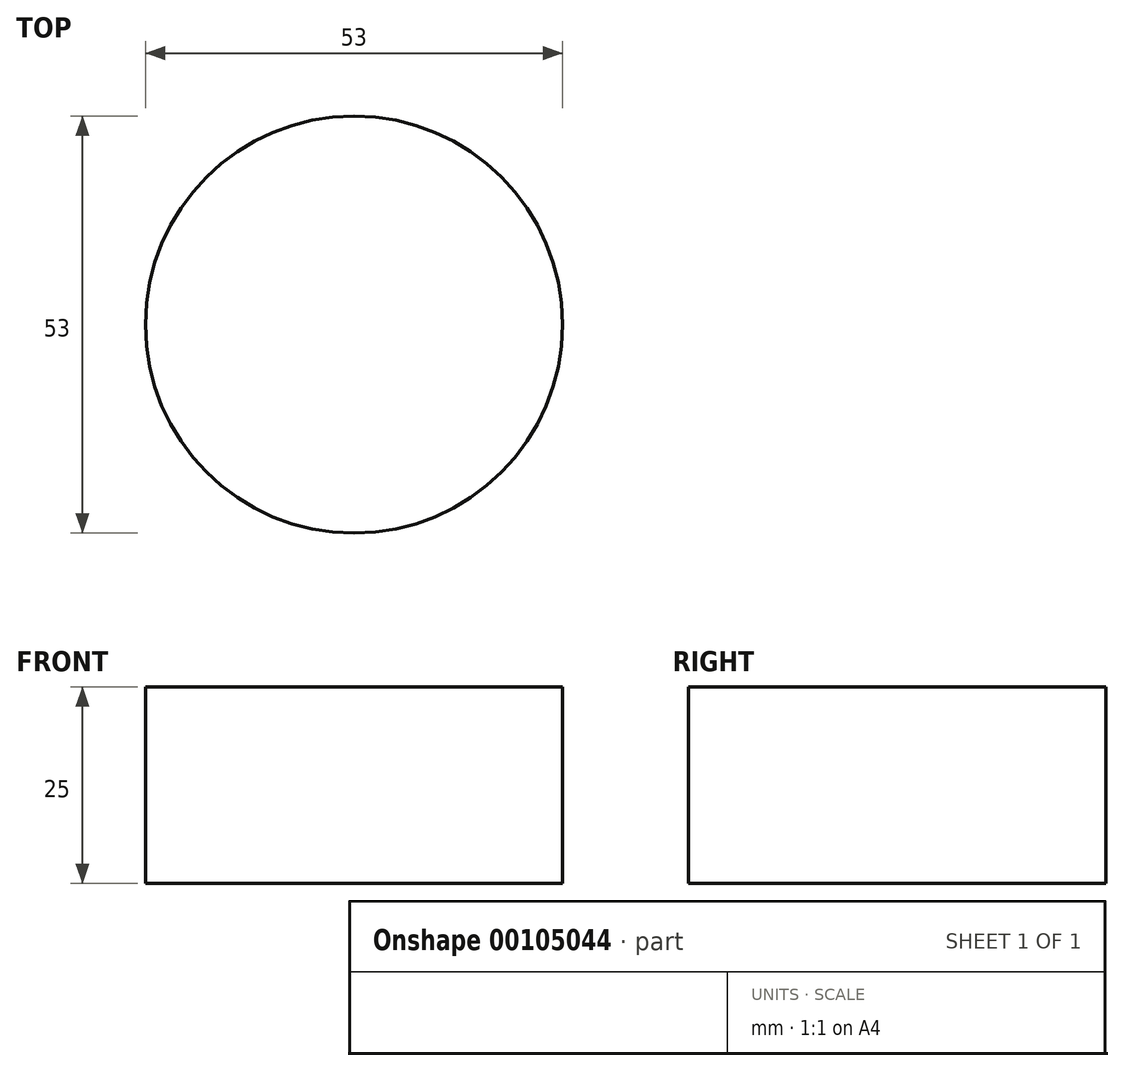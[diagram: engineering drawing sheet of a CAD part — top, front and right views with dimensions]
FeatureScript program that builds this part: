
annotation { "Feature Type Name" : "Feature", "Feature Type Description" : "" }
export const myFeature = defineFeature(function(context is Context, id is Id, definition is map)
    precondition{}
    {
        {
            assignVariable(context, id + "F0", {"name" : "G3", "anyValue" : 25});
        }
        {
            var Q0;
            Q0=qCreatedBy(makeId("Top.planeOp"),FACE);
            var sketch = newSketch(context, id + "F1", { "sketchPlane" : qUnion([Q0])});
            skCircle(sketch, "E0", {"center": v(390, 0) * mm, "radius": 26.5 * mm});
            skCircle(sketch, "E1", {"center": v(455, 0) * mm, "radius": 26.5 * mm});
            skCircle(sketch, "E2", {"center": v(520, 0) * mm, "radius": 26.5 * mm});
            skCircle(sketch, "E3", {"center": v(585, 0) * mm, "radius": 26.5 * mm});
            skCircle(sketch, "E4", {"center": v(650, 0) * mm, "radius": 26.5 * mm});
            skCircle(sketch, "E5", {"center": v(715, 0) * mm, "radius": 26.5 * mm});
            skCircle(sketch, "E6", {"center": v(780, 0) * mm, "radius": 26.5 * mm});
            skCircle(sketch, "E7", {"center": v(845, 0) * mm, "radius": 26.5 * mm});
            skCircle(sketch, "E8", {"center": v(910, 0) * mm, "radius": 26.5 * mm});
            skCircle(sketch, "E9", {"center": v(975, 0) * mm, "radius": 26.5 * mm});
            skCircle(sketch, "E10", {"center": v(1040, 0) * mm, "radius": 26.5 * mm});
            skCircle(sketch, "E11", {"center": v(1105, 0) * mm, "radius": 26.5 * mm});
            skCircle(sketch, "E12", {"center": v(1170, 0) * mm, "radius": 26.5 * mm});
            skCircle(sketch, "E13", {"center": v(1235, 0) * mm, "radius": 26.5 * mm});
            skCircle(sketch, "E14", {"center": v(1300, 0) * mm, "radius": 26.5 * mm});
            skCircle(sketch, "E15", {"center": v(1365, 0) * mm, "radius": 26.5 * mm});
            skCircle(sketch, "E16", {"center": v(1430, 0) * mm, "radius": 26.5 * mm});
            skCircle(sketch, "E17", {"center": v(1495, 0) * mm, "radius": 26.5 * mm});
            skCircle(sketch, "E18", {"center": v(1560, 0) * mm, "radius": 26.5 * mm});
            skCircle(sketch, "E19", {"center": v(422.5, 56.3) * mm, "radius": 26.5 * mm});
            skCircle(sketch, "E20", {"center": v(487.5, 56.3) * mm, "radius": 26.5 * mm});
            skCircle(sketch, "E21", {"center": v(552.5, 56.3) * mm, "radius": 26.5 * mm});
            skCircle(sketch, "E22", {"center": v(617.5, 56.3) * mm, "radius": 26.5 * mm});
            skCircle(sketch, "E23", {"center": v(682.5, 56.3) * mm, "radius": 26.5 * mm});
            skCircle(sketch, "E24", {"center": v(747.5, 56.3) * mm, "radius": 26.5 * mm});
            skCircle(sketch, "E25", {"center": v(812.5, 56.3) * mm, "radius": 26.5 * mm});
            skCircle(sketch, "E26", {"center": v(877.5, 56.3) * mm, "radius": 26.5 * mm});
            skCircle(sketch, "E27", {"center": v(942.5, 56.3) * mm, "radius": 26.5 * mm});
            skCircle(sketch, "E28", {"center": v(1007.5, 56.3) * mm, "radius": 26.5 * mm});
            skCircle(sketch, "E29", {"center": v(1072.5, 56.3) * mm, "radius": 26.5 * mm});
            skCircle(sketch, "E30", {"center": v(1137.5, 56.3) * mm, "radius": 26.5 * mm});
            skCircle(sketch, "E31", {"center": v(1202.5, 56.3) * mm, "radius": 26.5 * mm});
            skCircle(sketch, "E32", {"center": v(1267.5, 56.3) * mm, "radius": 26.5 * mm});
            skCircle(sketch, "E33", {"center": v(1332.5, 56.3) * mm, "radius": 26.5 * mm});
            skCircle(sketch, "E34", {"center": v(1397.5, 56.3) * mm, "radius": 26.5 * mm});
            skCircle(sketch, "E35", {"center": v(1462.5, 56.3) * mm, "radius": 26.5 * mm});
            skCircle(sketch, "E36", {"center": v(1527.5, 56.3) * mm, "radius": 26.5 * mm});
            skCircle(sketch, "E37", {"center": v(390, 112.58) * mm, "radius": 26.5 * mm});
            skCircle(sketch, "E38", {"center": v(455, 112.58) * mm, "radius": 26.5 * mm});
            skCircle(sketch, "E39", {"center": v(520, 112.58) * mm, "radius": 26.5 * mm});
            skCircle(sketch, "E40", {"center": v(585, 112.58) * mm, "radius": 26.5 * mm});
            skCircle(sketch, "E41", {"center": v(650, 112.58) * mm, "radius": 26.5 * mm});
            skCircle(sketch, "E42", {"center": v(715, 112.58) * mm, "radius": 26.5 * mm});
            skCircle(sketch, "E43", {"center": v(780, 112.58) * mm, "radius": 26.5 * mm});
            skCircle(sketch, "E44", {"center": v(845, 112.58) * mm, "radius": 26.5 * mm});
            skCircle(sketch, "E45", {"center": v(910, 112.58) * mm, "radius": 26.5 * mm});
            skCircle(sketch, "E46", {"center": v(975, 112.58) * mm, "radius": 26.5 * mm});
            skCircle(sketch, "E47", {"center": v(1040, 112.58) * mm, "radius": 26.5 * mm});
            skCircle(sketch, "E48", {"center": v(1105, 112.58) * mm, "radius": 26.5 * mm});
            skCircle(sketch, "E49", {"center": v(1170, 112.58) * mm, "radius": 26.5 * mm});
            skCircle(sketch, "E50", {"center": v(1235, 112.58) * mm, "radius": 26.5 * mm});
            skCircle(sketch, "E51", {"center": v(1300, 112.58) * mm, "radius": 26.5 * mm});
            skCircle(sketch, "E52", {"center": v(1365, 112.58) * mm, "radius": 26.5 * mm});
            skCircle(sketch, "E53", {"center": v(1430, 112.58) * mm, "radius": 26.5 * mm});
            skCircle(sketch, "E54", {"center": v(1495, 112.58) * mm, "radius": 26.5 * mm});
            skCircle(sketch, "E55", {"center": v(1560, 112.58) * mm, "radius": 26.5 * mm});
            skCircle(sketch, "E56", {"center": v(357.5, 168.87) * mm, "radius": 26.5 * mm});
            skCircle(sketch, "E57", {"center": v(422.5, 168.87) * mm, "radius": 26.5 * mm});
            skCircle(sketch, "E58", {"center": v(487.5, 168.87) * mm, "radius": 26.5 * mm});
            skCircle(sketch, "E59", {"center": v(552.5, 168.87) * mm, "radius": 26.5 * mm});
            skCircle(sketch, "E60", {"center": v(617.5, 168.87) * mm, "radius": 26.5 * mm});
            skCircle(sketch, "E61", {"center": v(682.5, 168.87) * mm, "radius": 26.5 * mm});
            skCircle(sketch, "E62", {"center": v(747.5, 168.87) * mm, "radius": 26.5 * mm});
            skCircle(sketch, "E63", {"center": v(812.5, 168.87) * mm, "radius": 26.5 * mm});
            skCircle(sketch, "E64", {"center": v(877.5, 168.87) * mm, "radius": 26.5 * mm});
            skCircle(sketch, "E65", {"center": v(942.5, 168.87) * mm, "radius": 26.5 * mm});
            skCircle(sketch, "E66", {"center": v(1007.5, 168.87) * mm, "radius": 26.5 * mm});
            skCircle(sketch, "E67", {"center": v(1072.5, 168.87) * mm, "radius": 26.5 * mm});
            skCircle(sketch, "E68", {"center": v(1137.5, 168.87) * mm, "radius": 26.5 * mm});
            skCircle(sketch, "E69", {"center": v(1202.5, 168.87) * mm, "radius": 26.5 * mm});
            skCircle(sketch, "E70", {"center": v(1267.5, 168.87) * mm, "radius": 26.5 * mm});
            skCircle(sketch, "E71", {"center": v(1332.5, 168.87) * mm, "radius": 26.5 * mm});
            skCircle(sketch, "E72", {"center": v(1397.5, 168.87) * mm, "radius": 26.5 * mm});
            skCircle(sketch, "E73", {"center": v(1462.5, 168.87) * mm, "radius": 26.5 * mm});
            skCircle(sketch, "E74", {"center": v(1527.5, 168.87) * mm, "radius": 26.5 * mm});
            skCircle(sketch, "E75", {"center": v(325, 225.17) * mm, "radius": 26.5 * mm});
            skCircle(sketch, "E76", {"center": v(390, 225.17) * mm, "radius": 26.5 * mm});
            skCircle(sketch, "E77", {"center": v(455, 225.17) * mm, "radius": 26.5 * mm});
            skCircle(sketch, "E78", {"center": v(520, 225.17) * mm, "radius": 26.5 * mm});
            skCircle(sketch, "E79", {"center": v(585, 225.17) * mm, "radius": 26.5 * mm});
            skCircle(sketch, "E80", {"center": v(650, 225.17) * mm, "radius": 26.5 * mm});
            skCircle(sketch, "E81", {"center": v(715, 225.17) * mm, "radius": 26.5 * mm});
            skCircle(sketch, "E82", {"center": v(780, 225.17) * mm, "radius": 26.5 * mm});
            skCircle(sketch, "E83", {"center": v(845, 225.17) * mm, "radius": 26.5 * mm});
            skCircle(sketch, "E84", {"center": v(910, 225.17) * mm, "radius": 26.5 * mm});
            skCircle(sketch, "E85", {"center": v(975, 225.17) * mm, "radius": 26.5 * mm});
            skCircle(sketch, "E86", {"center": v(1040, 225.17) * mm, "radius": 26.5 * mm});
            skCircle(sketch, "E87", {"center": v(1105, 225.17) * mm, "radius": 26.5 * mm});
            skCircle(sketch, "E88", {"center": v(1170, 225.17) * mm, "radius": 26.5 * mm});
            skCircle(sketch, "E89", {"center": v(1235, 225.17) * mm, "radius": 26.5 * mm});
            skCircle(sketch, "E90", {"center": v(1300, 225.17) * mm, "radius": 26.5 * mm});
            skCircle(sketch, "E91", {"center": v(1365, 225.17) * mm, "radius": 26.5 * mm});
            skCircle(sketch, "E92", {"center": v(1430, 225.17) * mm, "radius": 26.5 * mm});
            skCircle(sketch, "E93", {"center": v(1495, 225.17) * mm, "radius": 26.5 * mm});
            skCircle(sketch, "E94", {"center": v(1560, 225.17) * mm, "radius": 26.5 * mm});
            skCircle(sketch, "E95", {"center": v(292.5, 281.46) * mm, "radius": 26.5 * mm});
            skCircle(sketch, "E96", {"center": v(357.5, 281.46) * mm, "radius": 26.5 * mm});
            skCircle(sketch, "E97", {"center": v(422.5, 281.46) * mm, "radius": 26.5 * mm});
            skCircle(sketch, "E98", {"center": v(487.5, 281.46) * mm, "radius": 26.5 * mm});
            skCircle(sketch, "E99", {"center": v(552.5, 281.46) * mm, "radius": 26.5 * mm});
            skCircle(sketch, "E100", {"center": v(617.5, 281.46) * mm, "radius": 26.5 * mm});
            skCircle(sketch, "E101", {"center": v(682.5, 281.46) * mm, "radius": 26.5 * mm});
            skCircle(sketch, "E102", {"center": v(747.5, 281.46) * mm, "radius": 26.5 * mm});
            skCircle(sketch, "E103", {"center": v(812.5, 281.46) * mm, "radius": 26.5 * mm});
            skCircle(sketch, "E104", {"center": v(877.5, 281.46) * mm, "radius": 26.5 * mm});
            skCircle(sketch, "E105", {"center": v(942.5, 281.46) * mm, "radius": 26.5 * mm});
            skCircle(sketch, "E106", {"center": v(1007.5, 281.46) * mm, "radius": 26.5 * mm});
            skCircle(sketch, "E107", {"center": v(1072.5, 281.46) * mm, "radius": 26.5 * mm});
            skCircle(sketch, "E108", {"center": v(1137.5, 281.46) * mm, "radius": 26.5 * mm});
            skCircle(sketch, "E109", {"center": v(1202.5, 281.46) * mm, "radius": 26.5 * mm});
            skCircle(sketch, "E110", {"center": v(1267.5, 281.46) * mm, "radius": 26.5 * mm});
            skCircle(sketch, "E111", {"center": v(1332.5, 281.46) * mm, "radius": 26.5 * mm});
            skCircle(sketch, "E112", {"center": v(1397.5, 281.46) * mm, "radius": 26.5 * mm});
            skCircle(sketch, "E113", {"center": v(1462.5, 281.46) * mm, "radius": 26.5 * mm});
            skCircle(sketch, "E114", {"center": v(1527.5, 281.46) * mm, "radius": 26.5 * mm});
            skCircle(sketch, "E115", {"center": v(260, 337.75) * mm, "radius": 26.5 * mm});
            skCircle(sketch, "E116", {"center": v(325, 337.75) * mm, "radius": 26.5 * mm});
            skCircle(sketch, "E117", {"center": v(390, 337.75) * mm, "radius": 26.5 * mm});
            skCircle(sketch, "E118", {"center": v(455, 337.75) * mm, "radius": 26.5 * mm});
            skCircle(sketch, "E119", {"center": v(520, 337.75) * mm, "radius": 26.5 * mm});
            skCircle(sketch, "E120", {"center": v(585, 337.75) * mm, "radius": 26.5 * mm});
            skCircle(sketch, "E121", {"center": v(650, 337.75) * mm, "radius": 26.5 * mm});
            skCircle(sketch, "E122", {"center": v(715, 337.75) * mm, "radius": 26.5 * mm});
            skCircle(sketch, "E123", {"center": v(780, 337.75) * mm, "radius": 26.5 * mm});
            skCircle(sketch, "E124", {"center": v(845, 337.75) * mm, "radius": 26.5 * mm});
            skCircle(sketch, "E125", {"center": v(910, 337.75) * mm, "radius": 26.5 * mm});
            skCircle(sketch, "E126", {"center": v(975, 337.75) * mm, "radius": 26.5 * mm});
            skCircle(sketch, "E127", {"center": v(1040, 337.75) * mm, "radius": 26.5 * mm});
            skCircle(sketch, "E128", {"center": v(1105, 337.75) * mm, "radius": 26.5 * mm});
            skCircle(sketch, "E129", {"center": v(1170, 337.75) * mm, "radius": 26.5 * mm});
            skCircle(sketch, "E130", {"center": v(1235, 337.75) * mm, "radius": 26.5 * mm});
            skCircle(sketch, "E131", {"center": v(1300, 337.75) * mm, "radius": 26.5 * mm});
            skCircle(sketch, "E132", {"center": v(1365, 337.75) * mm, "radius": 26.5 * mm});
            skCircle(sketch, "E133", {"center": v(1430, 337.75) * mm, "radius": 26.5 * mm});
            skCircle(sketch, "E134", {"center": v(1495, 337.75) * mm, "radius": 26.5 * mm});
            skCircle(sketch, "E135", {"center": v(292.5, 394.04) * mm, "radius": 26.5 * mm});
            skCircle(sketch, "E136", {"center": v(357.5, 394.04) * mm, "radius": 26.5 * mm});
            skCircle(sketch, "E137", {"center": v(422.5, 394.04) * mm, "radius": 26.5 * mm});
            skCircle(sketch, "E138", {"center": v(487.5, 394.04) * mm, "radius": 26.5 * mm});
            skCircle(sketch, "E139", {"center": v(552.5, 394.04) * mm, "radius": 26.5 * mm});
            skCircle(sketch, "E140", {"center": v(617.5, 394.04) * mm, "radius": 26.5 * mm});
            skCircle(sketch, "E141", {"center": v(682.5, 394.04) * mm, "radius": 26.5 * mm});
            skCircle(sketch, "E142", {"center": v(747.5, 394.04) * mm, "radius": 26.5 * mm});
            skCircle(sketch, "E143", {"center": v(812.5, 394.04) * mm, "radius": 26.5 * mm});
            skCircle(sketch, "E144", {"center": v(877.5, 394.04) * mm, "radius": 26.5 * mm});
            skCircle(sketch, "E145", {"center": v(942.5, 394.04) * mm, "radius": 26.5 * mm});
            skCircle(sketch, "E146", {"center": v(1007.5, 394.04) * mm, "radius": 26.5 * mm});
            skCircle(sketch, "E147", {"center": v(1072.5, 394.04) * mm, "radius": 26.5 * mm});
            skCircle(sketch, "E148", {"center": v(1137.5, 394.04) * mm, "radius": 26.5 * mm});
            skCircle(sketch, "E149", {"center": v(1202.5, 394.04) * mm, "radius": 26.5 * mm});
            skCircle(sketch, "E150", {"center": v(1267.5, 394.04) * mm, "radius": 26.5 * mm});
            skCircle(sketch, "E151", {"center": v(1332.5, 394.04) * mm, "radius": 26.5 * mm});
            skCircle(sketch, "E152", {"center": v(1397.5, 394.04) * mm, "radius": 26.5 * mm});
            skCircle(sketch, "E153", {"center": v(1462.5, 394.04) * mm, "radius": 26.5 * mm});
            skCircle(sketch, "E154", {"center": v(1527.5, 394.04) * mm, "radius": 26.5 * mm});
            skCircle(sketch, "E155", {"center": v(325, 450.33) * mm, "radius": 26.5 * mm});
            skCircle(sketch, "E156", {"center": v(390, 450.33) * mm, "radius": 26.5 * mm});
            skCircle(sketch, "E157", {"center": v(455, 450.33) * mm, "radius": 26.5 * mm});
            skCircle(sketch, "E158", {"center": v(520, 450.33) * mm, "radius": 26.5 * mm});
            skCircle(sketch, "E159", {"center": v(585, 450.33) * mm, "radius": 26.5 * mm});
            skCircle(sketch, "E160", {"center": v(650, 450.33) * mm, "radius": 26.5 * mm});
            skCircle(sketch, "E161", {"center": v(715, 450.33) * mm, "radius": 26.5 * mm});
            skCircle(sketch, "E162", {"center": v(780, 450.33) * mm, "radius": 26.5 * mm});
            skCircle(sketch, "E163", {"center": v(845, 450.33) * mm, "radius": 26.5 * mm});
            skCircle(sketch, "E164", {"center": v(910, 450.33) * mm, "radius": 26.5 * mm});
            skCircle(sketch, "E165", {"center": v(975, 450.33) * mm, "radius": 26.5 * mm});
            skCircle(sketch, "E166", {"center": v(1040, 450.33) * mm, "radius": 26.5 * mm});
            skCircle(sketch, "E167", {"center": v(1105, 450.33) * mm, "radius": 26.5 * mm});
            skCircle(sketch, "E168", {"center": v(1170, 450.33) * mm, "radius": 26.5 * mm});
            skCircle(sketch, "E169", {"center": v(1235, 450.33) * mm, "radius": 26.5 * mm});
            skCircle(sketch, "E170", {"center": v(1300, 450.33) * mm, "radius": 26.5 * mm});
            skCircle(sketch, "E171", {"center": v(1365, 450.33) * mm, "radius": 26.5 * mm});
            skCircle(sketch, "E172", {"center": v(1430, 450.33) * mm, "radius": 26.5 * mm});
            skCircle(sketch, "E173", {"center": v(1495, 450.33) * mm, "radius": 26.5 * mm});
            skCircle(sketch, "E174", {"center": v(357.5, 506.62) * mm, "radius": 26.5 * mm});
            skCircle(sketch, "E175", {"center": v(422.5, 506.62) * mm, "radius": 26.5 * mm});
            skCircle(sketch, "E176", {"center": v(487.5, 506.62) * mm, "radius": 26.5 * mm});
            skCircle(sketch, "E177", {"center": v(552.5, 506.62) * mm, "radius": 26.5 * mm});
            skCircle(sketch, "E178", {"center": v(617.5, 506.62) * mm, "radius": 26.5 * mm});
            skCircle(sketch, "E179", {"center": v(682.5, 506.62) * mm, "radius": 26.5 * mm});
            skCircle(sketch, "E180", {"center": v(747.5, 506.62) * mm, "radius": 26.5 * mm});
            skCircle(sketch, "E181", {"center": v(812.5, 506.62) * mm, "radius": 26.5 * mm});
            skCircle(sketch, "E182", {"center": v(877.5, 506.62) * mm, "radius": 26.5 * mm});
            skCircle(sketch, "E183", {"center": v(1072.5, 506.62) * mm, "radius": 26.5 * mm});
            skCircle(sketch, "E184", {"center": v(1137.5, 506.62) * mm, "radius": 26.5 * mm});
            skCircle(sketch, "E185", {"center": v(1202.5, 506.62) * mm, "radius": 26.5 * mm});
            skCircle(sketch, "E186", {"center": v(1267.5, 506.62) * mm, "radius": 26.5 * mm});
            skCircle(sketch, "E187", {"center": v(1332.5, 506.62) * mm, "radius": 26.5 * mm});
            skCircle(sketch, "E188", {"center": v(1397.5, 506.62) * mm, "radius": 26.5 * mm});
            skCircle(sketch, "E189", {"center": v(1462.5, 506.62) * mm, "radius": 26.5 * mm});
            skCircle(sketch, "E190", {"center": v(390, 562.92) * mm, "radius": 26.5 * mm});
            skCircle(sketch, "E191", {"center": v(455, 562.92) * mm, "radius": 26.5 * mm});
            skCircle(sketch, "E192", {"center": v(520, 562.92) * mm, "radius": 26.5 * mm});
            skCircle(sketch, "E193", {"center": v(585, 562.92) * mm, "radius": 26.5 * mm});
            skCircle(sketch, "E194", {"center": v(650, 562.92) * mm, "radius": 26.5 * mm});
            skCircle(sketch, "E195", {"center": v(715, 562.92) * mm, "radius": 26.5 * mm});
            skCircle(sketch, "E196", {"center": v(780, 562.92) * mm, "radius": 26.5 * mm});
            skCircle(sketch, "E197", {"center": v(845, 562.92) * mm, "radius": 26.5 * mm});
            skCircle(sketch, "E198", {"center": v(1105, 562.92) * mm, "radius": 26.5 * mm});
            skCircle(sketch, "E199", {"center": v(1170, 562.92) * mm, "radius": 26.5 * mm});
            skCircle(sketch, "E200", {"center": v(1235, 562.92) * mm, "radius": 26.5 * mm});
            skCircle(sketch, "E201", {"center": v(1300, 562.92) * mm, "radius": 26.5 * mm});
            skCircle(sketch, "E202", {"center": v(1365, 562.92) * mm, "radius": 26.5 * mm});
            skCircle(sketch, "E203", {"center": v(1430, 562.92) * mm, "radius": 26.5 * mm});
            skCircle(sketch, "E204", {"center": v(422.5, 619.2) * mm, "radius": 26.5 * mm});
            skCircle(sketch, "E205", {"center": v(487.5, 619.2) * mm, "radius": 26.5 * mm});
            skCircle(sketch, "E206", {"center": v(552.5, 619.2) * mm, "radius": 26.5 * mm});
            skCircle(sketch, "E207", {"center": v(617.5, 619.2) * mm, "radius": 26.5 * mm});
            skCircle(sketch, "E208", {"center": v(682.5, 619.2) * mm, "radius": 26.5 * mm});
            skCircle(sketch, "E209", {"center": v(747.5, 619.2) * mm, "radius": 26.5 * mm});
            skCircle(sketch, "E210", {"center": v(812.5, 619.2) * mm, "radius": 26.5 * mm});
            skCircle(sketch, "E211", {"center": v(877.5, 619.2) * mm, "radius": 26.5 * mm});
            skCircle(sketch, "E212", {"center": v(1072.5, 619.2) * mm, "radius": 26.5 * mm});
            skCircle(sketch, "E213", {"center": v(1137.5, 619.2) * mm, "radius": 26.5 * mm});
            skCircle(sketch, "E214", {"center": v(1202.5, 619.2) * mm, "radius": 26.5 * mm});
            skCircle(sketch, "E215", {"center": v(1267.5, 619.2) * mm, "radius": 26.5 * mm});
            skCircle(sketch, "E216", {"center": v(1332.5, 619.2) * mm, "radius": 26.5 * mm});
            skCircle(sketch, "E217", {"center": v(1397.5, 619.2) * mm, "radius": 26.5 * mm});
            skCircle(sketch, "E218", {"center": v(455, 675.5) * mm, "radius": 26.5 * mm});
            skCircle(sketch, "E219", {"center": v(520, 675.5) * mm, "radius": 26.5 * mm});
            skCircle(sketch, "E220", {"center": v(585, 675.5) * mm, "radius": 26.5 * mm});
            skCircle(sketch, "E221", {"center": v(650, 675.5) * mm, "radius": 26.5 * mm});
            skCircle(sketch, "E222", {"center": v(715, 675.5) * mm, "radius": 26.5 * mm});
            skCircle(sketch, "E223", {"center": v(780, 675.5) * mm, "radius": 26.5 * mm});
            skCircle(sketch, "E224", {"center": v(845, 675.5) * mm, "radius": 26.5 * mm});
            skCircle(sketch, "E225", {"center": v(910, 675.5) * mm, "radius": 26.5 * mm});
            skCircle(sketch, "E226", {"center": v(975, 675.5) * mm, "radius": 26.5 * mm});
            skCircle(sketch, "E227", {"center": v(1040, 675.5) * mm, "radius": 26.5 * mm});
            skCircle(sketch, "E228", {"center": v(1105, 675.5) * mm, "radius": 26.5 * mm});
            skCircle(sketch, "E229", {"center": v(1170, 675.5) * mm, "radius": 26.5 * mm});
            skCircle(sketch, "E230", {"center": v(1235, 675.5) * mm, "radius": 26.5 * mm});
            skCircle(sketch, "E231", {"center": v(1300, 675.5) * mm, "radius": 26.5 * mm});
            skCircle(sketch, "E232", {"center": v(1365, 675.5) * mm, "radius": 26.5 * mm});
            skCircle(sketch, "E233", {"center": v(487.5, 731.8) * mm, "radius": 26.5 * mm});
            skCircle(sketch, "E234", {"center": v(552.5, 731.8) * mm, "radius": 26.5 * mm});
            skCircle(sketch, "E235", {"center": v(617.5, 731.8) * mm, "radius": 26.5 * mm});
            skCircle(sketch, "E236", {"center": v(682.5, 731.8) * mm, "radius": 26.5 * mm});
            skCircle(sketch, "E237", {"center": v(747.5, 731.8) * mm, "radius": 26.5 * mm});
            skCircle(sketch, "E238", {"center": v(812.5, 731.8) * mm, "radius": 26.5 * mm});
            skCircle(sketch, "E239", {"center": v(877.5, 731.8) * mm, "radius": 26.5 * mm});
            skCircle(sketch, "E240", {"center": v(942.5, 731.8) * mm, "radius": 26.5 * mm});
            skCircle(sketch, "E241", {"center": v(1007.5, 731.8) * mm, "radius": 26.5 * mm});
            skCircle(sketch, "E242", {"center": v(1072.5, 731.8) * mm, "radius": 26.5 * mm});
            skCircle(sketch, "E243", {"center": v(1137.5, 731.8) * mm, "radius": 26.5 * mm});
            skCircle(sketch, "E244", {"center": v(1202.5, 731.8) * mm, "radius": 26.5 * mm});
            skCircle(sketch, "E245", {"center": v(1267.5, 731.8) * mm, "radius": 26.5 * mm});
            skCircle(sketch, "E246", {"center": v(1332.5, 731.8) * mm, "radius": 26.5 * mm});
            skCircle(sketch, "E247", {"center": v(1397.5, 731.8) * mm, "radius": 26.5 * mm});
            skCircle(sketch, "E248", {"center": v(520, 788.08) * mm, "radius": 26.5 * mm});
            skCircle(sketch, "E249", {"center": v(585, 788.08) * mm, "radius": 26.5 * mm});
            skCircle(sketch, "E250", {"center": v(650, 788.08) * mm, "radius": 26.5 * mm});
            skCircle(sketch, "E251", {"center": v(715, 788.08) * mm, "radius": 26.5 * mm});
            skCircle(sketch, "E252", {"center": v(780, 788.08) * mm, "radius": 26.5 * mm});
            skCircle(sketch, "E253", {"center": v(845, 788.08) * mm, "radius": 26.5 * mm});
            skCircle(sketch, "E254", {"center": v(910, 788.08) * mm, "radius": 26.5 * mm});
            skCircle(sketch, "E255", {"center": v(975, 788.08) * mm, "radius": 26.5 * mm});
            skCircle(sketch, "E256", {"center": v(1040, 788.08) * mm, "radius": 26.5 * mm});
            skCircle(sketch, "E257", {"center": v(1105, 788.08) * mm, "radius": 26.5 * mm});
            skCircle(sketch, "E258", {"center": v(1170, 788.08) * mm, "radius": 26.5 * mm});
            skCircle(sketch, "E259", {"center": v(1235, 788.08) * mm, "radius": 26.5 * mm});
            skCircle(sketch, "E260", {"center": v(1300, 788.08) * mm, "radius": 26.5 * mm});
            skCircle(sketch, "E261", {"center": v(1365, 788.08) * mm, "radius": 26.5 * mm});
            skCircle(sketch, "E262", {"center": v(552.5, 844.37) * mm, "radius": 26.5 * mm});
            skCircle(sketch, "E263", {"center": v(617.5, 844.37) * mm, "radius": 26.5 * mm});
            skCircle(sketch, "E264", {"center": v(682.5, 844.37) * mm, "radius": 26.5 * mm});
            skCircle(sketch, "E265", {"center": v(747.5, 844.37) * mm, "radius": 26.5 * mm});
            skCircle(sketch, "E266", {"center": v(812.5, 844.37) * mm, "radius": 26.5 * mm});
            skCircle(sketch, "E267", {"center": v(877.5, 844.37) * mm, "radius": 26.5 * mm});
            skCircle(sketch, "E268", {"center": v(942.5, 844.37) * mm, "radius": 26.5 * mm});
            skCircle(sketch, "E269", {"center": v(1007.5, 844.37) * mm, "radius": 26.5 * mm});
            skCircle(sketch, "E270", {"center": v(1072.5, 844.37) * mm, "radius": 26.5 * mm});
            skCircle(sketch, "E271", {"center": v(1137.5, 844.37) * mm, "radius": 26.5 * mm});
            skCircle(sketch, "E272", {"center": v(1202.5, 844.37) * mm, "radius": 26.5 * mm});
            skCircle(sketch, "E273", {"center": v(1267.5, 844.37) * mm, "radius": 26.5 * mm});
            skCircle(sketch, "E274", {"center": v(1332.5, 844.37) * mm, "radius": 26.5 * mm});
            skCircle(sketch, "E275", {"center": v(585, 900.67) * mm, "radius": 26.5 * mm});
            skCircle(sketch, "E276", {"center": v(650, 900.67) * mm, "radius": 26.5 * mm});
            skCircle(sketch, "E277", {"center": v(715, 900.67) * mm, "radius": 26.5 * mm});
            skCircle(sketch, "E278", {"center": v(780, 900.67) * mm, "radius": 26.5 * mm});
            skCircle(sketch, "E279", {"center": v(845, 900.67) * mm, "radius": 26.5 * mm});
            skCircle(sketch, "E280", {"center": v(910, 900.67) * mm, "radius": 26.5 * mm});
            skCircle(sketch, "E281", {"center": v(975, 900.67) * mm, "radius": 26.5 * mm});
            skCircle(sketch, "E282", {"center": v(1040, 900.67) * mm, "radius": 26.5 * mm});
            skCircle(sketch, "E283", {"center": v(1105, 900.67) * mm, "radius": 26.5 * mm});
            skCircle(sketch, "E284", {"center": v(1170, 900.67) * mm, "radius": 26.5 * mm});
            skCircle(sketch, "E285", {"center": v(1235, 900.67) * mm, "radius": 26.5 * mm});
            skCircle(sketch, "E286", {"center": v(617.5, 956.96) * mm, "radius": 26.5 * mm});
            skCircle(sketch, "E287", {"center": v(682.5, 956.96) * mm, "radius": 26.5 * mm});
            skCircle(sketch, "E288", {"center": v(747.5, 956.96) * mm, "radius": 26.5 * mm});
            skCircle(sketch, "E289", {"center": v(812.5, 956.96) * mm, "radius": 26.5 * mm});
            skCircle(sketch, "E290", {"center": v(877.5, 956.96) * mm, "radius": 26.5 * mm});
            skCircle(sketch, "E291", {"center": v(942.5, 956.96) * mm, "radius": 26.5 * mm});
            skCircle(sketch, "E292", {"center": v(1007.5, 956.96) * mm, "radius": 26.5 * mm});
            skCircle(sketch, "E293", {"center": v(1072.5, 956.96) * mm, "radius": 26.5 * mm});
            skCircle(sketch, "E294", {"center": v(1137.5, 956.96) * mm, "radius": 26.5 * mm});
            skCircle(sketch, "E295", {"center": v(1202.5, 956.96) * mm, "radius": 26.5 * mm});
            skCircle(sketch, "E296", {"center": v(650, 1013.25) * mm, "radius": 26.5 * mm});
            skCircle(sketch, "E297", {"center": v(715, 1013.25) * mm, "radius": 26.5 * mm});
            skCircle(sketch, "E298", {"center": v(780, 1013.25) * mm, "radius": 26.5 * mm});
            skCircle(sketch, "E299", {"center": v(845, 1013.25) * mm, "radius": 26.5 * mm});
            skCircle(sketch, "E300", {"center": v(910, 1013.25) * mm, "radius": 26.5 * mm});
            skCircle(sketch, "E301", {"center": v(975, 1013.25) * mm, "radius": 26.5 * mm});
            skCircle(sketch, "E302", {"center": v(1040, 1013.25) * mm, "radius": 26.5 * mm});
            skCircle(sketch, "E303", {"center": v(1105, 1013.25) * mm, "radius": 26.5 * mm});
            skCircle(sketch, "E304", {"center": v(1170, 1013.25) * mm, "radius": 26.5 * mm});
            skCircle(sketch, "E305", {"center": v(682.5, 1069.54) * mm, "radius": 26.5 * mm});
            skCircle(sketch, "E306", {"center": v(747.5, 1069.54) * mm, "radius": 26.5 * mm});
            skCircle(sketch, "E307", {"center": v(812.5, 1069.54) * mm, "radius": 26.5 * mm});
            skCircle(sketch, "E308", {"center": v(877.5, 1069.54) * mm, "radius": 26.5 * mm});
            skCircle(sketch, "E309", {"center": v(942.5, 1069.54) * mm, "radius": 26.5 * mm});
            skCircle(sketch, "E310", {"center": v(1007.5, 1069.54) * mm, "radius": 26.5 * mm});
            skCircle(sketch, "E311", {"center": v(1072.5, 1069.54) * mm, "radius": 26.5 * mm});
            skCircle(sketch, "E312", {"center": v(1137.5, 1069.54) * mm, "radius": 26.5 * mm});
            skCircle(sketch, "E313", {"center": v(715, 1125.83) * mm, "radius": 26.5 * mm});
            skCircle(sketch, "E314", {"center": v(780, 1125.83) * mm, "radius": 26.5 * mm});
            skCircle(sketch, "E315", {"center": v(845, 1125.83) * mm, "radius": 26.5 * mm});
            skCircle(sketch, "E316", {"center": v(910, 1125.83) * mm, "radius": 26.5 * mm});
            skCircle(sketch, "E317", {"center": v(975, 1125.83) * mm, "radius": 26.5 * mm});
            skCircle(sketch, "E318", {"center": v(1040, 1125.83) * mm, "radius": 26.5 * mm});
            skCircle(sketch, "E319", {"center": v(1105, 1125.83) * mm, "radius": 26.5 * mm});
            skCircle(sketch, "E320", {"center": v(747.5, 1182.12) * mm, "radius": 26.5 * mm});
            skCircle(sketch, "E321", {"center": v(812.5, 1182.12) * mm, "radius": 26.5 * mm});
            skCircle(sketch, "E322", {"center": v(877.5, 1182.12) * mm, "radius": 26.5 * mm});
            skCircle(sketch, "E323", {"center": v(942.5, 1182.12) * mm, "radius": 26.5 * mm});
            skCircle(sketch, "E324", {"center": v(1007.5, 1182.12) * mm, "radius": 26.5 * mm});
            skCircle(sketch, "E325", {"center": v(780, 1238.42) * mm, "radius": 26.5 * mm});
            skCircle(sketch, "E326", {"center": v(845, 1238.42) * mm, "radius": 26.5 * mm});
            skCircle(sketch, "E327", {"center": v(910, 1238.42) * mm, "radius": 26.5 * mm});
            skCircle(sketch, "E328", {"center": v(975, 1238.42) * mm, "radius": 26.5 * mm});
            skCircle(sketch, "E329", {"center": v(812.5, 1294.7) * mm, "radius": 26.5 * mm});
            skCircle(sketch, "E330", {"center": v(877.5, 1294.7) * mm, "radius": 26.5 * mm});
            skCircle(sketch, "E331", {"center": v(0, 0) * mm, "radius": 304.8 * mm, "construction": true});
            skCircle(sketch, "E332", {"center": v(0, 0) * mm, "radius": 1655.21 * mm, "construction": true});
            skCircle(sketch, "E333", {"center": v(975, 562.92) * mm, "radius": 58 * mm});
            skCircle(sketch, "E334", {"center": v(195, 337.75) * mm, "radius": 26.5 * mm});
            skCircle(sketch, "E335", {"center": v(227.5, 394.04) * mm, "radius": 26.5 * mm});
            skCircle(sketch, "E336", {"center": v(260, 450.33) * mm, "radius": 26.5 * mm});
            skCircle(sketch, "E337", {"center": v(292.5, 506.62) * mm, "radius": 26.5 * mm});
            skCircle(sketch, "E338", {"center": v(325, 562.92) * mm, "radius": 26.5 * mm});
            skCircle(sketch, "E339", {"center": v(357.5, 619.2) * mm, "radius": 26.5 * mm});
            skCircle(sketch, "E340", {"center": v(390, 675.5) * mm, "radius": 26.5 * mm});
            skCircle(sketch, "E341", {"center": v(422.5, 731.8) * mm, "radius": 26.5 * mm});
            skCircle(sketch, "E342", {"center": v(455, 788.08) * mm, "radius": 26.5 * mm});
            skCircle(sketch, "E343", {"center": v(487.5, 844.37) * mm, "radius": 26.5 * mm});
            skCircle(sketch, "E344", {"center": v(520, 900.67) * mm, "radius": 26.5 * mm});
            skCircle(sketch, "E345", {"center": v(552.5, 956.96) * mm, "radius": 26.5 * mm});
            skCircle(sketch, "E346", {"center": v(585, 1013.25) * mm, "radius": 26.5 * mm});
            skCircle(sketch, "E347", {"center": v(617.5, 1069.54) * mm, "radius": 26.5 * mm});
            skCircle(sketch, "E348", {"center": v(650, 1125.83) * mm, "radius": 26.5 * mm});
            skCircle(sketch, "E349", {"center": v(682.5, 1182.12) * mm, "radius": 26.5 * mm});
            skCircle(sketch, "E350", {"center": v(715, 1238.42) * mm, "radius": 26.5 * mm});
            skCircle(sketch, "E351", {"center": v(747.5, 1294.7) * mm, "radius": 26.5 * mm});
            skCircle(sketch, "E352", {"center": v(780, 1351) * mm, "radius": 26.5 * mm});
            skCircle(sketch, "E353", {"center": v(162.5, 394.04) * mm, "radius": 26.5 * mm});
            skCircle(sketch, "E354", {"center": v(195, 450.33) * mm, "radius": 26.5 * mm});
            skCircle(sketch, "E355", {"center": v(227.5, 506.62) * mm, "radius": 26.5 * mm});
            skCircle(sketch, "E356", {"center": v(260, 562.92) * mm, "radius": 26.5 * mm});
            skCircle(sketch, "E357", {"center": v(292.5, 619.2) * mm, "radius": 26.5 * mm});
            skCircle(sketch, "E358", {"center": v(325, 675.5) * mm, "radius": 26.5 * mm});
            skCircle(sketch, "E359", {"center": v(357.5, 731.8) * mm, "radius": 26.5 * mm});
            skCircle(sketch, "E360", {"center": v(390, 788.08) * mm, "radius": 26.5 * mm});
            skCircle(sketch, "E361", {"center": v(422.5, 844.37) * mm, "radius": 26.5 * mm});
            skCircle(sketch, "E362", {"center": v(455, 900.67) * mm, "radius": 26.5 * mm});
            skCircle(sketch, "E363", {"center": v(487.5, 956.96) * mm, "radius": 26.5 * mm});
            skCircle(sketch, "E364", {"center": v(520, 1013.25) * mm, "radius": 26.5 * mm});
            skCircle(sketch, "E365", {"center": v(552.5, 1069.54) * mm, "radius": 26.5 * mm});
            skCircle(sketch, "E366", {"center": v(585, 1125.83) * mm, "radius": 26.5 * mm});
            skCircle(sketch, "E367", {"center": v(617.5, 1182.12) * mm, "radius": 26.5 * mm});
            skCircle(sketch, "E368", {"center": v(650, 1238.42) * mm, "radius": 26.5 * mm});
            skCircle(sketch, "E369", {"center": v(682.5, 1294.7) * mm, "radius": 26.5 * mm});
            skCircle(sketch, "E370", {"center": v(715, 1351) * mm, "radius": 26.5 * mm});
            skCircle(sketch, "E371", {"center": v(97.5, 394.04) * mm, "radius": 26.5 * mm});
            skCircle(sketch, "E372", {"center": v(130, 450.33) * mm, "radius": 26.5 * mm});
            skCircle(sketch, "E373", {"center": v(162.5, 506.62) * mm, "radius": 26.5 * mm});
            skCircle(sketch, "E374", {"center": v(195, 562.92) * mm, "radius": 26.5 * mm});
            skCircle(sketch, "E375", {"center": v(227.5, 619.2) * mm, "radius": 26.5 * mm});
            skCircle(sketch, "E376", {"center": v(260, 675.5) * mm, "radius": 26.5 * mm});
            skCircle(sketch, "E377", {"center": v(292.5, 731.8) * mm, "radius": 26.5 * mm});
            skCircle(sketch, "E378", {"center": v(325, 788.08) * mm, "radius": 26.5 * mm});
            skCircle(sketch, "E379", {"center": v(357.5, 844.37) * mm, "radius": 26.5 * mm});
            skCircle(sketch, "E380", {"center": v(390, 900.67) * mm, "radius": 26.5 * mm});
            skCircle(sketch, "E381", {"center": v(422.5, 956.96) * mm, "radius": 26.5 * mm});
            skCircle(sketch, "E382", {"center": v(455, 1013.25) * mm, "radius": 26.5 * mm});
            skCircle(sketch, "E383", {"center": v(487.5, 1069.54) * mm, "radius": 26.5 * mm});
            skCircle(sketch, "E384", {"center": v(520, 1125.83) * mm, "radius": 26.5 * mm});
            skCircle(sketch, "E385", {"center": v(552.5, 1182.12) * mm, "radius": 26.5 * mm});
            skCircle(sketch, "E386", {"center": v(585, 1238.42) * mm, "radius": 26.5 * mm});
            skCircle(sketch, "E387", {"center": v(617.5, 1294.7) * mm, "radius": 26.5 * mm});
            skCircle(sketch, "E388", {"center": v(650, 1351) * mm, "radius": 26.5 * mm});
            skCircle(sketch, "E389", {"center": v(682.5, 1407.3) * mm, "radius": 26.5 * mm});
            skCircle(sketch, "E390", {"center": v(32.5, 394.04) * mm, "radius": 26.5 * mm});
            skCircle(sketch, "E391", {"center": v(65, 450.33) * mm, "radius": 26.5 * mm});
            skCircle(sketch, "E392", {"center": v(97.5, 506.62) * mm, "radius": 26.5 * mm});
            skCircle(sketch, "E393", {"center": v(130, 562.92) * mm, "radius": 26.5 * mm});
            skCircle(sketch, "E394", {"center": v(162.5, 619.2) * mm, "radius": 26.5 * mm});
            skCircle(sketch, "E395", {"center": v(195, 675.5) * mm, "radius": 26.5 * mm});
            skCircle(sketch, "E396", {"center": v(227.5, 731.8) * mm, "radius": 26.5 * mm});
            skCircle(sketch, "E397", {"center": v(260, 788.08) * mm, "radius": 26.5 * mm});
            skCircle(sketch, "E398", {"center": v(292.5, 844.37) * mm, "radius": 26.5 * mm});
            skCircle(sketch, "E399", {"center": v(325, 900.67) * mm, "radius": 26.5 * mm});
            skCircle(sketch, "E400", {"center": v(357.5, 956.96) * mm, "radius": 26.5 * mm});
            skCircle(sketch, "E401", {"center": v(390, 1013.25) * mm, "radius": 26.5 * mm});
            skCircle(sketch, "E402", {"center": v(422.5, 1069.54) * mm, "radius": 26.5 * mm});
            skCircle(sketch, "E403", {"center": v(455, 1125.83) * mm, "radius": 26.5 * mm});
            skCircle(sketch, "E404", {"center": v(487.5, 1182.12) * mm, "radius": 26.5 * mm});
            skCircle(sketch, "E405", {"center": v(520, 1238.42) * mm, "radius": 26.5 * mm});
            skCircle(sketch, "E406", {"center": v(552.5, 1294.7) * mm, "radius": 26.5 * mm});
            skCircle(sketch, "E407", {"center": v(585, 1351) * mm, "radius": 26.5 * mm});
            skCircle(sketch, "E408", {"center": v(617.5, 1407.3) * mm, "radius": 26.5 * mm});
            skCircle(sketch, "E409", {"center": v(-32.5, 394.04) * mm, "radius": 26.5 * mm});
            skCircle(sketch, "E410", {"center": v(0, 450.33) * mm, "radius": 26.5 * mm});
            skCircle(sketch, "E411", {"center": v(32.5, 506.62) * mm, "radius": 26.5 * mm});
            skCircle(sketch, "E412", {"center": v(65, 562.92) * mm, "radius": 26.5 * mm});
            skCircle(sketch, "E413", {"center": v(97.5, 619.2) * mm, "radius": 26.5 * mm});
            skCircle(sketch, "E414", {"center": v(130, 675.5) * mm, "radius": 26.5 * mm});
            skCircle(sketch, "E415", {"center": v(162.5, 731.8) * mm, "radius": 26.5 * mm});
            skCircle(sketch, "E416", {"center": v(195, 788.08) * mm, "radius": 26.5 * mm});
            skCircle(sketch, "E417", {"center": v(227.5, 844.37) * mm, "radius": 26.5 * mm});
            skCircle(sketch, "E418", {"center": v(260, 900.67) * mm, "radius": 26.5 * mm});
            skCircle(sketch, "E419", {"center": v(292.5, 956.96) * mm, "radius": 26.5 * mm});
            skCircle(sketch, "E420", {"center": v(325, 1013.25) * mm, "radius": 26.5 * mm});
            skCircle(sketch, "E421", {"center": v(357.5, 1069.54) * mm, "radius": 26.5 * mm});
            skCircle(sketch, "E422", {"center": v(390, 1125.83) * mm, "radius": 26.5 * mm});
            skCircle(sketch, "E423", {"center": v(422.5, 1182.12) * mm, "radius": 26.5 * mm});
            skCircle(sketch, "E424", {"center": v(455, 1238.42) * mm, "radius": 26.5 * mm});
            skCircle(sketch, "E425", {"center": v(487.5, 1294.7) * mm, "radius": 26.5 * mm});
            skCircle(sketch, "E426", {"center": v(520, 1351) * mm, "radius": 26.5 * mm});
            skCircle(sketch, "E427", {"center": v(552.5, 1407.3) * mm, "radius": 26.5 * mm});
            skCircle(sketch, "E428", {"center": v(585, 1463.58) * mm, "radius": 26.5 * mm});
            skCircle(sketch, "E429", {"center": v(-97.5, 394.04) * mm, "radius": 26.5 * mm});
            skCircle(sketch, "E430", {"center": v(-65, 450.33) * mm, "radius": 26.5 * mm});
            skCircle(sketch, "E431", {"center": v(-32.5, 506.62) * mm, "radius": 26.5 * mm});
            skCircle(sketch, "E432", {"center": v(0, 562.92) * mm, "radius": 26.5 * mm});
            skCircle(sketch, "E433", {"center": v(32.5, 619.2) * mm, "radius": 26.5 * mm});
            skCircle(sketch, "E434", {"center": v(65, 675.5) * mm, "radius": 26.5 * mm});
            skCircle(sketch, "E435", {"center": v(97.5, 731.8) * mm, "radius": 26.5 * mm});
            skCircle(sketch, "E436", {"center": v(130, 788.08) * mm, "radius": 26.5 * mm});
            skCircle(sketch, "E437", {"center": v(162.5, 844.37) * mm, "radius": 26.5 * mm});
            skCircle(sketch, "E438", {"center": v(195, 900.67) * mm, "radius": 26.5 * mm});
            skCircle(sketch, "E439", {"center": v(227.5, 956.96) * mm, "radius": 26.5 * mm});
            skCircle(sketch, "E440", {"center": v(260, 1013.25) * mm, "radius": 26.5 * mm});
            skCircle(sketch, "E441", {"center": v(292.5, 1069.54) * mm, "radius": 26.5 * mm});
            skCircle(sketch, "E442", {"center": v(325, 1125.83) * mm, "radius": 26.5 * mm});
            skCircle(sketch, "E443", {"center": v(357.5, 1182.12) * mm, "radius": 26.5 * mm});
            skCircle(sketch, "E444", {"center": v(390, 1238.42) * mm, "radius": 26.5 * mm});
            skCircle(sketch, "E445", {"center": v(422.5, 1294.7) * mm, "radius": 26.5 * mm});
            skCircle(sketch, "E446", {"center": v(455, 1351) * mm, "radius": 26.5 * mm});
            skCircle(sketch, "E447", {"center": v(487.5, 1407.3) * mm, "radius": 26.5 * mm});
            skCircle(sketch, "E448", {"center": v(520, 1463.58) * mm, "radius": 26.5 * mm});
            skCircle(sketch, "E449", {"center": v(-162.5, 394.04) * mm, "radius": 26.5 * mm});
            skCircle(sketch, "E450", {"center": v(-130, 450.33) * mm, "radius": 26.5 * mm});
            skCircle(sketch, "E451", {"center": v(-97.5, 506.62) * mm, "radius": 26.5 * mm});
            skCircle(sketch, "E452", {"center": v(-65, 562.92) * mm, "radius": 26.5 * mm});
            skCircle(sketch, "E453", {"center": v(-32.5, 619.2) * mm, "radius": 26.5 * mm});
            skCircle(sketch, "E454", {"center": v(0, 675.5) * mm, "radius": 26.5 * mm});
            skCircle(sketch, "E455", {"center": v(32.5, 731.8) * mm, "radius": 26.5 * mm});
            skCircle(sketch, "E456", {"center": v(65, 788.08) * mm, "radius": 26.5 * mm});
            skCircle(sketch, "E457", {"center": v(97.5, 844.37) * mm, "radius": 26.5 * mm});
            skCircle(sketch, "E458", {"center": v(130, 900.67) * mm, "radius": 26.5 * mm});
            skCircle(sketch, "E459", {"center": v(162.5, 956.96) * mm, "radius": 26.5 * mm});
            skCircle(sketch, "E460", {"center": v(195, 1013.25) * mm, "radius": 26.5 * mm});
            skCircle(sketch, "E461", {"center": v(227.5, 1069.54) * mm, "radius": 26.5 * mm});
            skCircle(sketch, "E462", {"center": v(260, 1125.83) * mm, "radius": 26.5 * mm});
            skCircle(sketch, "E463", {"center": v(292.5, 1182.12) * mm, "radius": 26.5 * mm});
            skCircle(sketch, "E464", {"center": v(325, 1238.42) * mm, "radius": 26.5 * mm});
            skCircle(sketch, "E465", {"center": v(357.5, 1294.7) * mm, "radius": 26.5 * mm});
            skCircle(sketch, "E466", {"center": v(390, 1351) * mm, "radius": 26.5 * mm});
            skCircle(sketch, "E467", {"center": v(422.5, 1407.3) * mm, "radius": 26.5 * mm});
            skCircle(sketch, "E468", {"center": v(455, 1463.58) * mm, "radius": 26.5 * mm});
            skCircle(sketch, "E469", {"center": v(-195, 450.33) * mm, "radius": 26.5 * mm});
            skCircle(sketch, "E470", {"center": v(-162.5, 506.62) * mm, "radius": 26.5 * mm});
            skCircle(sketch, "E471", {"center": v(-130, 562.92) * mm, "radius": 26.5 * mm});
            skCircle(sketch, "E472", {"center": v(-97.5, 619.2) * mm, "radius": 26.5 * mm});
            skCircle(sketch, "E473", {"center": v(-65, 675.5) * mm, "radius": 26.5 * mm});
            skCircle(sketch, "E474", {"center": v(-32.5, 731.8) * mm, "radius": 26.5 * mm});
            skCircle(sketch, "E475", {"center": v(0, 788.08) * mm, "radius": 26.5 * mm});
            skCircle(sketch, "E476", {"center": v(32.5, 844.37) * mm, "radius": 26.5 * mm});
            skCircle(sketch, "E477", {"center": v(65, 900.67) * mm, "radius": 26.5 * mm});
            skCircle(sketch, "E478", {"center": v(97.5, 956.96) * mm, "radius": 26.5 * mm});
            skCircle(sketch, "E479", {"center": v(130, 1013.25) * mm, "radius": 26.5 * mm});
            skCircle(sketch, "E480", {"center": v(162.5, 1069.54) * mm, "radius": 26.5 * mm});
            skCircle(sketch, "E481", {"center": v(195, 1125.83) * mm, "radius": 26.5 * mm});
            skCircle(sketch, "E482", {"center": v(227.5, 1182.12) * mm, "radius": 26.5 * mm});
            skCircle(sketch, "E483", {"center": v(260, 1238.42) * mm, "radius": 26.5 * mm});
            skCircle(sketch, "E484", {"center": v(292.5, 1294.7) * mm, "radius": 26.5 * mm});
            skCircle(sketch, "E485", {"center": v(325, 1351) * mm, "radius": 26.5 * mm});
            skCircle(sketch, "E486", {"center": v(357.5, 1407.3) * mm, "radius": 26.5 * mm});
            skCircle(sketch, "E487", {"center": v(390, 1463.58) * mm, "radius": 26.5 * mm});
            skCircle(sketch, "E488", {"center": v(422.5, 1519.87) * mm, "radius": 26.5 * mm});
            skCircle(sketch, "E489", {"center": v(-227.5, 506.62) * mm, "radius": 26.5 * mm});
            skCircle(sketch, "E490", {"center": v(-195, 562.92) * mm, "radius": 26.5 * mm});
            skCircle(sketch, "E491", {"center": v(-162.5, 619.2) * mm, "radius": 26.5 * mm});
            skCircle(sketch, "E492", {"center": v(-130, 675.5) * mm, "radius": 26.5 * mm});
            skCircle(sketch, "E493", {"center": v(-97.5, 731.8) * mm, "radius": 26.5 * mm});
            skCircle(sketch, "E494", {"center": v(-65, 788.08) * mm, "radius": 26.5 * mm});
            skCircle(sketch, "E495", {"center": v(-32.5, 844.37) * mm, "radius": 26.5 * mm});
            skCircle(sketch, "E496", {"center": v(0, 900.67) * mm, "radius": 26.5 * mm});
            skCircle(sketch, "E497", {"center": v(32.5, 956.96) * mm, "radius": 26.5 * mm});
            skCircle(sketch, "E498", {"center": v(65, 1013.25) * mm, "radius": 26.5 * mm});
            skCircle(sketch, "E499", {"center": v(97.5, 1069.54) * mm, "radius": 26.5 * mm});
            skCircle(sketch, "E500", {"center": v(130, 1125.83) * mm, "radius": 26.5 * mm});
            skCircle(sketch, "E501", {"center": v(162.5, 1182.12) * mm, "radius": 26.5 * mm});
            skCircle(sketch, "E502", {"center": v(195, 1238.42) * mm, "radius": 26.5 * mm});
            skCircle(sketch, "E503", {"center": v(227.5, 1294.7) * mm, "radius": 26.5 * mm});
            skCircle(sketch, "E504", {"center": v(260, 1351) * mm, "radius": 26.5 * mm});
            skCircle(sketch, "E505", {"center": v(292.5, 1407.3) * mm, "radius": 26.5 * mm});
            skCircle(sketch, "E506", {"center": v(325, 1463.58) * mm, "radius": 26.5 * mm});
            skCircle(sketch, "E507", {"center": v(357.5, 1519.87) * mm, "radius": 26.5 * mm});
            skCircle(sketch, "E508", {"center": v(-260, 562.92) * mm, "radius": 26.5 * mm});
            skCircle(sketch, "E509", {"center": v(-227.5, 619.2) * mm, "radius": 26.5 * mm});
            skCircle(sketch, "E510", {"center": v(-195, 675.5) * mm, "radius": 26.5 * mm});
            skCircle(sketch, "E511", {"center": v(-162.5, 731.8) * mm, "radius": 26.5 * mm});
            skCircle(sketch, "E512", {"center": v(-130, 788.08) * mm, "radius": 26.5 * mm});
            skCircle(sketch, "E513", {"center": v(-97.5, 844.37) * mm, "radius": 26.5 * mm});
            skCircle(sketch, "E514", {"center": v(-65, 900.67) * mm, "radius": 26.5 * mm});
            skCircle(sketch, "E515", {"center": v(-32.5, 956.96) * mm, "radius": 26.5 * mm});
            skCircle(sketch, "E516", {"center": v(0, 1013.25) * mm, "radius": 26.5 * mm});
            skCircle(sketch, "E517", {"center": v(97.5, 1182.12) * mm, "radius": 26.5 * mm});
            skCircle(sketch, "E518", {"center": v(130, 1238.42) * mm, "radius": 26.5 * mm});
            skCircle(sketch, "E519", {"center": v(162.5, 1294.7) * mm, "radius": 26.5 * mm});
            skCircle(sketch, "E520", {"center": v(195, 1351) * mm, "radius": 26.5 * mm});
            skCircle(sketch, "E521", {"center": v(227.5, 1407.3) * mm, "radius": 26.5 * mm});
            skCircle(sketch, "E522", {"center": v(260, 1463.58) * mm, "radius": 26.5 * mm});
            skCircle(sketch, "E523", {"center": v(292.5, 1519.87) * mm, "radius": 26.5 * mm});
            skCircle(sketch, "E524", {"center": v(-292.5, 619.2) * mm, "radius": 26.5 * mm});
            skCircle(sketch, "E525", {"center": v(-260, 675.5) * mm, "radius": 26.5 * mm});
            skCircle(sketch, "E526", {"center": v(-227.5, 731.8) * mm, "radius": 26.5 * mm});
            skCircle(sketch, "E527", {"center": v(-195, 788.08) * mm, "radius": 26.5 * mm});
            skCircle(sketch, "E528", {"center": v(-162.5, 844.37) * mm, "radius": 26.5 * mm});
            skCircle(sketch, "E529", {"center": v(-130, 900.67) * mm, "radius": 26.5 * mm});
            skCircle(sketch, "E530", {"center": v(-97.5, 956.96) * mm, "radius": 26.5 * mm});
            skCircle(sketch, "E531", {"center": v(-65, 1013.25) * mm, "radius": 26.5 * mm});
            skCircle(sketch, "E532", {"center": v(65, 1238.42) * mm, "radius": 26.5 * mm});
            skCircle(sketch, "E533", {"center": v(97.5, 1294.7) * mm, "radius": 26.5 * mm});
            skCircle(sketch, "E534", {"center": v(130, 1351) * mm, "radius": 26.5 * mm});
            skCircle(sketch, "E535", {"center": v(162.5, 1407.3) * mm, "radius": 26.5 * mm});
            skCircle(sketch, "E536", {"center": v(195, 1463.58) * mm, "radius": 26.5 * mm});
            skCircle(sketch, "E537", {"center": v(227.5, 1519.87) * mm, "radius": 26.5 * mm});
            skCircle(sketch, "E538", {"center": v(-325, 675.5) * mm, "radius": 26.5 * mm});
            skCircle(sketch, "E539", {"center": v(-292.5, 731.8) * mm, "radius": 26.5 * mm});
            skCircle(sketch, "E540", {"center": v(-260, 788.08) * mm, "radius": 26.5 * mm});
            skCircle(sketch, "E541", {"center": v(-227.5, 844.37) * mm, "radius": 26.5 * mm});
            skCircle(sketch, "E542", {"center": v(-195, 900.67) * mm, "radius": 26.5 * mm});
            skCircle(sketch, "E543", {"center": v(-162.5, 956.96) * mm, "radius": 26.5 * mm});
            skCircle(sketch, "E544", {"center": v(-130, 1013.25) * mm, "radius": 26.5 * mm});
            skCircle(sketch, "E545", {"center": v(-97.5, 1069.54) * mm, "radius": 26.5 * mm});
            skCircle(sketch, "E546", {"center": v(0, 1238.42) * mm, "radius": 26.5 * mm});
            skCircle(sketch, "E547", {"center": v(32.5, 1294.7) * mm, "radius": 26.5 * mm});
            skCircle(sketch, "E548", {"center": v(65, 1351) * mm, "radius": 26.5 * mm});
            skCircle(sketch, "E549", {"center": v(97.5, 1407.3) * mm, "radius": 26.5 * mm});
            skCircle(sketch, "E550", {"center": v(130, 1463.58) * mm, "radius": 26.5 * mm});
            skCircle(sketch, "E551", {"center": v(162.5, 1519.87) * mm, "radius": 26.5 * mm});
            skCircle(sketch, "E552", {"center": v(-357.5, 731.8) * mm, "radius": 26.5 * mm});
            skCircle(sketch, "E553", {"center": v(-325, 788.08) * mm, "radius": 26.5 * mm});
            skCircle(sketch, "E554", {"center": v(-292.5, 844.37) * mm, "radius": 26.5 * mm});
            skCircle(sketch, "E555", {"center": v(-260, 900.67) * mm, "radius": 26.5 * mm});
            skCircle(sketch, "E556", {"center": v(-227.5, 956.96) * mm, "radius": 26.5 * mm});
            skCircle(sketch, "E557", {"center": v(-195, 1013.25) * mm, "radius": 26.5 * mm});
            skCircle(sketch, "E558", {"center": v(-162.5, 1069.54) * mm, "radius": 26.5 * mm});
            skCircle(sketch, "E559", {"center": v(-130, 1125.83) * mm, "radius": 26.5 * mm});
            skCircle(sketch, "E560", {"center": v(-97.5, 1182.12) * mm, "radius": 26.5 * mm});
            skCircle(sketch, "E561", {"center": v(-65, 1238.42) * mm, "radius": 26.5 * mm});
            skCircle(sketch, "E562", {"center": v(-32.5, 1294.7) * mm, "radius": 26.5 * mm});
            skCircle(sketch, "E563", {"center": v(0, 1351) * mm, "radius": 26.5 * mm});
            skCircle(sketch, "E564", {"center": v(32.5, 1407.3) * mm, "radius": 26.5 * mm});
            skCircle(sketch, "E565", {"center": v(65, 1463.58) * mm, "radius": 26.5 * mm});
            skCircle(sketch, "E566", {"center": v(97.5, 1519.87) * mm, "radius": 26.5 * mm});
            skCircle(sketch, "E567", {"center": v(-390, 788.08) * mm, "radius": 26.5 * mm});
            skCircle(sketch, "E568", {"center": v(-357.5, 844.37) * mm, "radius": 26.5 * mm});
            skCircle(sketch, "E569", {"center": v(-325, 900.67) * mm, "radius": 26.5 * mm});
            skCircle(sketch, "E570", {"center": v(-292.5, 956.96) * mm, "radius": 26.5 * mm});
            skCircle(sketch, "E571", {"center": v(-260, 1013.25) * mm, "radius": 26.5 * mm});
            skCircle(sketch, "E572", {"center": v(-227.5, 1069.54) * mm, "radius": 26.5 * mm});
            skCircle(sketch, "E573", {"center": v(-195, 1125.83) * mm, "radius": 26.5 * mm});
            skCircle(sketch, "E574", {"center": v(-162.5, 1182.12) * mm, "radius": 26.5 * mm});
            skCircle(sketch, "E575", {"center": v(-130, 1238.42) * mm, "radius": 26.5 * mm});
            skCircle(sketch, "E576", {"center": v(-97.5, 1294.7) * mm, "radius": 26.5 * mm});
            skCircle(sketch, "E577", {"center": v(-65, 1351) * mm, "radius": 26.5 * mm});
            skCircle(sketch, "E578", {"center": v(-32.5, 1407.3) * mm, "radius": 26.5 * mm});
            skCircle(sketch, "E579", {"center": v(0, 1463.58) * mm, "radius": 26.5 * mm});
            skCircle(sketch, "E580", {"center": v(32.5, 1519.87) * mm, "radius": 26.5 * mm});
            skCircle(sketch, "E581", {"center": v(65, 1576.17) * mm, "radius": 26.5 * mm});
            skCircle(sketch, "E582", {"center": v(-422.5, 844.37) * mm, "radius": 26.5 * mm});
            skCircle(sketch, "E583", {"center": v(-390, 900.67) * mm, "radius": 26.5 * mm});
            skCircle(sketch, "E584", {"center": v(-357.5, 956.96) * mm, "radius": 26.5 * mm});
            skCircle(sketch, "E585", {"center": v(-325, 1013.25) * mm, "radius": 26.5 * mm});
            skCircle(sketch, "E586", {"center": v(-292.5, 1069.54) * mm, "radius": 26.5 * mm});
            skCircle(sketch, "E587", {"center": v(-260, 1125.83) * mm, "radius": 26.5 * mm});
            skCircle(sketch, "E588", {"center": v(-227.5, 1182.12) * mm, "radius": 26.5 * mm});
            skCircle(sketch, "E589", {"center": v(-195, 1238.42) * mm, "radius": 26.5 * mm});
            skCircle(sketch, "E590", {"center": v(-162.5, 1294.7) * mm, "radius": 26.5 * mm});
            skCircle(sketch, "E591", {"center": v(-130, 1351) * mm, "radius": 26.5 * mm});
            skCircle(sketch, "E592", {"center": v(-97.5, 1407.3) * mm, "radius": 26.5 * mm});
            skCircle(sketch, "E593", {"center": v(-65, 1463.58) * mm, "radius": 26.5 * mm});
            skCircle(sketch, "E594", {"center": v(-32.5, 1519.87) * mm, "radius": 26.5 * mm});
            skCircle(sketch, "E595", {"center": v(0, 1576.17) * mm, "radius": 26.5 * mm});
            skCircle(sketch, "E596", {"center": v(-455, 900.67) * mm, "radius": 26.5 * mm});
            skCircle(sketch, "E597", {"center": v(-422.5, 956.96) * mm, "radius": 26.5 * mm});
            skCircle(sketch, "E598", {"center": v(-390, 1013.25) * mm, "radius": 26.5 * mm});
            skCircle(sketch, "E599", {"center": v(-357.5, 1069.54) * mm, "radius": 26.5 * mm});
            skCircle(sketch, "E600", {"center": v(-325, 1125.83) * mm, "radius": 26.5 * mm});
            skCircle(sketch, "E601", {"center": v(-292.5, 1182.12) * mm, "radius": 26.5 * mm});
            skCircle(sketch, "E602", {"center": v(-260, 1238.42) * mm, "radius": 26.5 * mm});
            skCircle(sketch, "E603", {"center": v(-227.5, 1294.7) * mm, "radius": 26.5 * mm});
            skCircle(sketch, "E604", {"center": v(-195, 1351) * mm, "radius": 26.5 * mm});
            skCircle(sketch, "E605", {"center": v(-162.5, 1407.3) * mm, "radius": 26.5 * mm});
            skCircle(sketch, "E606", {"center": v(-130, 1463.58) * mm, "radius": 26.5 * mm});
            skCircle(sketch, "E607", {"center": v(-97.5, 1519.87) * mm, "radius": 26.5 * mm});
            skCircle(sketch, "E608", {"center": v(-65, 1576.17) * mm, "radius": 26.5 * mm});
            skCircle(sketch, "E609", {"center": v(-487.5, 956.96) * mm, "radius": 26.5 * mm});
            skCircle(sketch, "E610", {"center": v(-455, 1013.25) * mm, "radius": 26.5 * mm});
            skCircle(sketch, "E611", {"center": v(-422.5, 1069.54) * mm, "radius": 26.5 * mm});
            skCircle(sketch, "E612", {"center": v(-390, 1125.83) * mm, "radius": 26.5 * mm});
            skCircle(sketch, "E613", {"center": v(-357.5, 1182.12) * mm, "radius": 26.5 * mm});
            skCircle(sketch, "E614", {"center": v(-325, 1238.42) * mm, "radius": 26.5 * mm});
            skCircle(sketch, "E615", {"center": v(-292.5, 1294.7) * mm, "radius": 26.5 * mm});
            skCircle(sketch, "E616", {"center": v(-260, 1351) * mm, "radius": 26.5 * mm});
            skCircle(sketch, "E617", {"center": v(-227.5, 1407.3) * mm, "radius": 26.5 * mm});
            skCircle(sketch, "E618", {"center": v(-195, 1463.58) * mm, "radius": 26.5 * mm});
            skCircle(sketch, "E619", {"center": v(-162.5, 1519.87) * mm, "radius": 26.5 * mm});
            skCircle(sketch, "E620", {"center": v(-520, 1013.25) * mm, "radius": 26.5 * mm});
            skCircle(sketch, "E621", {"center": v(-487.5, 1069.54) * mm, "radius": 26.5 * mm});
            skCircle(sketch, "E622", {"center": v(-455, 1125.83) * mm, "radius": 26.5 * mm});
            skCircle(sketch, "E623", {"center": v(-422.5, 1182.12) * mm, "radius": 26.5 * mm});
            skCircle(sketch, "E624", {"center": v(-390, 1238.42) * mm, "radius": 26.5 * mm});
            skCircle(sketch, "E625", {"center": v(-357.5, 1294.7) * mm, "radius": 26.5 * mm});
            skCircle(sketch, "E626", {"center": v(-325, 1351) * mm, "radius": 26.5 * mm});
            skCircle(sketch, "E627", {"center": v(-292.5, 1407.3) * mm, "radius": 26.5 * mm});
            skCircle(sketch, "E628", {"center": v(-260, 1463.58) * mm, "radius": 26.5 * mm});
            skCircle(sketch, "E629", {"center": v(-227.5, 1519.87) * mm, "radius": 26.5 * mm});
            skCircle(sketch, "E630", {"center": v(-552.5, 1069.54) * mm, "radius": 26.5 * mm});
            skCircle(sketch, "E631", {"center": v(-520, 1125.83) * mm, "radius": 26.5 * mm});
            skCircle(sketch, "E632", {"center": v(-487.5, 1182.12) * mm, "radius": 26.5 * mm});
            skCircle(sketch, "E633", {"center": v(-455, 1238.42) * mm, "radius": 26.5 * mm});
            skCircle(sketch, "E634", {"center": v(-422.5, 1294.7) * mm, "radius": 26.5 * mm});
            skCircle(sketch, "E635", {"center": v(-390, 1351) * mm, "radius": 26.5 * mm});
            skCircle(sketch, "E636", {"center": v(-357.5, 1407.3) * mm, "radius": 26.5 * mm});
            skCircle(sketch, "E637", {"center": v(-325, 1463.58) * mm, "radius": 26.5 * mm});
            skCircle(sketch, "E638", {"center": v(-292.5, 1519.87) * mm, "radius": 26.5 * mm});
            skCircle(sketch, "E639", {"center": v(-585, 1125.83) * mm, "radius": 26.5 * mm});
            skCircle(sketch, "E640", {"center": v(-552.5, 1182.12) * mm, "radius": 26.5 * mm});
            skCircle(sketch, "E641", {"center": v(-520, 1238.42) * mm, "radius": 26.5 * mm});
            skCircle(sketch, "E642", {"center": v(-487.5, 1294.7) * mm, "radius": 26.5 * mm});
            skCircle(sketch, "E643", {"center": v(-455, 1351) * mm, "radius": 26.5 * mm});
            skCircle(sketch, "E644", {"center": v(-422.5, 1407.3) * mm, "radius": 26.5 * mm});
            skCircle(sketch, "E645", {"center": v(-390, 1463.58) * mm, "radius": 26.5 * mm});
            skCircle(sketch, "E646", {"center": v(-357.5, 1519.87) * mm, "radius": 26.5 * mm});
            skCircle(sketch, "E647", {"center": v(-617.5, 1182.12) * mm, "radius": 26.5 * mm});
            skCircle(sketch, "E648", {"center": v(-585, 1238.42) * mm, "radius": 26.5 * mm});
            skCircle(sketch, "E649", {"center": v(-552.5, 1294.7) * mm, "radius": 26.5 * mm});
            skCircle(sketch, "E650", {"center": v(-520, 1351) * mm, "radius": 26.5 * mm});
            skCircle(sketch, "E651", {"center": v(-487.5, 1407.3) * mm, "radius": 26.5 * mm});
            skCircle(sketch, "E652", {"center": v(-455, 1463.58) * mm, "radius": 26.5 * mm});
            skCircle(sketch, "E653", {"center": v(-422.5, 1519.87) * mm, "radius": 26.5 * mm});
            skCircle(sketch, "E654", {"center": v(-650, 1238.42) * mm, "radius": 26.5 * mm});
            skCircle(sketch, "E655", {"center": v(-617.5, 1294.7) * mm, "radius": 26.5 * mm});
            skCircle(sketch, "E656", {"center": v(-585, 1351) * mm, "radius": 26.5 * mm});
            skCircle(sketch, "E657", {"center": v(-552.5, 1407.3) * mm, "radius": 26.5 * mm});
            skCircle(sketch, "E658", {"center": v(-520, 1463.58) * mm, "radius": 26.5 * mm});
            skCircle(sketch, "E659", {"center": v(-682.5, 1294.7) * mm, "radius": 26.5 * mm});
            skCircle(sketch, "E660", {"center": v(-650, 1351) * mm, "radius": 26.5 * mm});
            skCircle(sketch, "E661", {"center": v(-617.5, 1407.3) * mm, "radius": 26.5 * mm});
            skCircle(sketch, "E662", {"center": v(-585, 1463.58) * mm, "radius": 26.5 * mm});
            skCircle(sketch, "E663", {"center": v(-715, 1351) * mm, "radius": 26.5 * mm});
            skCircle(sketch, "E664", {"center": v(-682.5, 1407.3) * mm, "radius": 26.5 * mm});
            skCircle(sketch, "E665", {"center": v(0, 1125.83) * mm, "radius": 58 * mm});
            skCircle(sketch, "E666", {"center": v(-195, 337.75) * mm, "radius": 26.5 * mm});
            skCircle(sketch, "E667", {"center": v(-227.5, 394.04) * mm, "radius": 26.5 * mm});
            skCircle(sketch, "E668", {"center": v(-260, 450.33) * mm, "radius": 26.5 * mm});
            skCircle(sketch, "E669", {"center": v(-292.5, 506.62) * mm, "radius": 26.5 * mm});
            skCircle(sketch, "E670", {"center": v(-325, 562.92) * mm, "radius": 26.5 * mm});
            skCircle(sketch, "E671", {"center": v(-357.5, 619.2) * mm, "radius": 26.5 * mm});
            skCircle(sketch, "E672", {"center": v(-390, 675.5) * mm, "radius": 26.5 * mm});
            skCircle(sketch, "E673", {"center": v(-422.5, 731.8) * mm, "radius": 26.5 * mm});
            skCircle(sketch, "E674", {"center": v(-455, 788.08) * mm, "radius": 26.5 * mm});
            skCircle(sketch, "E675", {"center": v(-487.5, 844.37) * mm, "radius": 26.5 * mm});
            skCircle(sketch, "E676", {"center": v(-520, 900.67) * mm, "radius": 26.5 * mm});
            skCircle(sketch, "E677", {"center": v(-552.5, 956.96) * mm, "radius": 26.5 * mm});
            skCircle(sketch, "E678", {"center": v(-585, 1013.25) * mm, "radius": 26.5 * mm});
            skCircle(sketch, "E679", {"center": v(-617.5, 1069.54) * mm, "radius": 26.5 * mm});
            skCircle(sketch, "E680", {"center": v(-650, 1125.83) * mm, "radius": 26.5 * mm});
            skCircle(sketch, "E681", {"center": v(-682.5, 1182.12) * mm, "radius": 26.5 * mm});
            skCircle(sketch, "E682", {"center": v(-715, 1238.42) * mm, "radius": 26.5 * mm});
            skCircle(sketch, "E683", {"center": v(-747.5, 1294.7) * mm, "radius": 26.5 * mm});
            skCircle(sketch, "E684", {"center": v(-780, 1351) * mm, "radius": 26.5 * mm});
            skCircle(sketch, "E685", {"center": v(-260, 337.75) * mm, "radius": 26.5 * mm});
            skCircle(sketch, "E686", {"center": v(-292.5, 394.04) * mm, "radius": 26.5 * mm});
            skCircle(sketch, "E687", {"center": v(-325, 450.33) * mm, "radius": 26.5 * mm});
            skCircle(sketch, "E688", {"center": v(-357.5, 506.62) * mm, "radius": 26.5 * mm});
            skCircle(sketch, "E689", {"center": v(-390, 562.92) * mm, "radius": 26.5 * mm});
            skCircle(sketch, "E690", {"center": v(-422.5, 619.2) * mm, "radius": 26.5 * mm});
            skCircle(sketch, "E691", {"center": v(-455, 675.5) * mm, "radius": 26.5 * mm});
            skCircle(sketch, "E692", {"center": v(-487.5, 731.8) * mm, "radius": 26.5 * mm});
            skCircle(sketch, "E693", {"center": v(-520, 788.08) * mm, "radius": 26.5 * mm});
            skCircle(sketch, "E694", {"center": v(-552.5, 844.37) * mm, "radius": 26.5 * mm});
            skCircle(sketch, "E695", {"center": v(-585, 900.67) * mm, "radius": 26.5 * mm});
            skCircle(sketch, "E696", {"center": v(-617.5, 956.96) * mm, "radius": 26.5 * mm});
            skCircle(sketch, "E697", {"center": v(-650, 1013.25) * mm, "radius": 26.5 * mm});
            skCircle(sketch, "E698", {"center": v(-682.5, 1069.54) * mm, "radius": 26.5 * mm});
            skCircle(sketch, "E699", {"center": v(-715, 1125.83) * mm, "radius": 26.5 * mm});
            skCircle(sketch, "E700", {"center": v(-747.5, 1182.12) * mm, "radius": 26.5 * mm});
            skCircle(sketch, "E701", {"center": v(-780, 1238.42) * mm, "radius": 26.5 * mm});
            skCircle(sketch, "E702", {"center": v(-812.5, 1294.7) * mm, "radius": 26.5 * mm});
            skCircle(sketch, "E703", {"center": v(-292.5, 281.46) * mm, "radius": 26.5 * mm});
            skCircle(sketch, "E704", {"center": v(-325, 337.75) * mm, "radius": 26.5 * mm});
            skCircle(sketch, "E705", {"center": v(-357.5, 394.04) * mm, "radius": 26.5 * mm});
            skCircle(sketch, "E706", {"center": v(-390, 450.33) * mm, "radius": 26.5 * mm});
            skCircle(sketch, "E707", {"center": v(-422.5, 506.62) * mm, "radius": 26.5 * mm});
            skCircle(sketch, "E708", {"center": v(-455, 562.92) * mm, "radius": 26.5 * mm});
            skCircle(sketch, "E709", {"center": v(-487.5, 619.2) * mm, "radius": 26.5 * mm});
            skCircle(sketch, "E710", {"center": v(-520, 675.5) * mm, "radius": 26.5 * mm});
            skCircle(sketch, "E711", {"center": v(-552.5, 731.8) * mm, "radius": 26.5 * mm});
            skCircle(sketch, "E712", {"center": v(-585, 788.08) * mm, "radius": 26.5 * mm});
            skCircle(sketch, "E713", {"center": v(-617.5, 844.37) * mm, "radius": 26.5 * mm});
            skCircle(sketch, "E714", {"center": v(-650, 900.67) * mm, "radius": 26.5 * mm});
            skCircle(sketch, "E715", {"center": v(-682.5, 956.96) * mm, "radius": 26.5 * mm});
            skCircle(sketch, "E716", {"center": v(-715, 1013.25) * mm, "radius": 26.5 * mm});
            skCircle(sketch, "E717", {"center": v(-747.5, 1069.54) * mm, "radius": 26.5 * mm});
            skCircle(sketch, "E718", {"center": v(-780, 1125.83) * mm, "radius": 26.5 * mm});
            skCircle(sketch, "E719", {"center": v(-812.5, 1182.12) * mm, "radius": 26.5 * mm});
            skCircle(sketch, "E720", {"center": v(-845, 1238.42) * mm, "radius": 26.5 * mm});
            skCircle(sketch, "E721", {"center": v(-877.5, 1294.7) * mm, "radius": 26.5 * mm});
            skCircle(sketch, "E722", {"center": v(-325, 225.17) * mm, "radius": 26.5 * mm});
            skCircle(sketch, "E723", {"center": v(-357.5, 281.46) * mm, "radius": 26.5 * mm});
            skCircle(sketch, "E724", {"center": v(-390, 337.75) * mm, "radius": 26.5 * mm});
            skCircle(sketch, "E725", {"center": v(-422.5, 394.04) * mm, "radius": 26.5 * mm});
            skCircle(sketch, "E726", {"center": v(-455, 450.33) * mm, "radius": 26.5 * mm});
            skCircle(sketch, "E727", {"center": v(-487.5, 506.62) * mm, "radius": 26.5 * mm});
            skCircle(sketch, "E728", {"center": v(-520, 562.92) * mm, "radius": 26.5 * mm});
            skCircle(sketch, "E729", {"center": v(-552.5, 619.2) * mm, "radius": 26.5 * mm});
            skCircle(sketch, "E730", {"center": v(-585, 675.5) * mm, "radius": 26.5 * mm});
            skCircle(sketch, "E731", {"center": v(-617.5, 731.8) * mm, "radius": 26.5 * mm});
            skCircle(sketch, "E732", {"center": v(-650, 788.08) * mm, "radius": 26.5 * mm});
            skCircle(sketch, "E733", {"center": v(-682.5, 844.37) * mm, "radius": 26.5 * mm});
            skCircle(sketch, "E734", {"center": v(-715, 900.67) * mm, "radius": 26.5 * mm});
            skCircle(sketch, "E735", {"center": v(-747.5, 956.96) * mm, "radius": 26.5 * mm});
            skCircle(sketch, "E736", {"center": v(-780, 1013.25) * mm, "radius": 26.5 * mm});
            skCircle(sketch, "E737", {"center": v(-812.5, 1069.54) * mm, "radius": 26.5 * mm});
            skCircle(sketch, "E738", {"center": v(-845, 1125.83) * mm, "radius": 26.5 * mm});
            skCircle(sketch, "E739", {"center": v(-877.5, 1182.12) * mm, "radius": 26.5 * mm});
            skCircle(sketch, "E740", {"center": v(-910, 1238.42) * mm, "radius": 26.5 * mm});
            skCircle(sketch, "E741", {"center": v(-357.5, 168.87) * mm, "radius": 26.5 * mm});
            skCircle(sketch, "E742", {"center": v(-390, 225.17) * mm, "radius": 26.5 * mm});
            skCircle(sketch, "E743", {"center": v(-422.5, 281.46) * mm, "radius": 26.5 * mm});
            skCircle(sketch, "E744", {"center": v(-455, 337.75) * mm, "radius": 26.5 * mm});
            skCircle(sketch, "E745", {"center": v(-487.5, 394.04) * mm, "radius": 26.5 * mm});
            skCircle(sketch, "E746", {"center": v(-520, 450.33) * mm, "radius": 26.5 * mm});
            skCircle(sketch, "E747", {"center": v(-552.5, 506.62) * mm, "radius": 26.5 * mm});
            skCircle(sketch, "E748", {"center": v(-585, 562.92) * mm, "radius": 26.5 * mm});
            skCircle(sketch, "E749", {"center": v(-617.5, 619.2) * mm, "radius": 26.5 * mm});
            skCircle(sketch, "E750", {"center": v(-650, 675.5) * mm, "radius": 26.5 * mm});
            skCircle(sketch, "E751", {"center": v(-682.5, 731.8) * mm, "radius": 26.5 * mm});
            skCircle(sketch, "E752", {"center": v(-715, 788.08) * mm, "radius": 26.5 * mm});
            skCircle(sketch, "E753", {"center": v(-747.5, 844.37) * mm, "radius": 26.5 * mm});
            skCircle(sketch, "E754", {"center": v(-780, 900.67) * mm, "radius": 26.5 * mm});
            skCircle(sketch, "E755", {"center": v(-812.5, 956.96) * mm, "radius": 26.5 * mm});
            skCircle(sketch, "E756", {"center": v(-845, 1013.25) * mm, "radius": 26.5 * mm});
            skCircle(sketch, "E757", {"center": v(-877.5, 1069.54) * mm, "radius": 26.5 * mm});
            skCircle(sketch, "E758", {"center": v(-910, 1125.83) * mm, "radius": 26.5 * mm});
            skCircle(sketch, "E759", {"center": v(-942.5, 1182.12) * mm, "radius": 26.5 * mm});
            skCircle(sketch, "E760", {"center": v(-975, 1238.42) * mm, "radius": 26.5 * mm});
            skCircle(sketch, "E761", {"center": v(-390, 112.58) * mm, "radius": 26.5 * mm});
            skCircle(sketch, "E762", {"center": v(-422.5, 168.87) * mm, "radius": 26.5 * mm});
            skCircle(sketch, "E763", {"center": v(-455, 225.17) * mm, "radius": 26.5 * mm});
            skCircle(sketch, "E764", {"center": v(-487.5, 281.46) * mm, "radius": 26.5 * mm});
            skCircle(sketch, "E765", {"center": v(-520, 337.75) * mm, "radius": 26.5 * mm});
            skCircle(sketch, "E766", {"center": v(-552.5, 394.04) * mm, "radius": 26.5 * mm});
            skCircle(sketch, "E767", {"center": v(-585, 450.33) * mm, "radius": 26.5 * mm});
            skCircle(sketch, "E768", {"center": v(-617.5, 506.62) * mm, "radius": 26.5 * mm});
            skCircle(sketch, "E769", {"center": v(-650, 562.92) * mm, "radius": 26.5 * mm});
            skCircle(sketch, "E770", {"center": v(-682.5, 619.2) * mm, "radius": 26.5 * mm});
            skCircle(sketch, "E771", {"center": v(-715, 675.5) * mm, "radius": 26.5 * mm});
            skCircle(sketch, "E772", {"center": v(-747.5, 731.8) * mm, "radius": 26.5 * mm});
            skCircle(sketch, "E773", {"center": v(-780, 788.08) * mm, "radius": 26.5 * mm});
            skCircle(sketch, "E774", {"center": v(-812.5, 844.37) * mm, "radius": 26.5 * mm});
            skCircle(sketch, "E775", {"center": v(-845, 900.67) * mm, "radius": 26.5 * mm});
            skCircle(sketch, "E776", {"center": v(-877.5, 956.96) * mm, "radius": 26.5 * mm});
            skCircle(sketch, "E777", {"center": v(-910, 1013.25) * mm, "radius": 26.5 * mm});
            skCircle(sketch, "E778", {"center": v(-942.5, 1069.54) * mm, "radius": 26.5 * mm});
            skCircle(sketch, "E779", {"center": v(-975, 1125.83) * mm, "radius": 26.5 * mm});
            skCircle(sketch, "E780", {"center": v(-1007.5, 1182.12) * mm, "radius": 26.5 * mm});
            skCircle(sketch, "E781", {"center": v(-422.5, 56.3) * mm, "radius": 26.5 * mm});
            skCircle(sketch, "E782", {"center": v(-455, 112.58) * mm, "radius": 26.5 * mm});
            skCircle(sketch, "E783", {"center": v(-487.5, 168.87) * mm, "radius": 26.5 * mm});
            skCircle(sketch, "E784", {"center": v(-520, 225.17) * mm, "radius": 26.5 * mm});
            skCircle(sketch, "E785", {"center": v(-552.5, 281.46) * mm, "radius": 26.5 * mm});
            skCircle(sketch, "E786", {"center": v(-585, 337.75) * mm, "radius": 26.5 * mm});
            skCircle(sketch, "E787", {"center": v(-617.5, 394.04) * mm, "radius": 26.5 * mm});
            skCircle(sketch, "E788", {"center": v(-650, 450.33) * mm, "radius": 26.5 * mm});
            skCircle(sketch, "E789", {"center": v(-682.5, 506.62) * mm, "radius": 26.5 * mm});
            skCircle(sketch, "E790", {"center": v(-715, 562.92) * mm, "radius": 26.5 * mm});
            skCircle(sketch, "E791", {"center": v(-747.5, 619.2) * mm, "radius": 26.5 * mm});
            skCircle(sketch, "E792", {"center": v(-780, 675.5) * mm, "radius": 26.5 * mm});
            skCircle(sketch, "E793", {"center": v(-812.5, 731.8) * mm, "radius": 26.5 * mm});
            skCircle(sketch, "E794", {"center": v(-845, 788.08) * mm, "radius": 26.5 * mm});
            skCircle(sketch, "E795", {"center": v(-877.5, 844.37) * mm, "radius": 26.5 * mm});
            skCircle(sketch, "E796", {"center": v(-910, 900.67) * mm, "radius": 26.5 * mm});
            skCircle(sketch, "E797", {"center": v(-942.5, 956.96) * mm, "radius": 26.5 * mm});
            skCircle(sketch, "E798", {"center": v(-975, 1013.25) * mm, "radius": 26.5 * mm});
            skCircle(sketch, "E799", {"center": v(-1007.5, 1069.54) * mm, "radius": 26.5 * mm});
            skCircle(sketch, "E800", {"center": v(-1040, 1125.83) * mm, "radius": 26.5 * mm});
            skCircle(sketch, "E801", {"center": v(-487.5, 56.3) * mm, "radius": 26.5 * mm});
            skCircle(sketch, "E802", {"center": v(-520, 112.58) * mm, "radius": 26.5 * mm});
            skCircle(sketch, "E803", {"center": v(-552.5, 168.87) * mm, "radius": 26.5 * mm});
            skCircle(sketch, "E804", {"center": v(-585, 225.17) * mm, "radius": 26.5 * mm});
            skCircle(sketch, "E805", {"center": v(-617.5, 281.46) * mm, "radius": 26.5 * mm});
            skCircle(sketch, "E806", {"center": v(-650, 337.75) * mm, "radius": 26.5 * mm});
            skCircle(sketch, "E807", {"center": v(-682.5, 394.04) * mm, "radius": 26.5 * mm});
            skCircle(sketch, "E808", {"center": v(-715, 450.33) * mm, "radius": 26.5 * mm});
            skCircle(sketch, "E809", {"center": v(-747.5, 506.62) * mm, "radius": 26.5 * mm});
            skCircle(sketch, "E810", {"center": v(-780, 562.92) * mm, "radius": 26.5 * mm});
            skCircle(sketch, "E811", {"center": v(-812.5, 619.2) * mm, "radius": 26.5 * mm});
            skCircle(sketch, "E812", {"center": v(-845, 675.5) * mm, "radius": 26.5 * mm});
            skCircle(sketch, "E813", {"center": v(-877.5, 731.8) * mm, "radius": 26.5 * mm});
            skCircle(sketch, "E814", {"center": v(-910, 788.08) * mm, "radius": 26.5 * mm});
            skCircle(sketch, "E815", {"center": v(-942.5, 844.37) * mm, "radius": 26.5 * mm});
            skCircle(sketch, "E816", {"center": v(-975, 900.67) * mm, "radius": 26.5 * mm});
            skCircle(sketch, "E817", {"center": v(-1007.5, 956.96) * mm, "radius": 26.5 * mm});
            skCircle(sketch, "E818", {"center": v(-1040, 1013.25) * mm, "radius": 26.5 * mm});
            skCircle(sketch, "E819", {"center": v(-1072.5, 1069.54) * mm, "radius": 26.5 * mm});
            skCircle(sketch, "E820", {"center": v(-1105, 1125.83) * mm, "radius": 26.5 * mm});
            skCircle(sketch, "E821", {"center": v(-552.5, 56.3) * mm, "radius": 26.5 * mm});
            skCircle(sketch, "E822", {"center": v(-585, 112.58) * mm, "radius": 26.5 * mm});
            skCircle(sketch, "E823", {"center": v(-617.5, 168.87) * mm, "radius": 26.5 * mm});
            skCircle(sketch, "E824", {"center": v(-650, 225.17) * mm, "radius": 26.5 * mm});
            skCircle(sketch, "E825", {"center": v(-682.5, 281.46) * mm, "radius": 26.5 * mm});
            skCircle(sketch, "E826", {"center": v(-715, 337.75) * mm, "radius": 26.5 * mm});
            skCircle(sketch, "E827", {"center": v(-747.5, 394.04) * mm, "radius": 26.5 * mm});
            skCircle(sketch, "E828", {"center": v(-780, 450.33) * mm, "radius": 26.5 * mm});
            skCircle(sketch, "E829", {"center": v(-812.5, 506.62) * mm, "radius": 26.5 * mm});
            skCircle(sketch, "E830", {"center": v(-845, 562.92) * mm, "radius": 26.5 * mm});
            skCircle(sketch, "E831", {"center": v(-877.5, 619.2) * mm, "radius": 26.5 * mm});
            skCircle(sketch, "E832", {"center": v(-910, 675.5) * mm, "radius": 26.5 * mm});
            skCircle(sketch, "E833", {"center": v(-942.5, 731.8) * mm, "radius": 26.5 * mm});
            skCircle(sketch, "E834", {"center": v(-975, 788.08) * mm, "radius": 26.5 * mm});
            skCircle(sketch, "E835", {"center": v(-1007.5, 844.37) * mm, "radius": 26.5 * mm});
            skCircle(sketch, "E836", {"center": v(-1040, 900.67) * mm, "radius": 26.5 * mm});
            skCircle(sketch, "E837", {"center": v(-1072.5, 956.96) * mm, "radius": 26.5 * mm});
            skCircle(sketch, "E838", {"center": v(-1105, 1013.25) * mm, "radius": 26.5 * mm});
            skCircle(sketch, "E839", {"center": v(-1137.5, 1069.54) * mm, "radius": 26.5 * mm});
            skCircle(sketch, "E840", {"center": v(-617.5, 56.3) * mm, "radius": 26.5 * mm});
            skCircle(sketch, "E841", {"center": v(-650, 112.58) * mm, "radius": 26.5 * mm});
            skCircle(sketch, "E842", {"center": v(-682.5, 168.87) * mm, "radius": 26.5 * mm});
            skCircle(sketch, "E843", {"center": v(-715, 225.17) * mm, "radius": 26.5 * mm});
            skCircle(sketch, "E844", {"center": v(-747.5, 281.46) * mm, "radius": 26.5 * mm});
            skCircle(sketch, "E845", {"center": v(-780, 337.75) * mm, "radius": 26.5 * mm});
            skCircle(sketch, "E846", {"center": v(-812.5, 394.04) * mm, "radius": 26.5 * mm});
            skCircle(sketch, "E847", {"center": v(-845, 450.33) * mm, "radius": 26.5 * mm});
            skCircle(sketch, "E848", {"center": v(-877.5, 506.62) * mm, "radius": 26.5 * mm});
            skCircle(sketch, "E849", {"center": v(-975, 675.5) * mm, "radius": 26.5 * mm});
            skCircle(sketch, "E850", {"center": v(-1007.5, 731.8) * mm, "radius": 26.5 * mm});
            skCircle(sketch, "E851", {"center": v(-1040, 788.08) * mm, "radius": 26.5 * mm});
            skCircle(sketch, "E852", {"center": v(-1072.5, 844.37) * mm, "radius": 26.5 * mm});
            skCircle(sketch, "E853", {"center": v(-1105, 900.67) * mm, "radius": 26.5 * mm});
            skCircle(sketch, "E854", {"center": v(-1137.5, 956.96) * mm, "radius": 26.5 * mm});
            skCircle(sketch, "E855", {"center": v(-1170, 1013.25) * mm, "radius": 26.5 * mm});
            skCircle(sketch, "E856", {"center": v(-682.5, 56.3) * mm, "radius": 26.5 * mm});
            skCircle(sketch, "E857", {"center": v(-715, 112.58) * mm, "radius": 26.5 * mm});
            skCircle(sketch, "E858", {"center": v(-747.5, 168.87) * mm, "radius": 26.5 * mm});
            skCircle(sketch, "E859", {"center": v(-780, 225.17) * mm, "radius": 26.5 * mm});
            skCircle(sketch, "E860", {"center": v(-812.5, 281.46) * mm, "radius": 26.5 * mm});
            skCircle(sketch, "E861", {"center": v(-845, 337.75) * mm, "radius": 26.5 * mm});
            skCircle(sketch, "E862", {"center": v(-877.5, 394.04) * mm, "radius": 26.5 * mm});
            skCircle(sketch, "E863", {"center": v(-910, 450.33) * mm, "radius": 26.5 * mm});
            skCircle(sketch, "E864", {"center": v(-1040, 675.5) * mm, "radius": 26.5 * mm});
            skCircle(sketch, "E865", {"center": v(-1072.5, 731.8) * mm, "radius": 26.5 * mm});
            skCircle(sketch, "E866", {"center": v(-1105, 788.08) * mm, "radius": 26.5 * mm});
            skCircle(sketch, "E867", {"center": v(-1137.5, 844.37) * mm, "radius": 26.5 * mm});
            skCircle(sketch, "E868", {"center": v(-1170, 900.67) * mm, "radius": 26.5 * mm});
            skCircle(sketch, "E869", {"center": v(-1202.5, 956.96) * mm, "radius": 26.5 * mm});
            skCircle(sketch, "E870", {"center": v(-747.5, 56.3) * mm, "radius": 26.5 * mm});
            skCircle(sketch, "E871", {"center": v(-780, 112.58) * mm, "radius": 26.5 * mm});
            skCircle(sketch, "E872", {"center": v(-812.5, 168.87) * mm, "radius": 26.5 * mm});
            skCircle(sketch, "E873", {"center": v(-845, 225.17) * mm, "radius": 26.5 * mm});
            skCircle(sketch, "E874", {"center": v(-877.5, 281.46) * mm, "radius": 26.5 * mm});
            skCircle(sketch, "E875", {"center": v(-910, 337.75) * mm, "radius": 26.5 * mm});
            skCircle(sketch, "E876", {"center": v(-942.5, 394.04) * mm, "radius": 26.5 * mm});
            skCircle(sketch, "E877", {"center": v(-975, 450.33) * mm, "radius": 26.5 * mm});
            skCircle(sketch, "E878", {"center": v(-1072.5, 619.2) * mm, "radius": 26.5 * mm});
            skCircle(sketch, "E879", {"center": v(-1105, 675.5) * mm, "radius": 26.5 * mm});
            skCircle(sketch, "E880", {"center": v(-1137.5, 731.8) * mm, "radius": 26.5 * mm});
            skCircle(sketch, "E881", {"center": v(-1170, 788.08) * mm, "radius": 26.5 * mm});
            skCircle(sketch, "E882", {"center": v(-1202.5, 844.37) * mm, "radius": 26.5 * mm});
            skCircle(sketch, "E883", {"center": v(-1235, 900.67) * mm, "radius": 26.5 * mm});
            skCircle(sketch, "E884", {"center": v(-812.5, 56.3) * mm, "radius": 26.5 * mm});
            skCircle(sketch, "E885", {"center": v(-845, 112.58) * mm, "radius": 26.5 * mm});
            skCircle(sketch, "E886", {"center": v(-877.5, 168.87) * mm, "radius": 26.5 * mm});
            skCircle(sketch, "E887", {"center": v(-910, 225.17) * mm, "radius": 26.5 * mm});
            skCircle(sketch, "E888", {"center": v(-942.5, 281.46) * mm, "radius": 26.5 * mm});
            skCircle(sketch, "E889", {"center": v(-975, 337.75) * mm, "radius": 26.5 * mm});
            skCircle(sketch, "E890", {"center": v(-1007.5, 394.04) * mm, "radius": 26.5 * mm});
            skCircle(sketch, "E891", {"center": v(-1040, 450.33) * mm, "radius": 26.5 * mm});
            skCircle(sketch, "E892", {"center": v(-1072.5, 506.62) * mm, "radius": 26.5 * mm});
            skCircle(sketch, "E893", {"center": v(-1105, 562.92) * mm, "radius": 26.5 * mm});
            skCircle(sketch, "E894", {"center": v(-1137.5, 619.2) * mm, "radius": 26.5 * mm});
            skCircle(sketch, "E895", {"center": v(-1170, 675.5) * mm, "radius": 26.5 * mm});
            skCircle(sketch, "E896", {"center": v(-1202.5, 731.8) * mm, "radius": 26.5 * mm});
            skCircle(sketch, "E897", {"center": v(-1235, 788.08) * mm, "radius": 26.5 * mm});
            skCircle(sketch, "E898", {"center": v(-1267.5, 844.37) * mm, "radius": 26.5 * mm});
            skCircle(sketch, "E899", {"center": v(-877.5, 56.3) * mm, "radius": 26.5 * mm});
            skCircle(sketch, "E900", {"center": v(-910, 112.58) * mm, "radius": 26.5 * mm});
            skCircle(sketch, "E901", {"center": v(-942.5, 168.87) * mm, "radius": 26.5 * mm});
            skCircle(sketch, "E902", {"center": v(-975, 225.17) * mm, "radius": 26.5 * mm});
            skCircle(sketch, "E903", {"center": v(-1007.5, 281.46) * mm, "radius": 26.5 * mm});
            skCircle(sketch, "E904", {"center": v(-1040, 337.75) * mm, "radius": 26.5 * mm});
            skCircle(sketch, "E905", {"center": v(-1072.5, 394.04) * mm, "radius": 26.5 * mm});
            skCircle(sketch, "E906", {"center": v(-1105, 450.33) * mm, "radius": 26.5 * mm});
            skCircle(sketch, "E907", {"center": v(-1137.5, 506.62) * mm, "radius": 26.5 * mm});
            skCircle(sketch, "E908", {"center": v(-1170, 562.92) * mm, "radius": 26.5 * mm});
            skCircle(sketch, "E909", {"center": v(-1202.5, 619.2) * mm, "radius": 26.5 * mm});
            skCircle(sketch, "E910", {"center": v(-1235, 675.5) * mm, "radius": 26.5 * mm});
            skCircle(sketch, "E911", {"center": v(-1267.5, 731.8) * mm, "radius": 26.5 * mm});
            skCircle(sketch, "E912", {"center": v(-1300, 788.08) * mm, "radius": 26.5 * mm});
            skCircle(sketch, "E913", {"center": v(-1332.5, 844.37) * mm, "radius": 26.5 * mm});
            skCircle(sketch, "E914", {"center": v(-942.5, 56.3) * mm, "radius": 26.5 * mm});
            skCircle(sketch, "E915", {"center": v(-975, 112.58) * mm, "radius": 26.5 * mm});
            skCircle(sketch, "E916", {"center": v(-1007.5, 168.87) * mm, "radius": 26.5 * mm});
            skCircle(sketch, "E917", {"center": v(-1040, 225.17) * mm, "radius": 26.5 * mm});
            skCircle(sketch, "E918", {"center": v(-1072.5, 281.46) * mm, "radius": 26.5 * mm});
            skCircle(sketch, "E919", {"center": v(-1105, 337.75) * mm, "radius": 26.5 * mm});
            skCircle(sketch, "E920", {"center": v(-1137.5, 394.04) * mm, "radius": 26.5 * mm});
            skCircle(sketch, "E921", {"center": v(-1170, 450.33) * mm, "radius": 26.5 * mm});
            skCircle(sketch, "E922", {"center": v(-1202.5, 506.62) * mm, "radius": 26.5 * mm});
            skCircle(sketch, "E923", {"center": v(-1235, 562.92) * mm, "radius": 26.5 * mm});
            skCircle(sketch, "E924", {"center": v(-1267.5, 619.2) * mm, "radius": 26.5 * mm});
            skCircle(sketch, "E925", {"center": v(-1300, 675.5) * mm, "radius": 26.5 * mm});
            skCircle(sketch, "E926", {"center": v(-1332.5, 731.8) * mm, "radius": 26.5 * mm});
            skCircle(sketch, "E927", {"center": v(-1365, 788.08) * mm, "radius": 26.5 * mm});
            skCircle(sketch, "E928", {"center": v(-1007.5, 56.3) * mm, "radius": 26.5 * mm});
            skCircle(sketch, "E929", {"center": v(-1040, 112.58) * mm, "radius": 26.5 * mm});
            skCircle(sketch, "E930", {"center": v(-1072.5, 168.87) * mm, "radius": 26.5 * mm});
            skCircle(sketch, "E931", {"center": v(-1105, 225.17) * mm, "radius": 26.5 * mm});
            skCircle(sketch, "E932", {"center": v(-1137.5, 281.46) * mm, "radius": 26.5 * mm});
            skCircle(sketch, "E933", {"center": v(-1170, 337.75) * mm, "radius": 26.5 * mm});
            skCircle(sketch, "E934", {"center": v(-1202.5, 394.04) * mm, "radius": 26.5 * mm});
            skCircle(sketch, "E935", {"center": v(-1235, 450.33) * mm, "radius": 26.5 * mm});
            skCircle(sketch, "E936", {"center": v(-1267.5, 506.62) * mm, "radius": 26.5 * mm});
            skCircle(sketch, "E937", {"center": v(-1300, 562.92) * mm, "radius": 26.5 * mm});
            skCircle(sketch, "E938", {"center": v(-1332.5, 619.2) * mm, "radius": 26.5 * mm});
            skCircle(sketch, "E939", {"center": v(-1365, 675.5) * mm, "radius": 26.5 * mm});
            skCircle(sketch, "E940", {"center": v(-1397.5, 731.8) * mm, "radius": 26.5 * mm});
            skCircle(sketch, "E941", {"center": v(-1072.5, 56.3) * mm, "radius": 26.5 * mm});
            skCircle(sketch, "E942", {"center": v(-1105, 112.58) * mm, "radius": 26.5 * mm});
            skCircle(sketch, "E943", {"center": v(-1137.5, 168.87) * mm, "radius": 26.5 * mm});
            skCircle(sketch, "E944", {"center": v(-1170, 225.17) * mm, "radius": 26.5 * mm});
            skCircle(sketch, "E945", {"center": v(-1202.5, 281.46) * mm, "radius": 26.5 * mm});
            skCircle(sketch, "E946", {"center": v(-1235, 337.75) * mm, "radius": 26.5 * mm});
            skCircle(sketch, "E947", {"center": v(-1267.5, 394.04) * mm, "radius": 26.5 * mm});
            skCircle(sketch, "E948", {"center": v(-1300, 450.33) * mm, "radius": 26.5 * mm});
            skCircle(sketch, "E949", {"center": v(-1332.5, 506.62) * mm, "radius": 26.5 * mm});
            skCircle(sketch, "E950", {"center": v(-1365, 562.92) * mm, "radius": 26.5 * mm});
            skCircle(sketch, "E951", {"center": v(-1397.5, 619.2) * mm, "radius": 26.5 * mm});
            skCircle(sketch, "E952", {"center": v(-1137.5, 56.3) * mm, "radius": 26.5 * mm});
            skCircle(sketch, "E953", {"center": v(-1170, 112.58) * mm, "radius": 26.5 * mm});
            skCircle(sketch, "E954", {"center": v(-1202.5, 168.87) * mm, "radius": 26.5 * mm});
            skCircle(sketch, "E955", {"center": v(-1235, 225.17) * mm, "radius": 26.5 * mm});
            skCircle(sketch, "E956", {"center": v(-1267.5, 281.46) * mm, "radius": 26.5 * mm});
            skCircle(sketch, "E957", {"center": v(-1300, 337.75) * mm, "radius": 26.5 * mm});
            skCircle(sketch, "E958", {"center": v(-1332.5, 394.04) * mm, "radius": 26.5 * mm});
            skCircle(sketch, "E959", {"center": v(-1365, 450.33) * mm, "radius": 26.5 * mm});
            skCircle(sketch, "E960", {"center": v(-1397.5, 506.62) * mm, "radius": 26.5 * mm});
            skCircle(sketch, "E961", {"center": v(-1430, 562.92) * mm, "radius": 26.5 * mm});
            skCircle(sketch, "E962", {"center": v(-1202.5, 56.3) * mm, "radius": 26.5 * mm});
            skCircle(sketch, "E963", {"center": v(-1235, 112.58) * mm, "radius": 26.5 * mm});
            skCircle(sketch, "E964", {"center": v(-1267.5, 168.87) * mm, "radius": 26.5 * mm});
            skCircle(sketch, "E965", {"center": v(-1300, 225.17) * mm, "radius": 26.5 * mm});
            skCircle(sketch, "E966", {"center": v(-1332.5, 281.46) * mm, "radius": 26.5 * mm});
            skCircle(sketch, "E967", {"center": v(-1365, 337.75) * mm, "radius": 26.5 * mm});
            skCircle(sketch, "E968", {"center": v(-1397.5, 394.04) * mm, "radius": 26.5 * mm});
            skCircle(sketch, "E969", {"center": v(-1430, 450.33) * mm, "radius": 26.5 * mm});
            skCircle(sketch, "E970", {"center": v(-1462.5, 506.62) * mm, "radius": 26.5 * mm});
            skCircle(sketch, "E971", {"center": v(-1267.5, 56.3) * mm, "radius": 26.5 * mm});
            skCircle(sketch, "E972", {"center": v(-1300, 112.58) * mm, "radius": 26.5 * mm});
            skCircle(sketch, "E973", {"center": v(-1332.5, 168.87) * mm, "radius": 26.5 * mm});
            skCircle(sketch, "E974", {"center": v(-1365, 225.17) * mm, "radius": 26.5 * mm});
            skCircle(sketch, "E975", {"center": v(-1397.5, 281.46) * mm, "radius": 26.5 * mm});
            skCircle(sketch, "E976", {"center": v(-1430, 337.75) * mm, "radius": 26.5 * mm});
            skCircle(sketch, "E977", {"center": v(-1462.5, 394.04) * mm, "radius": 26.5 * mm});
            skCircle(sketch, "E978", {"center": v(-1495, 450.33) * mm, "radius": 26.5 * mm});
            skCircle(sketch, "E979", {"center": v(-1332.5, 56.3) * mm, "radius": 26.5 * mm});
            skCircle(sketch, "E980", {"center": v(-1365, 112.58) * mm, "radius": 26.5 * mm});
            skCircle(sketch, "E981", {"center": v(-1397.5, 168.87) * mm, "radius": 26.5 * mm});
            skCircle(sketch, "E982", {"center": v(-1430, 225.17) * mm, "radius": 26.5 * mm});
            skCircle(sketch, "E983", {"center": v(-1462.5, 281.46) * mm, "radius": 26.5 * mm});
            skCircle(sketch, "E984", {"center": v(-1495, 337.75) * mm, "radius": 26.5 * mm});
            skCircle(sketch, "E985", {"center": v(-1527.5, 394.04) * mm, "radius": 26.5 * mm});
            skCircle(sketch, "E986", {"center": v(-1397.5, 56.3) * mm, "radius": 26.5 * mm});
            skCircle(sketch, "E987", {"center": v(-1430, 112.58) * mm, "radius": 26.5 * mm});
            skCircle(sketch, "E988", {"center": v(-1462.5, 168.87) * mm, "radius": 26.5 * mm});
            skCircle(sketch, "E989", {"center": v(-1495, 225.17) * mm, "radius": 26.5 * mm});
            skCircle(sketch, "E990", {"center": v(-1527.5, 281.46) * mm, "radius": 26.5 * mm});
            skCircle(sketch, "E991", {"center": v(-1462.5, 56.3) * mm, "radius": 26.5 * mm});
            skCircle(sketch, "E992", {"center": v(-1495, 112.58) * mm, "radius": 26.5 * mm});
            skCircle(sketch, "E993", {"center": v(-1527.5, 168.87) * mm, "radius": 26.5 * mm});
            skCircle(sketch, "E994", {"center": v(-1560, 225.17) * mm, "radius": 26.5 * mm});
            skCircle(sketch, "E995", {"center": v(-1527.5, 56.3) * mm, "radius": 26.5 * mm});
            skCircle(sketch, "E996", {"center": v(-1560, 112.58) * mm, "radius": 26.5 * mm});
            skCircle(sketch, "E997", {"center": v(-975, 562.92) * mm, "radius": 58 * mm});
            skCircle(sketch, "E998", {"center": v(-390, 0) * mm, "radius": 26.5 * mm});
            skCircle(sketch, "E999", {"center": v(-455, 0) * mm, "radius": 26.5 * mm});
            skCircle(sketch, "E1000", {"center": v(-520, 0) * mm, "radius": 26.5 * mm});
            skCircle(sketch, "E1001", {"center": v(-585, 0) * mm, "radius": 26.5 * mm});
            skCircle(sketch, "E1002", {"center": v(-650, 0) * mm, "radius": 26.5 * mm});
            skCircle(sketch, "E1003", {"center": v(-715, 0) * mm, "radius": 26.5 * mm});
            skCircle(sketch, "E1004", {"center": v(-780, 0) * mm, "radius": 26.5 * mm});
            skCircle(sketch, "E1005", {"center": v(-845, 0) * mm, "radius": 26.5 * mm});
            skCircle(sketch, "E1006", {"center": v(-910, 0) * mm, "radius": 26.5 * mm});
            skCircle(sketch, "E1007", {"center": v(-975, 0) * mm, "radius": 26.5 * mm});
            skCircle(sketch, "E1008", {"center": v(-1040, 0) * mm, "radius": 26.5 * mm});
            skCircle(sketch, "E1009", {"center": v(-1105, 0) * mm, "radius": 26.5 * mm});
            skCircle(sketch, "E1010", {"center": v(-1170, 0) * mm, "radius": 26.5 * mm});
            skCircle(sketch, "E1011", {"center": v(-1235, 0) * mm, "radius": 26.5 * mm});
            skCircle(sketch, "E1012", {"center": v(-1300, 0) * mm, "radius": 26.5 * mm});
            skCircle(sketch, "E1013", {"center": v(-1365, 0) * mm, "radius": 26.5 * mm});
            skCircle(sketch, "E1014", {"center": v(-1430, 0) * mm, "radius": 26.5 * mm});
            skCircle(sketch, "E1015", {"center": v(-1495, 0) * mm, "radius": 26.5 * mm});
            skCircle(sketch, "E1016", {"center": v(-1560, 0) * mm, "radius": 26.5 * mm});
            skCircle(sketch, "E1017", {"center": v(-422.5, -56.3) * mm, "radius": 26.5 * mm});
            skCircle(sketch, "E1018", {"center": v(-487.5, -56.3) * mm, "radius": 26.5 * mm});
            skCircle(sketch, "E1019", {"center": v(-552.5, -56.3) * mm, "radius": 26.5 * mm});
            skCircle(sketch, "E1020", {"center": v(-617.5, -56.3) * mm, "radius": 26.5 * mm});
            skCircle(sketch, "E1021", {"center": v(-682.5, -56.3) * mm, "radius": 26.5 * mm});
            skCircle(sketch, "E1022", {"center": v(-747.5, -56.3) * mm, "radius": 26.5 * mm});
            skCircle(sketch, "E1023", {"center": v(-812.5, -56.3) * mm, "radius": 26.5 * mm});
            skCircle(sketch, "E1024", {"center": v(-877.5, -56.3) * mm, "radius": 26.5 * mm});
            skCircle(sketch, "E1025", {"center": v(-942.5, -56.3) * mm, "radius": 26.5 * mm});
            skCircle(sketch, "E1026", {"center": v(-1007.5, -56.3) * mm, "radius": 26.5 * mm});
            skCircle(sketch, "E1027", {"center": v(-1072.5, -56.3) * mm, "radius": 26.5 * mm});
            skCircle(sketch, "E1028", {"center": v(-1137.5, -56.3) * mm, "radius": 26.5 * mm});
            skCircle(sketch, "E1029", {"center": v(-1202.5, -56.3) * mm, "radius": 26.5 * mm});
            skCircle(sketch, "E1030", {"center": v(-1267.5, -56.3) * mm, "radius": 26.5 * mm});
            skCircle(sketch, "E1031", {"center": v(-1332.5, -56.3) * mm, "radius": 26.5 * mm});
            skCircle(sketch, "E1032", {"center": v(-1397.5, -56.3) * mm, "radius": 26.5 * mm});
            skCircle(sketch, "E1033", {"center": v(-1462.5, -56.3) * mm, "radius": 26.5 * mm});
            skCircle(sketch, "E1034", {"center": v(-1527.5, -56.3) * mm, "radius": 26.5 * mm});
            skCircle(sketch, "E1035", {"center": v(-390, -112.58) * mm, "radius": 26.5 * mm});
            skCircle(sketch, "E1036", {"center": v(-455, -112.58) * mm, "radius": 26.5 * mm});
            skCircle(sketch, "E1037", {"center": v(-520, -112.58) * mm, "radius": 26.5 * mm});
            skCircle(sketch, "E1038", {"center": v(-585, -112.58) * mm, "radius": 26.5 * mm});
            skCircle(sketch, "E1039", {"center": v(-650, -112.58) * mm, "radius": 26.5 * mm});
            skCircle(sketch, "E1040", {"center": v(-715, -112.58) * mm, "radius": 26.5 * mm});
            skCircle(sketch, "E1041", {"center": v(-780, -112.58) * mm, "radius": 26.5 * mm});
            skCircle(sketch, "E1042", {"center": v(-845, -112.58) * mm, "radius": 26.5 * mm});
            skCircle(sketch, "E1043", {"center": v(-910, -112.58) * mm, "radius": 26.5 * mm});
            skCircle(sketch, "E1044", {"center": v(-975, -112.58) * mm, "radius": 26.5 * mm});
            skCircle(sketch, "E1045", {"center": v(-1040, -112.58) * mm, "radius": 26.5 * mm});
            skCircle(sketch, "E1046", {"center": v(-1105, -112.58) * mm, "radius": 26.5 * mm});
            skCircle(sketch, "E1047", {"center": v(-1170, -112.58) * mm, "radius": 26.5 * mm});
            skCircle(sketch, "E1048", {"center": v(-1235, -112.58) * mm, "radius": 26.5 * mm});
            skCircle(sketch, "E1049", {"center": v(-1300, -112.58) * mm, "radius": 26.5 * mm});
            skCircle(sketch, "E1050", {"center": v(-1365, -112.58) * mm, "radius": 26.5 * mm});
            skCircle(sketch, "E1051", {"center": v(-1430, -112.58) * mm, "radius": 26.5 * mm});
            skCircle(sketch, "E1052", {"center": v(-1495, -112.58) * mm, "radius": 26.5 * mm});
            skCircle(sketch, "E1053", {"center": v(-1560, -112.58) * mm, "radius": 26.5 * mm});
            skCircle(sketch, "E1054", {"center": v(-357.5, -168.87) * mm, "radius": 26.5 * mm});
            skCircle(sketch, "E1055", {"center": v(-422.5, -168.87) * mm, "radius": 26.5 * mm});
            skCircle(sketch, "E1056", {"center": v(-487.5, -168.87) * mm, "radius": 26.5 * mm});
            skCircle(sketch, "E1057", {"center": v(-552.5, -168.87) * mm, "radius": 26.5 * mm});
            skCircle(sketch, "E1058", {"center": v(-617.5, -168.87) * mm, "radius": 26.5 * mm});
            skCircle(sketch, "E1059", {"center": v(-682.5, -168.87) * mm, "radius": 26.5 * mm});
            skCircle(sketch, "E1060", {"center": v(-747.5, -168.87) * mm, "radius": 26.5 * mm});
            skCircle(sketch, "E1061", {"center": v(-812.5, -168.87) * mm, "radius": 26.5 * mm});
            skCircle(sketch, "E1062", {"center": v(-877.5, -168.87) * mm, "radius": 26.5 * mm});
            skCircle(sketch, "E1063", {"center": v(-942.5, -168.87) * mm, "radius": 26.5 * mm});
            skCircle(sketch, "E1064", {"center": v(-1007.5, -168.87) * mm, "radius": 26.5 * mm});
            skCircle(sketch, "E1065", {"center": v(-1072.5, -168.87) * mm, "radius": 26.5 * mm});
            skCircle(sketch, "E1066", {"center": v(-1137.5, -168.87) * mm, "radius": 26.5 * mm});
            skCircle(sketch, "E1067", {"center": v(-1202.5, -168.87) * mm, "radius": 26.5 * mm});
            skCircle(sketch, "E1068", {"center": v(-1267.5, -168.87) * mm, "radius": 26.5 * mm});
            skCircle(sketch, "E1069", {"center": v(-1332.5, -168.87) * mm, "radius": 26.5 * mm});
            skCircle(sketch, "E1070", {"center": v(-1397.5, -168.87) * mm, "radius": 26.5 * mm});
            skCircle(sketch, "E1071", {"center": v(-1462.5, -168.87) * mm, "radius": 26.5 * mm});
            skCircle(sketch, "E1072", {"center": v(-1527.5, -168.87) * mm, "radius": 26.5 * mm});
            skCircle(sketch, "E1073", {"center": v(-325, -225.17) * mm, "radius": 26.5 * mm});
            skCircle(sketch, "E1074", {"center": v(-390, -225.17) * mm, "radius": 26.5 * mm});
            skCircle(sketch, "E1075", {"center": v(-455, -225.17) * mm, "radius": 26.5 * mm});
            skCircle(sketch, "E1076", {"center": v(-520, -225.17) * mm, "radius": 26.5 * mm});
            skCircle(sketch, "E1077", {"center": v(-585, -225.17) * mm, "radius": 26.5 * mm});
            skCircle(sketch, "E1078", {"center": v(-650, -225.17) * mm, "radius": 26.5 * mm});
            skCircle(sketch, "E1079", {"center": v(-715, -225.17) * mm, "radius": 26.5 * mm});
            skCircle(sketch, "E1080", {"center": v(-780, -225.17) * mm, "radius": 26.5 * mm});
            skCircle(sketch, "E1081", {"center": v(-845, -225.17) * mm, "radius": 26.5 * mm});
            skCircle(sketch, "E1082", {"center": v(-910, -225.17) * mm, "radius": 26.5 * mm});
            skCircle(sketch, "E1083", {"center": v(-975, -225.17) * mm, "radius": 26.5 * mm});
            skCircle(sketch, "E1084", {"center": v(-1040, -225.17) * mm, "radius": 26.5 * mm});
            skCircle(sketch, "E1085", {"center": v(-1105, -225.17) * mm, "radius": 26.5 * mm});
            skCircle(sketch, "E1086", {"center": v(-1170, -225.17) * mm, "radius": 26.5 * mm});
            skCircle(sketch, "E1087", {"center": v(-1235, -225.17) * mm, "radius": 26.5 * mm});
            skCircle(sketch, "E1088", {"center": v(-1300, -225.17) * mm, "radius": 26.5 * mm});
            skCircle(sketch, "E1089", {"center": v(-1365, -225.17) * mm, "radius": 26.5 * mm});
            skCircle(sketch, "E1090", {"center": v(-1430, -225.17) * mm, "radius": 26.5 * mm});
            skCircle(sketch, "E1091", {"center": v(-1495, -225.17) * mm, "radius": 26.5 * mm});
            skCircle(sketch, "E1092", {"center": v(-1560, -225.17) * mm, "radius": 26.5 * mm});
            skCircle(sketch, "E1093", {"center": v(-292.5, -281.46) * mm, "radius": 26.5 * mm});
            skCircle(sketch, "E1094", {"center": v(-357.5, -281.46) * mm, "radius": 26.5 * mm});
            skCircle(sketch, "E1095", {"center": v(-422.5, -281.46) * mm, "radius": 26.5 * mm});
            skCircle(sketch, "E1096", {"center": v(-487.5, -281.46) * mm, "radius": 26.5 * mm});
            skCircle(sketch, "E1097", {"center": v(-552.5, -281.46) * mm, "radius": 26.5 * mm});
            skCircle(sketch, "E1098", {"center": v(-617.5, -281.46) * mm, "radius": 26.5 * mm});
            skCircle(sketch, "E1099", {"center": v(-682.5, -281.46) * mm, "radius": 26.5 * mm});
            skCircle(sketch, "E1100", {"center": v(-747.5, -281.46) * mm, "radius": 26.5 * mm});
            skCircle(sketch, "E1101", {"center": v(-812.5, -281.46) * mm, "radius": 26.5 * mm});
            skCircle(sketch, "E1102", {"center": v(-877.5, -281.46) * mm, "radius": 26.5 * mm});
            skCircle(sketch, "E1103", {"center": v(-942.5, -281.46) * mm, "radius": 26.5 * mm});
            skCircle(sketch, "E1104", {"center": v(-1007.5, -281.46) * mm, "radius": 26.5 * mm});
            skCircle(sketch, "E1105", {"center": v(-1072.5, -281.46) * mm, "radius": 26.5 * mm});
            skCircle(sketch, "E1106", {"center": v(-1137.5, -281.46) * mm, "radius": 26.5 * mm});
            skCircle(sketch, "E1107", {"center": v(-1202.5, -281.46) * mm, "radius": 26.5 * mm});
            skCircle(sketch, "E1108", {"center": v(-1267.5, -281.46) * mm, "radius": 26.5 * mm});
            skCircle(sketch, "E1109", {"center": v(-1332.5, -281.46) * mm, "radius": 26.5 * mm});
            skCircle(sketch, "E1110", {"center": v(-1397.5, -281.46) * mm, "radius": 26.5 * mm});
            skCircle(sketch, "E1111", {"center": v(-1462.5, -281.46) * mm, "radius": 26.5 * mm});
            skCircle(sketch, "E1112", {"center": v(-1527.5, -281.46) * mm, "radius": 26.5 * mm});
            skCircle(sketch, "E1113", {"center": v(-260, -337.75) * mm, "radius": 26.5 * mm});
            skCircle(sketch, "E1114", {"center": v(-325, -337.75) * mm, "radius": 26.5 * mm});
            skCircle(sketch, "E1115", {"center": v(-390, -337.75) * mm, "radius": 26.5 * mm});
            skCircle(sketch, "E1116", {"center": v(-455, -337.75) * mm, "radius": 26.5 * mm});
            skCircle(sketch, "E1117", {"center": v(-520, -337.75) * mm, "radius": 26.5 * mm});
            skCircle(sketch, "E1118", {"center": v(-585, -337.75) * mm, "radius": 26.5 * mm});
            skCircle(sketch, "E1119", {"center": v(-650, -337.75) * mm, "radius": 26.5 * mm});
            skCircle(sketch, "E1120", {"center": v(-715, -337.75) * mm, "radius": 26.5 * mm});
            skCircle(sketch, "E1121", {"center": v(-780, -337.75) * mm, "radius": 26.5 * mm});
            skCircle(sketch, "E1122", {"center": v(-845, -337.75) * mm, "radius": 26.5 * mm});
            skCircle(sketch, "E1123", {"center": v(-910, -337.75) * mm, "radius": 26.5 * mm});
            skCircle(sketch, "E1124", {"center": v(-975, -337.75) * mm, "radius": 26.5 * mm});
            skCircle(sketch, "E1125", {"center": v(-1040, -337.75) * mm, "radius": 26.5 * mm});
            skCircle(sketch, "E1126", {"center": v(-1105, -337.75) * mm, "radius": 26.5 * mm});
            skCircle(sketch, "E1127", {"center": v(-1170, -337.75) * mm, "radius": 26.5 * mm});
            skCircle(sketch, "E1128", {"center": v(-1235, -337.75) * mm, "radius": 26.5 * mm});
            skCircle(sketch, "E1129", {"center": v(-1300, -337.75) * mm, "radius": 26.5 * mm});
            skCircle(sketch, "E1130", {"center": v(-1365, -337.75) * mm, "radius": 26.5 * mm});
            skCircle(sketch, "E1131", {"center": v(-1430, -337.75) * mm, "radius": 26.5 * mm});
            skCircle(sketch, "E1132", {"center": v(-1495, -337.75) * mm, "radius": 26.5 * mm});
            skCircle(sketch, "E1133", {"center": v(-292.5, -394.04) * mm, "radius": 26.5 * mm});
            skCircle(sketch, "E1134", {"center": v(-357.5, -394.04) * mm, "radius": 26.5 * mm});
            skCircle(sketch, "E1135", {"center": v(-422.5, -394.04) * mm, "radius": 26.5 * mm});
            skCircle(sketch, "E1136", {"center": v(-487.5, -394.04) * mm, "radius": 26.5 * mm});
            skCircle(sketch, "E1137", {"center": v(-552.5, -394.04) * mm, "radius": 26.5 * mm});
            skCircle(sketch, "E1138", {"center": v(-617.5, -394.04) * mm, "radius": 26.5 * mm});
            skCircle(sketch, "E1139", {"center": v(-682.5, -394.04) * mm, "radius": 26.5 * mm});
            skCircle(sketch, "E1140", {"center": v(-747.5, -394.04) * mm, "radius": 26.5 * mm});
            skCircle(sketch, "E1141", {"center": v(-812.5, -394.04) * mm, "radius": 26.5 * mm});
            skCircle(sketch, "E1142", {"center": v(-877.5, -394.04) * mm, "radius": 26.5 * mm});
            skCircle(sketch, "E1143", {"center": v(-942.5, -394.04) * mm, "radius": 26.5 * mm});
            skCircle(sketch, "E1144", {"center": v(-1007.5, -394.04) * mm, "radius": 26.5 * mm});
            skCircle(sketch, "E1145", {"center": v(-1072.5, -394.04) * mm, "radius": 26.5 * mm});
            skCircle(sketch, "E1146", {"center": v(-1137.5, -394.04) * mm, "radius": 26.5 * mm});
            skCircle(sketch, "E1147", {"center": v(-1202.5, -394.04) * mm, "radius": 26.5 * mm});
            skCircle(sketch, "E1148", {"center": v(-1267.5, -394.04) * mm, "radius": 26.5 * mm});
            skCircle(sketch, "E1149", {"center": v(-1332.5, -394.04) * mm, "radius": 26.5 * mm});
            skCircle(sketch, "E1150", {"center": v(-1397.5, -394.04) * mm, "radius": 26.5 * mm});
            skCircle(sketch, "E1151", {"center": v(-1462.5, -394.04) * mm, "radius": 26.5 * mm});
            skCircle(sketch, "E1152", {"center": v(-1527.5, -394.04) * mm, "radius": 26.5 * mm});
            skCircle(sketch, "E1153", {"center": v(-325, -450.33) * mm, "radius": 26.5 * mm});
            skCircle(sketch, "E1154", {"center": v(-390, -450.33) * mm, "radius": 26.5 * mm});
            skCircle(sketch, "E1155", {"center": v(-455, -450.33) * mm, "radius": 26.5 * mm});
            skCircle(sketch, "E1156", {"center": v(-520, -450.33) * mm, "radius": 26.5 * mm});
            skCircle(sketch, "E1157", {"center": v(-585, -450.33) * mm, "radius": 26.5 * mm});
            skCircle(sketch, "E1158", {"center": v(-650, -450.33) * mm, "radius": 26.5 * mm});
            skCircle(sketch, "E1159", {"center": v(-715, -450.33) * mm, "radius": 26.5 * mm});
            skCircle(sketch, "E1160", {"center": v(-780, -450.33) * mm, "radius": 26.5 * mm});
            skCircle(sketch, "E1161", {"center": v(-845, -450.33) * mm, "radius": 26.5 * mm});
            skCircle(sketch, "E1162", {"center": v(-910, -450.33) * mm, "radius": 26.5 * mm});
            skCircle(sketch, "E1163", {"center": v(-975, -450.33) * mm, "radius": 26.5 * mm});
            skCircle(sketch, "E1164", {"center": v(-1040, -450.33) * mm, "radius": 26.5 * mm});
            skCircle(sketch, "E1165", {"center": v(-1105, -450.33) * mm, "radius": 26.5 * mm});
            skCircle(sketch, "E1166", {"center": v(-1170, -450.33) * mm, "radius": 26.5 * mm});
            skCircle(sketch, "E1167", {"center": v(-1235, -450.33) * mm, "radius": 26.5 * mm});
            skCircle(sketch, "E1168", {"center": v(-1300, -450.33) * mm, "radius": 26.5 * mm});
            skCircle(sketch, "E1169", {"center": v(-1365, -450.33) * mm, "radius": 26.5 * mm});
            skCircle(sketch, "E1170", {"center": v(-1430, -450.33) * mm, "radius": 26.5 * mm});
            skCircle(sketch, "E1171", {"center": v(-1495, -450.33) * mm, "radius": 26.5 * mm});
            skCircle(sketch, "E1172", {"center": v(-357.5, -506.62) * mm, "radius": 26.5 * mm});
            skCircle(sketch, "E1173", {"center": v(-422.5, -506.62) * mm, "radius": 26.5 * mm});
            skCircle(sketch, "E1174", {"center": v(-487.5, -506.62) * mm, "radius": 26.5 * mm});
            skCircle(sketch, "E1175", {"center": v(-552.5, -506.62) * mm, "radius": 26.5 * mm});
            skCircle(sketch, "E1176", {"center": v(-617.5, -506.62) * mm, "radius": 26.5 * mm});
            skCircle(sketch, "E1177", {"center": v(-682.5, -506.62) * mm, "radius": 26.5 * mm});
            skCircle(sketch, "E1178", {"center": v(-747.5, -506.62) * mm, "radius": 26.5 * mm});
            skCircle(sketch, "E1179", {"center": v(-812.5, -506.62) * mm, "radius": 26.5 * mm});
            skCircle(sketch, "E1180", {"center": v(-877.5, -506.62) * mm, "radius": 26.5 * mm});
            skCircle(sketch, "E1181", {"center": v(-1072.5, -506.62) * mm, "radius": 26.5 * mm});
            skCircle(sketch, "E1182", {"center": v(-1137.5, -506.62) * mm, "radius": 26.5 * mm});
            skCircle(sketch, "E1183", {"center": v(-1202.5, -506.62) * mm, "radius": 26.5 * mm});
            skCircle(sketch, "E1184", {"center": v(-1267.5, -506.62) * mm, "radius": 26.5 * mm});
            skCircle(sketch, "E1185", {"center": v(-1332.5, -506.62) * mm, "radius": 26.5 * mm});
            skCircle(sketch, "E1186", {"center": v(-1397.5, -506.62) * mm, "radius": 26.5 * mm});
            skCircle(sketch, "E1187", {"center": v(-1462.5, -506.62) * mm, "radius": 26.5 * mm});
            skCircle(sketch, "E1188", {"center": v(-390, -562.92) * mm, "radius": 26.5 * mm});
            skCircle(sketch, "E1189", {"center": v(-455, -562.92) * mm, "radius": 26.5 * mm});
            skCircle(sketch, "E1190", {"center": v(-520, -562.92) * mm, "radius": 26.5 * mm});
            skCircle(sketch, "E1191", {"center": v(-585, -562.92) * mm, "radius": 26.5 * mm});
            skCircle(sketch, "E1192", {"center": v(-650, -562.92) * mm, "radius": 26.5 * mm});
            skCircle(sketch, "E1193", {"center": v(-715, -562.92) * mm, "radius": 26.5 * mm});
            skCircle(sketch, "E1194", {"center": v(-780, -562.92) * mm, "radius": 26.5 * mm});
            skCircle(sketch, "E1195", {"center": v(-845, -562.92) * mm, "radius": 26.5 * mm});
            skCircle(sketch, "E1196", {"center": v(-1105, -562.92) * mm, "radius": 26.5 * mm});
            skCircle(sketch, "E1197", {"center": v(-1170, -562.92) * mm, "radius": 26.5 * mm});
            skCircle(sketch, "E1198", {"center": v(-1235, -562.92) * mm, "radius": 26.5 * mm});
            skCircle(sketch, "E1199", {"center": v(-1300, -562.92) * mm, "radius": 26.5 * mm});
            skCircle(sketch, "E1200", {"center": v(-1365, -562.92) * mm, "radius": 26.5 * mm});
            skCircle(sketch, "E1201", {"center": v(-1430, -562.92) * mm, "radius": 26.5 * mm});
            skCircle(sketch, "E1202", {"center": v(-422.5, -619.2) * mm, "radius": 26.5 * mm});
            skCircle(sketch, "E1203", {"center": v(-487.5, -619.2) * mm, "radius": 26.5 * mm});
            skCircle(sketch, "E1204", {"center": v(-552.5, -619.2) * mm, "radius": 26.5 * mm});
            skCircle(sketch, "E1205", {"center": v(-617.5, -619.2) * mm, "radius": 26.5 * mm});
            skCircle(sketch, "E1206", {"center": v(-682.5, -619.2) * mm, "radius": 26.5 * mm});
            skCircle(sketch, "E1207", {"center": v(-747.5, -619.2) * mm, "radius": 26.5 * mm});
            skCircle(sketch, "E1208", {"center": v(-812.5, -619.2) * mm, "radius": 26.5 * mm});
            skCircle(sketch, "E1209", {"center": v(-877.5, -619.2) * mm, "radius": 26.5 * mm});
            skCircle(sketch, "E1210", {"center": v(-1072.5, -619.2) * mm, "radius": 26.5 * mm});
            skCircle(sketch, "E1211", {"center": v(-1137.5, -619.2) * mm, "radius": 26.5 * mm});
            skCircle(sketch, "E1212", {"center": v(-1202.5, -619.2) * mm, "radius": 26.5 * mm});
            skCircle(sketch, "E1213", {"center": v(-1267.5, -619.2) * mm, "radius": 26.5 * mm});
            skCircle(sketch, "E1214", {"center": v(-1332.5, -619.2) * mm, "radius": 26.5 * mm});
            skCircle(sketch, "E1215", {"center": v(-1397.5, -619.2) * mm, "radius": 26.5 * mm});
            skCircle(sketch, "E1216", {"center": v(-455, -675.5) * mm, "radius": 26.5 * mm});
            skCircle(sketch, "E1217", {"center": v(-520, -675.5) * mm, "radius": 26.5 * mm});
            skCircle(sketch, "E1218", {"center": v(-585, -675.5) * mm, "radius": 26.5 * mm});
            skCircle(sketch, "E1219", {"center": v(-650, -675.5) * mm, "radius": 26.5 * mm});
            skCircle(sketch, "E1220", {"center": v(-715, -675.5) * mm, "radius": 26.5 * mm});
            skCircle(sketch, "E1221", {"center": v(-780, -675.5) * mm, "radius": 26.5 * mm});
            skCircle(sketch, "E1222", {"center": v(-845, -675.5) * mm, "radius": 26.5 * mm});
            skCircle(sketch, "E1223", {"center": v(-910, -675.5) * mm, "radius": 26.5 * mm});
            skCircle(sketch, "E1224", {"center": v(-975, -675.5) * mm, "radius": 26.5 * mm});
            skCircle(sketch, "E1225", {"center": v(-1040, -675.5) * mm, "radius": 26.5 * mm});
            skCircle(sketch, "E1226", {"center": v(-1105, -675.5) * mm, "radius": 26.5 * mm});
            skCircle(sketch, "E1227", {"center": v(-1170, -675.5) * mm, "radius": 26.5 * mm});
            skCircle(sketch, "E1228", {"center": v(-1235, -675.5) * mm, "radius": 26.5 * mm});
            skCircle(sketch, "E1229", {"center": v(-1300, -675.5) * mm, "radius": 26.5 * mm});
            skCircle(sketch, "E1230", {"center": v(-1365, -675.5) * mm, "radius": 26.5 * mm});
            skCircle(sketch, "E1231", {"center": v(-487.5, -731.8) * mm, "radius": 26.5 * mm});
            skCircle(sketch, "E1232", {"center": v(-552.5, -731.8) * mm, "radius": 26.5 * mm});
            skCircle(sketch, "E1233", {"center": v(-617.5, -731.8) * mm, "radius": 26.5 * mm});
            skCircle(sketch, "E1234", {"center": v(-682.5, -731.8) * mm, "radius": 26.5 * mm});
            skCircle(sketch, "E1235", {"center": v(-747.5, -731.8) * mm, "radius": 26.5 * mm});
            skCircle(sketch, "E1236", {"center": v(-812.5, -731.8) * mm, "radius": 26.5 * mm});
            skCircle(sketch, "E1237", {"center": v(-877.5, -731.8) * mm, "radius": 26.5 * mm});
            skCircle(sketch, "E1238", {"center": v(-942.5, -731.8) * mm, "radius": 26.5 * mm});
            skCircle(sketch, "E1239", {"center": v(-1007.5, -731.8) * mm, "radius": 26.5 * mm});
            skCircle(sketch, "E1240", {"center": v(-1072.5, -731.8) * mm, "radius": 26.5 * mm});
            skCircle(sketch, "E1241", {"center": v(-1137.5, -731.8) * mm, "radius": 26.5 * mm});
            skCircle(sketch, "E1242", {"center": v(-1202.5, -731.8) * mm, "radius": 26.5 * mm});
            skCircle(sketch, "E1243", {"center": v(-1267.5, -731.8) * mm, "radius": 26.5 * mm});
            skCircle(sketch, "E1244", {"center": v(-1332.5, -731.8) * mm, "radius": 26.5 * mm});
            skCircle(sketch, "E1245", {"center": v(-1397.5, -731.8) * mm, "radius": 26.5 * mm});
            skCircle(sketch, "E1246", {"center": v(-520, -788.08) * mm, "radius": 26.5 * mm});
            skCircle(sketch, "E1247", {"center": v(-585, -788.08) * mm, "radius": 26.5 * mm});
            skCircle(sketch, "E1248", {"center": v(-650, -788.08) * mm, "radius": 26.5 * mm});
            skCircle(sketch, "E1249", {"center": v(-715, -788.08) * mm, "radius": 26.5 * mm});
            skCircle(sketch, "E1250", {"center": v(-780, -788.08) * mm, "radius": 26.5 * mm});
            skCircle(sketch, "E1251", {"center": v(-845, -788.08) * mm, "radius": 26.5 * mm});
            skCircle(sketch, "E1252", {"center": v(-910, -788.08) * mm, "radius": 26.5 * mm});
            skCircle(sketch, "E1253", {"center": v(-975, -788.08) * mm, "radius": 26.5 * mm});
            skCircle(sketch, "E1254", {"center": v(-1040, -788.08) * mm, "radius": 26.5 * mm});
            skCircle(sketch, "E1255", {"center": v(-1105, -788.08) * mm, "radius": 26.5 * mm});
            skCircle(sketch, "E1256", {"center": v(-1170, -788.08) * mm, "radius": 26.5 * mm});
            skCircle(sketch, "E1257", {"center": v(-1235, -788.08) * mm, "radius": 26.5 * mm});
            skCircle(sketch, "E1258", {"center": v(-1300, -788.08) * mm, "radius": 26.5 * mm});
            skCircle(sketch, "E1259", {"center": v(-1365, -788.08) * mm, "radius": 26.5 * mm});
            skCircle(sketch, "E1260", {"center": v(-552.5, -844.37) * mm, "radius": 26.5 * mm});
            skCircle(sketch, "E1261", {"center": v(-617.5, -844.37) * mm, "radius": 26.5 * mm});
            skCircle(sketch, "E1262", {"center": v(-682.5, -844.37) * mm, "radius": 26.5 * mm});
            skCircle(sketch, "E1263", {"center": v(-747.5, -844.37) * mm, "radius": 26.5 * mm});
            skCircle(sketch, "E1264", {"center": v(-812.5, -844.37) * mm, "radius": 26.5 * mm});
            skCircle(sketch, "E1265", {"center": v(-877.5, -844.37) * mm, "radius": 26.5 * mm});
            skCircle(sketch, "E1266", {"center": v(-942.5, -844.37) * mm, "radius": 26.5 * mm});
            skCircle(sketch, "E1267", {"center": v(-1007.5, -844.37) * mm, "radius": 26.5 * mm});
            skCircle(sketch, "E1268", {"center": v(-1072.5, -844.37) * mm, "radius": 26.5 * mm});
            skCircle(sketch, "E1269", {"center": v(-1137.5, -844.37) * mm, "radius": 26.5 * mm});
            skCircle(sketch, "E1270", {"center": v(-1202.5, -844.37) * mm, "radius": 26.5 * mm});
            skCircle(sketch, "E1271", {"center": v(-1267.5, -844.37) * mm, "radius": 26.5 * mm});
            skCircle(sketch, "E1272", {"center": v(-1332.5, -844.37) * mm, "radius": 26.5 * mm});
            skCircle(sketch, "E1273", {"center": v(-585, -900.67) * mm, "radius": 26.5 * mm});
            skCircle(sketch, "E1274", {"center": v(-650, -900.67) * mm, "radius": 26.5 * mm});
            skCircle(sketch, "E1275", {"center": v(-715, -900.67) * mm, "radius": 26.5 * mm});
            skCircle(sketch, "E1276", {"center": v(-780, -900.67) * mm, "radius": 26.5 * mm});
            skCircle(sketch, "E1277", {"center": v(-845, -900.67) * mm, "radius": 26.5 * mm});
            skCircle(sketch, "E1278", {"center": v(-910, -900.67) * mm, "radius": 26.5 * mm});
            skCircle(sketch, "E1279", {"center": v(-975, -900.67) * mm, "radius": 26.5 * mm});
            skCircle(sketch, "E1280", {"center": v(-1040, -900.67) * mm, "radius": 26.5 * mm});
            skCircle(sketch, "E1281", {"center": v(-1105, -900.67) * mm, "radius": 26.5 * mm});
            skCircle(sketch, "E1282", {"center": v(-1170, -900.67) * mm, "radius": 26.5 * mm});
            skCircle(sketch, "E1283", {"center": v(-1235, -900.67) * mm, "radius": 26.5 * mm});
            skCircle(sketch, "E1284", {"center": v(-617.5, -956.96) * mm, "radius": 26.5 * mm});
            skCircle(sketch, "E1285", {"center": v(-682.5, -956.96) * mm, "radius": 26.5 * mm});
            skCircle(sketch, "E1286", {"center": v(-747.5, -956.96) * mm, "radius": 26.5 * mm});
            skCircle(sketch, "E1287", {"center": v(-812.5, -956.96) * mm, "radius": 26.5 * mm});
            skCircle(sketch, "E1288", {"center": v(-877.5, -956.96) * mm, "radius": 26.5 * mm});
            skCircle(sketch, "E1289", {"center": v(-942.5, -956.96) * mm, "radius": 26.5 * mm});
            skCircle(sketch, "E1290", {"center": v(-1007.5, -956.96) * mm, "radius": 26.5 * mm});
            skCircle(sketch, "E1291", {"center": v(-1072.5, -956.96) * mm, "radius": 26.5 * mm});
            skCircle(sketch, "E1292", {"center": v(-1137.5, -956.96) * mm, "radius": 26.5 * mm});
            skCircle(sketch, "E1293", {"center": v(-1202.5, -956.96) * mm, "radius": 26.5 * mm});
            skCircle(sketch, "E1294", {"center": v(-650, -1013.25) * mm, "radius": 26.5 * mm});
            skCircle(sketch, "E1295", {"center": v(-715, -1013.25) * mm, "radius": 26.5 * mm});
            skCircle(sketch, "E1296", {"center": v(-780, -1013.25) * mm, "radius": 26.5 * mm});
            skCircle(sketch, "E1297", {"center": v(-845, -1013.25) * mm, "radius": 26.5 * mm});
            skCircle(sketch, "E1298", {"center": v(-910, -1013.25) * mm, "radius": 26.5 * mm});
            skCircle(sketch, "E1299", {"center": v(-975, -1013.25) * mm, "radius": 26.5 * mm});
            skCircle(sketch, "E1300", {"center": v(-1040, -1013.25) * mm, "radius": 26.5 * mm});
            skCircle(sketch, "E1301", {"center": v(-1105, -1013.25) * mm, "radius": 26.5 * mm});
            skCircle(sketch, "E1302", {"center": v(-1170, -1013.25) * mm, "radius": 26.5 * mm});
            skCircle(sketch, "E1303", {"center": v(-682.5, -1069.54) * mm, "radius": 26.5 * mm});
            skCircle(sketch, "E1304", {"center": v(-747.5, -1069.54) * mm, "radius": 26.5 * mm});
            skCircle(sketch, "E1305", {"center": v(-812.5, -1069.54) * mm, "radius": 26.5 * mm});
            skCircle(sketch, "E1306", {"center": v(-877.5, -1069.54) * mm, "radius": 26.5 * mm});
            skCircle(sketch, "E1307", {"center": v(-942.5, -1069.54) * mm, "radius": 26.5 * mm});
            skCircle(sketch, "E1308", {"center": v(-1007.5, -1069.54) * mm, "radius": 26.5 * mm});
            skCircle(sketch, "E1309", {"center": v(-1072.5, -1069.54) * mm, "radius": 26.5 * mm});
            skCircle(sketch, "E1310", {"center": v(-1137.5, -1069.54) * mm, "radius": 26.5 * mm});
            skCircle(sketch, "E1311", {"center": v(-715, -1125.83) * mm, "radius": 26.5 * mm});
            skCircle(sketch, "E1312", {"center": v(-780, -1125.83) * mm, "radius": 26.5 * mm});
            skCircle(sketch, "E1313", {"center": v(-845, -1125.83) * mm, "radius": 26.5 * mm});
            skCircle(sketch, "E1314", {"center": v(-910, -1125.83) * mm, "radius": 26.5 * mm});
            skCircle(sketch, "E1315", {"center": v(-975, -1125.83) * mm, "radius": 26.5 * mm});
            skCircle(sketch, "E1316", {"center": v(-1040, -1125.83) * mm, "radius": 26.5 * mm});
            skCircle(sketch, "E1317", {"center": v(-1105, -1125.83) * mm, "radius": 26.5 * mm});
            skCircle(sketch, "E1318", {"center": v(-747.5, -1182.12) * mm, "radius": 26.5 * mm});
            skCircle(sketch, "E1319", {"center": v(-812.5, -1182.12) * mm, "radius": 26.5 * mm});
            skCircle(sketch, "E1320", {"center": v(-877.5, -1182.12) * mm, "radius": 26.5 * mm});
            skCircle(sketch, "E1321", {"center": v(-942.5, -1182.12) * mm, "radius": 26.5 * mm});
            skCircle(sketch, "E1322", {"center": v(-1007.5, -1182.12) * mm, "radius": 26.5 * mm});
            skCircle(sketch, "E1323", {"center": v(-780, -1238.42) * mm, "radius": 26.5 * mm});
            skCircle(sketch, "E1324", {"center": v(-845, -1238.42) * mm, "radius": 26.5 * mm});
            skCircle(sketch, "E1325", {"center": v(-910, -1238.42) * mm, "radius": 26.5 * mm});
            skCircle(sketch, "E1326", {"center": v(-975, -1238.42) * mm, "radius": 26.5 * mm});
            skCircle(sketch, "E1327", {"center": v(-812.5, -1294.7) * mm, "radius": 26.5 * mm});
            skCircle(sketch, "E1328", {"center": v(-877.5, -1294.7) * mm, "radius": 26.5 * mm});
            skCircle(sketch, "E1329", {"center": v(-975, -562.92) * mm, "radius": 58 * mm});
            skCircle(sketch, "E1330", {"center": v(-195, -337.75) * mm, "radius": 26.5 * mm});
            skCircle(sketch, "E1331", {"center": v(-227.5, -394.04) * mm, "radius": 26.5 * mm});
            skCircle(sketch, "E1332", {"center": v(-260, -450.33) * mm, "radius": 26.5 * mm});
            skCircle(sketch, "E1333", {"center": v(-292.5, -506.62) * mm, "radius": 26.5 * mm});
            skCircle(sketch, "E1334", {"center": v(-325, -562.92) * mm, "radius": 26.5 * mm});
            skCircle(sketch, "E1335", {"center": v(-357.5, -619.2) * mm, "radius": 26.5 * mm});
            skCircle(sketch, "E1336", {"center": v(-390, -675.5) * mm, "radius": 26.5 * mm});
            skCircle(sketch, "E1337", {"center": v(-422.5, -731.8) * mm, "radius": 26.5 * mm});
            skCircle(sketch, "E1338", {"center": v(-455, -788.08) * mm, "radius": 26.5 * mm});
            skCircle(sketch, "E1339", {"center": v(-487.5, -844.37) * mm, "radius": 26.5 * mm});
            skCircle(sketch, "E1340", {"center": v(-520, -900.67) * mm, "radius": 26.5 * mm});
            skCircle(sketch, "E1341", {"center": v(-552.5, -956.96) * mm, "radius": 26.5 * mm});
            skCircle(sketch, "E1342", {"center": v(-585, -1013.25) * mm, "radius": 26.5 * mm});
            skCircle(sketch, "E1343", {"center": v(-617.5, -1069.54) * mm, "radius": 26.5 * mm});
            skCircle(sketch, "E1344", {"center": v(-650, -1125.83) * mm, "radius": 26.5 * mm});
            skCircle(sketch, "E1345", {"center": v(-682.5, -1182.12) * mm, "radius": 26.5 * mm});
            skCircle(sketch, "E1346", {"center": v(-715, -1238.42) * mm, "radius": 26.5 * mm});
            skCircle(sketch, "E1347", {"center": v(-747.5, -1294.7) * mm, "radius": 26.5 * mm});
            skCircle(sketch, "E1348", {"center": v(-780, -1351) * mm, "radius": 26.5 * mm});
            skCircle(sketch, "E1349", {"center": v(-162.5, -394.04) * mm, "radius": 26.5 * mm});
            skCircle(sketch, "E1350", {"center": v(-195, -450.33) * mm, "radius": 26.5 * mm});
            skCircle(sketch, "E1351", {"center": v(-227.5, -506.62) * mm, "radius": 26.5 * mm});
            skCircle(sketch, "E1352", {"center": v(-260, -562.92) * mm, "radius": 26.5 * mm});
            skCircle(sketch, "E1353", {"center": v(-292.5, -619.2) * mm, "radius": 26.5 * mm});
            skCircle(sketch, "E1354", {"center": v(-325, -675.5) * mm, "radius": 26.5 * mm});
            skCircle(sketch, "E1355", {"center": v(-357.5, -731.8) * mm, "radius": 26.5 * mm});
            skCircle(sketch, "E1356", {"center": v(-390, -788.08) * mm, "radius": 26.5 * mm});
            skCircle(sketch, "E1357", {"center": v(-422.5, -844.37) * mm, "radius": 26.5 * mm});
            skCircle(sketch, "E1358", {"center": v(-455, -900.67) * mm, "radius": 26.5 * mm});
            skCircle(sketch, "E1359", {"center": v(-487.5, -956.96) * mm, "radius": 26.5 * mm});
            skCircle(sketch, "E1360", {"center": v(-520, -1013.25) * mm, "radius": 26.5 * mm});
            skCircle(sketch, "E1361", {"center": v(-552.5, -1069.54) * mm, "radius": 26.5 * mm});
            skCircle(sketch, "E1362", {"center": v(-585, -1125.83) * mm, "radius": 26.5 * mm});
            skCircle(sketch, "E1363", {"center": v(-617.5, -1182.12) * mm, "radius": 26.5 * mm});
            skCircle(sketch, "E1364", {"center": v(-650, -1238.42) * mm, "radius": 26.5 * mm});
            skCircle(sketch, "E1365", {"center": v(-682.5, -1294.7) * mm, "radius": 26.5 * mm});
            skCircle(sketch, "E1366", {"center": v(-715, -1351) * mm, "radius": 26.5 * mm});
            skCircle(sketch, "E1367", {"center": v(-97.5, -394.04) * mm, "radius": 26.5 * mm});
            skCircle(sketch, "E1368", {"center": v(-130, -450.33) * mm, "radius": 26.5 * mm});
            skCircle(sketch, "E1369", {"center": v(-162.5, -506.62) * mm, "radius": 26.5 * mm});
            skCircle(sketch, "E1370", {"center": v(-195, -562.92) * mm, "radius": 26.5 * mm});
            skCircle(sketch, "E1371", {"center": v(-227.5, -619.2) * mm, "radius": 26.5 * mm});
            skCircle(sketch, "E1372", {"center": v(-260, -675.5) * mm, "radius": 26.5 * mm});
            skCircle(sketch, "E1373", {"center": v(-292.5, -731.8) * mm, "radius": 26.5 * mm});
            skCircle(sketch, "E1374", {"center": v(-325, -788.08) * mm, "radius": 26.5 * mm});
            skCircle(sketch, "E1375", {"center": v(-357.5, -844.37) * mm, "radius": 26.5 * mm});
            skCircle(sketch, "E1376", {"center": v(-390, -900.67) * mm, "radius": 26.5 * mm});
            skCircle(sketch, "E1377", {"center": v(-422.5, -956.96) * mm, "radius": 26.5 * mm});
            skCircle(sketch, "E1378", {"center": v(-455, -1013.25) * mm, "radius": 26.5 * mm});
            skCircle(sketch, "E1379", {"center": v(-487.5, -1069.54) * mm, "radius": 26.5 * mm});
            skCircle(sketch, "E1380", {"center": v(-520, -1125.83) * mm, "radius": 26.5 * mm});
            skCircle(sketch, "E1381", {"center": v(-552.5, -1182.12) * mm, "radius": 26.5 * mm});
            skCircle(sketch, "E1382", {"center": v(-585, -1238.42) * mm, "radius": 26.5 * mm});
            skCircle(sketch, "E1383", {"center": v(-617.5, -1294.7) * mm, "radius": 26.5 * mm});
            skCircle(sketch, "E1384", {"center": v(-650, -1351) * mm, "radius": 26.5 * mm});
            skCircle(sketch, "E1385", {"center": v(-682.5, -1407.3) * mm, "radius": 26.5 * mm});
            skCircle(sketch, "E1386", {"center": v(-32.5, -394.04) * mm, "radius": 26.5 * mm});
            skCircle(sketch, "E1387", {"center": v(-65, -450.33) * mm, "radius": 26.5 * mm});
            skCircle(sketch, "E1388", {"center": v(-97.5, -506.62) * mm, "radius": 26.5 * mm});
            skCircle(sketch, "E1389", {"center": v(-130, -562.92) * mm, "radius": 26.5 * mm});
            skCircle(sketch, "E1390", {"center": v(-162.5, -619.2) * mm, "radius": 26.5 * mm});
            skCircle(sketch, "E1391", {"center": v(-195, -675.5) * mm, "radius": 26.5 * mm});
            skCircle(sketch, "E1392", {"center": v(-227.5, -731.8) * mm, "radius": 26.5 * mm});
            skCircle(sketch, "E1393", {"center": v(-260, -788.08) * mm, "radius": 26.5 * mm});
            skCircle(sketch, "E1394", {"center": v(-292.5, -844.37) * mm, "radius": 26.5 * mm});
            skCircle(sketch, "E1395", {"center": v(-325, -900.67) * mm, "radius": 26.5 * mm});
            skCircle(sketch, "E1396", {"center": v(-357.5, -956.96) * mm, "radius": 26.5 * mm});
            skCircle(sketch, "E1397", {"center": v(-390, -1013.25) * mm, "radius": 26.5 * mm});
            skCircle(sketch, "E1398", {"center": v(-422.5, -1069.54) * mm, "radius": 26.5 * mm});
            skCircle(sketch, "E1399", {"center": v(-455, -1125.83) * mm, "radius": 26.5 * mm});
            skCircle(sketch, "E1400", {"center": v(-487.5, -1182.12) * mm, "radius": 26.5 * mm});
            skCircle(sketch, "E1401", {"center": v(-520, -1238.42) * mm, "radius": 26.5 * mm});
            skCircle(sketch, "E1402", {"center": v(-552.5, -1294.7) * mm, "radius": 26.5 * mm});
            skCircle(sketch, "E1403", {"center": v(-585, -1351) * mm, "radius": 26.5 * mm});
            skCircle(sketch, "E1404", {"center": v(-617.5, -1407.3) * mm, "radius": 26.5 * mm});
            skCircle(sketch, "E1405", {"center": v(32.5, -394.04) * mm, "radius": 26.5 * mm});
            skCircle(sketch, "E1406", {"center": v(0, -450.33) * mm, "radius": 26.5 * mm});
            skCircle(sketch, "E1407", {"center": v(-32.5, -506.62) * mm, "radius": 26.5 * mm});
            skCircle(sketch, "E1408", {"center": v(-65, -562.92) * mm, "radius": 26.5 * mm});
            skCircle(sketch, "E1409", {"center": v(-97.5, -619.2) * mm, "radius": 26.5 * mm});
            skCircle(sketch, "E1410", {"center": v(-130, -675.5) * mm, "radius": 26.5 * mm});
            skCircle(sketch, "E1411", {"center": v(-162.5, -731.8) * mm, "radius": 26.5 * mm});
            skCircle(sketch, "E1412", {"center": v(-195, -788.08) * mm, "radius": 26.5 * mm});
            skCircle(sketch, "E1413", {"center": v(-227.5, -844.37) * mm, "radius": 26.5 * mm});
            skCircle(sketch, "E1414", {"center": v(-260, -900.67) * mm, "radius": 26.5 * mm});
            skCircle(sketch, "E1415", {"center": v(-292.5, -956.96) * mm, "radius": 26.5 * mm});
            skCircle(sketch, "E1416", {"center": v(-325, -1013.25) * mm, "radius": 26.5 * mm});
            skCircle(sketch, "E1417", {"center": v(-357.5, -1069.54) * mm, "radius": 26.5 * mm});
            skCircle(sketch, "E1418", {"center": v(-390, -1125.83) * mm, "radius": 26.5 * mm});
            skCircle(sketch, "E1419", {"center": v(-422.5, -1182.12) * mm, "radius": 26.5 * mm});
            skCircle(sketch, "E1420", {"center": v(-455, -1238.42) * mm, "radius": 26.5 * mm});
            skCircle(sketch, "E1421", {"center": v(-487.5, -1294.7) * mm, "radius": 26.5 * mm});
            skCircle(sketch, "E1422", {"center": v(-520, -1351) * mm, "radius": 26.5 * mm});
            skCircle(sketch, "E1423", {"center": v(-552.5, -1407.3) * mm, "radius": 26.5 * mm});
            skCircle(sketch, "E1424", {"center": v(-585, -1463.58) * mm, "radius": 26.5 * mm});
            skCircle(sketch, "E1425", {"center": v(97.5, -394.04) * mm, "radius": 26.5 * mm});
            skCircle(sketch, "E1426", {"center": v(65, -450.33) * mm, "radius": 26.5 * mm});
            skCircle(sketch, "E1427", {"center": v(32.5, -506.62) * mm, "radius": 26.5 * mm});
            skCircle(sketch, "E1428", {"center": v(0, -562.92) * mm, "radius": 26.5 * mm});
            skCircle(sketch, "E1429", {"center": v(-32.5, -619.2) * mm, "radius": 26.5 * mm});
            skCircle(sketch, "E1430", {"center": v(-65, -675.5) * mm, "radius": 26.5 * mm});
            skCircle(sketch, "E1431", {"center": v(-97.5, -731.8) * mm, "radius": 26.5 * mm});
            skCircle(sketch, "E1432", {"center": v(-130, -788.08) * mm, "radius": 26.5 * mm});
            skCircle(sketch, "E1433", {"center": v(-162.5, -844.37) * mm, "radius": 26.5 * mm});
            skCircle(sketch, "E1434", {"center": v(-195, -900.67) * mm, "radius": 26.5 * mm});
            skCircle(sketch, "E1435", {"center": v(-227.5, -956.96) * mm, "radius": 26.5 * mm});
            skCircle(sketch, "E1436", {"center": v(-260, -1013.25) * mm, "radius": 26.5 * mm});
            skCircle(sketch, "E1437", {"center": v(-292.5, -1069.54) * mm, "radius": 26.5 * mm});
            skCircle(sketch, "E1438", {"center": v(-325, -1125.83) * mm, "radius": 26.5 * mm});
            skCircle(sketch, "E1439", {"center": v(-357.5, -1182.12) * mm, "radius": 26.5 * mm});
            skCircle(sketch, "E1440", {"center": v(-390, -1238.42) * mm, "radius": 26.5 * mm});
            skCircle(sketch, "E1441", {"center": v(-422.5, -1294.7) * mm, "radius": 26.5 * mm});
            skCircle(sketch, "E1442", {"center": v(-455, -1351) * mm, "radius": 26.5 * mm});
            skCircle(sketch, "E1443", {"center": v(-487.5, -1407.3) * mm, "radius": 26.5 * mm});
            skCircle(sketch, "E1444", {"center": v(-520, -1463.58) * mm, "radius": 26.5 * mm});
            skCircle(sketch, "E1445", {"center": v(162.5, -394.04) * mm, "radius": 26.5 * mm});
            skCircle(sketch, "E1446", {"center": v(130, -450.33) * mm, "radius": 26.5 * mm});
            skCircle(sketch, "E1447", {"center": v(97.5, -506.62) * mm, "radius": 26.5 * mm});
            skCircle(sketch, "E1448", {"center": v(65, -562.92) * mm, "radius": 26.5 * mm});
            skCircle(sketch, "E1449", {"center": v(32.5, -619.2) * mm, "radius": 26.5 * mm});
            skCircle(sketch, "E1450", {"center": v(0, -675.5) * mm, "radius": 26.5 * mm});
            skCircle(sketch, "E1451", {"center": v(-32.5, -731.8) * mm, "radius": 26.5 * mm});
            skCircle(sketch, "E1452", {"center": v(-65, -788.08) * mm, "radius": 26.5 * mm});
            skCircle(sketch, "E1453", {"center": v(-97.5, -844.37) * mm, "radius": 26.5 * mm});
            skCircle(sketch, "E1454", {"center": v(-130, -900.67) * mm, "radius": 26.5 * mm});
            skCircle(sketch, "E1455", {"center": v(-162.5, -956.96) * mm, "radius": 26.5 * mm});
            skCircle(sketch, "E1456", {"center": v(-195, -1013.25) * mm, "radius": 26.5 * mm});
            skCircle(sketch, "E1457", {"center": v(-227.5, -1069.54) * mm, "radius": 26.5 * mm});
            skCircle(sketch, "E1458", {"center": v(-260, -1125.83) * mm, "radius": 26.5 * mm});
            skCircle(sketch, "E1459", {"center": v(-292.5, -1182.12) * mm, "radius": 26.5 * mm});
            skCircle(sketch, "E1460", {"center": v(-325, -1238.42) * mm, "radius": 26.5 * mm});
            skCircle(sketch, "E1461", {"center": v(-357.5, -1294.7) * mm, "radius": 26.5 * mm});
            skCircle(sketch, "E1462", {"center": v(-390, -1351) * mm, "radius": 26.5 * mm});
            skCircle(sketch, "E1463", {"center": v(-422.5, -1407.3) * mm, "radius": 26.5 * mm});
            skCircle(sketch, "E1464", {"center": v(-455, -1463.58) * mm, "radius": 26.5 * mm});
            skCircle(sketch, "E1465", {"center": v(195, -450.33) * mm, "radius": 26.5 * mm});
            skCircle(sketch, "E1466", {"center": v(162.5, -506.62) * mm, "radius": 26.5 * mm});
            skCircle(sketch, "E1467", {"center": v(130, -562.92) * mm, "radius": 26.5 * mm});
            skCircle(sketch, "E1468", {"center": v(97.5, -619.2) * mm, "radius": 26.5 * mm});
            skCircle(sketch, "E1469", {"center": v(65, -675.5) * mm, "radius": 26.5 * mm});
            skCircle(sketch, "E1470", {"center": v(32.5, -731.8) * mm, "radius": 26.5 * mm});
            skCircle(sketch, "E1471", {"center": v(0, -788.08) * mm, "radius": 26.5 * mm});
            skCircle(sketch, "E1472", {"center": v(-32.5, -844.37) * mm, "radius": 26.5 * mm});
            skCircle(sketch, "E1473", {"center": v(-65, -900.67) * mm, "radius": 26.5 * mm});
            skCircle(sketch, "E1474", {"center": v(-97.5, -956.96) * mm, "radius": 26.5 * mm});
            skCircle(sketch, "E1475", {"center": v(-130, -1013.25) * mm, "radius": 26.5 * mm});
            skCircle(sketch, "E1476", {"center": v(-162.5, -1069.54) * mm, "radius": 26.5 * mm});
            skCircle(sketch, "E1477", {"center": v(-195, -1125.83) * mm, "radius": 26.5 * mm});
            skCircle(sketch, "E1478", {"center": v(-227.5, -1182.12) * mm, "radius": 26.5 * mm});
            skCircle(sketch, "E1479", {"center": v(-260, -1238.42) * mm, "radius": 26.5 * mm});
            skCircle(sketch, "E1480", {"center": v(-292.5, -1294.7) * mm, "radius": 26.5 * mm});
            skCircle(sketch, "E1481", {"center": v(-325, -1351) * mm, "radius": 26.5 * mm});
            skCircle(sketch, "E1482", {"center": v(-357.5, -1407.3) * mm, "radius": 26.5 * mm});
            skCircle(sketch, "E1483", {"center": v(-390, -1463.58) * mm, "radius": 26.5 * mm});
            skCircle(sketch, "E1484", {"center": v(-422.5, -1519.87) * mm, "radius": 26.5 * mm});
            skCircle(sketch, "E1485", {"center": v(227.5, -506.62) * mm, "radius": 26.5 * mm});
            skCircle(sketch, "E1486", {"center": v(195, -562.92) * mm, "radius": 26.5 * mm});
            skCircle(sketch, "E1487", {"center": v(162.5, -619.2) * mm, "radius": 26.5 * mm});
            skCircle(sketch, "E1488", {"center": v(130, -675.5) * mm, "radius": 26.5 * mm});
            skCircle(sketch, "E1489", {"center": v(97.5, -731.8) * mm, "radius": 26.5 * mm});
            skCircle(sketch, "E1490", {"center": v(65, -788.08) * mm, "radius": 26.5 * mm});
            skCircle(sketch, "E1491", {"center": v(32.5, -844.37) * mm, "radius": 26.5 * mm});
            skCircle(sketch, "E1492", {"center": v(0, -900.67) * mm, "radius": 26.5 * mm});
            skCircle(sketch, "E1493", {"center": v(-32.5, -956.96) * mm, "radius": 26.5 * mm});
            skCircle(sketch, "E1494", {"center": v(-65, -1013.25) * mm, "radius": 26.5 * mm});
            skCircle(sketch, "E1495", {"center": v(-97.5, -1069.54) * mm, "radius": 26.5 * mm});
            skCircle(sketch, "E1496", {"center": v(-130, -1125.83) * mm, "radius": 26.5 * mm});
            skCircle(sketch, "E1497", {"center": v(-162.5, -1182.12) * mm, "radius": 26.5 * mm});
            skCircle(sketch, "E1498", {"center": v(-195, -1238.42) * mm, "radius": 26.5 * mm});
            skCircle(sketch, "E1499", {"center": v(-227.5, -1294.7) * mm, "radius": 26.5 * mm});
            skCircle(sketch, "E1500", {"center": v(-260, -1351) * mm, "radius": 26.5 * mm});
            skCircle(sketch, "E1501", {"center": v(-292.5, -1407.3) * mm, "radius": 26.5 * mm});
            skCircle(sketch, "E1502", {"center": v(-325, -1463.58) * mm, "radius": 26.5 * mm});
            skCircle(sketch, "E1503", {"center": v(-357.5, -1519.87) * mm, "radius": 26.5 * mm});
            skCircle(sketch, "E1504", {"center": v(260, -562.92) * mm, "radius": 26.5 * mm});
            skCircle(sketch, "E1505", {"center": v(227.5, -619.2) * mm, "radius": 26.5 * mm});
            skCircle(sketch, "E1506", {"center": v(195, -675.5) * mm, "radius": 26.5 * mm});
            skCircle(sketch, "E1507", {"center": v(162.5, -731.8) * mm, "radius": 26.5 * mm});
            skCircle(sketch, "E1508", {"center": v(130, -788.08) * mm, "radius": 26.5 * mm});
            skCircle(sketch, "E1509", {"center": v(97.5, -844.37) * mm, "radius": 26.5 * mm});
            skCircle(sketch, "E1510", {"center": v(65, -900.67) * mm, "radius": 26.5 * mm});
            skCircle(sketch, "E1511", {"center": v(32.5, -956.96) * mm, "radius": 26.5 * mm});
            skCircle(sketch, "E1512", {"center": v(0, -1013.25) * mm, "radius": 26.5 * mm});
            skCircle(sketch, "E1513", {"center": v(-97.5, -1182.12) * mm, "radius": 26.5 * mm});
            skCircle(sketch, "E1514", {"center": v(-130, -1238.42) * mm, "radius": 26.5 * mm});
            skCircle(sketch, "E1515", {"center": v(-162.5, -1294.7) * mm, "radius": 26.5 * mm});
            skCircle(sketch, "E1516", {"center": v(-195, -1351) * mm, "radius": 26.5 * mm});
            skCircle(sketch, "E1517", {"center": v(-227.5, -1407.3) * mm, "radius": 26.5 * mm});
            skCircle(sketch, "E1518", {"center": v(-260, -1463.58) * mm, "radius": 26.5 * mm});
            skCircle(sketch, "E1519", {"center": v(-292.5, -1519.87) * mm, "radius": 26.5 * mm});
            skCircle(sketch, "E1520", {"center": v(292.5, -619.2) * mm, "radius": 26.5 * mm});
            skCircle(sketch, "E1521", {"center": v(260, -675.5) * mm, "radius": 26.5 * mm});
            skCircle(sketch, "E1522", {"center": v(227.5, -731.8) * mm, "radius": 26.5 * mm});
            skCircle(sketch, "E1523", {"center": v(195, -788.08) * mm, "radius": 26.5 * mm});
            skCircle(sketch, "E1524", {"center": v(162.5, -844.37) * mm, "radius": 26.5 * mm});
            skCircle(sketch, "E1525", {"center": v(130, -900.67) * mm, "radius": 26.5 * mm});
            skCircle(sketch, "E1526", {"center": v(97.5, -956.96) * mm, "radius": 26.5 * mm});
            skCircle(sketch, "E1527", {"center": v(65, -1013.25) * mm, "radius": 26.5 * mm});
            skCircle(sketch, "E1528", {"center": v(-65, -1238.42) * mm, "radius": 26.5 * mm});
            skCircle(sketch, "E1529", {"center": v(-97.5, -1294.7) * mm, "radius": 26.5 * mm});
            skCircle(sketch, "E1530", {"center": v(-130, -1351) * mm, "radius": 26.5 * mm});
            skCircle(sketch, "E1531", {"center": v(-162.5, -1407.3) * mm, "radius": 26.5 * mm});
            skCircle(sketch, "E1532", {"center": v(-195, -1463.58) * mm, "radius": 26.5 * mm});
            skCircle(sketch, "E1533", {"center": v(-227.5, -1519.87) * mm, "radius": 26.5 * mm});
            skCircle(sketch, "E1534", {"center": v(325, -675.5) * mm, "radius": 26.5 * mm});
            skCircle(sketch, "E1535", {"center": v(292.5, -731.8) * mm, "radius": 26.5 * mm});
            skCircle(sketch, "E1536", {"center": v(260, -788.08) * mm, "radius": 26.5 * mm});
            skCircle(sketch, "E1537", {"center": v(227.5, -844.37) * mm, "radius": 26.5 * mm});
            skCircle(sketch, "E1538", {"center": v(195, -900.67) * mm, "radius": 26.5 * mm});
            skCircle(sketch, "E1539", {"center": v(162.5, -956.96) * mm, "radius": 26.5 * mm});
            skCircle(sketch, "E1540", {"center": v(130, -1013.25) * mm, "radius": 26.5 * mm});
            skCircle(sketch, "E1541", {"center": v(97.5, -1069.54) * mm, "radius": 26.5 * mm});
            skCircle(sketch, "E1542", {"center": v(0, -1238.42) * mm, "radius": 26.5 * mm});
            skCircle(sketch, "E1543", {"center": v(-32.5, -1294.7) * mm, "radius": 26.5 * mm});
            skCircle(sketch, "E1544", {"center": v(-65, -1351) * mm, "radius": 26.5 * mm});
            skCircle(sketch, "E1545", {"center": v(-97.5, -1407.3) * mm, "radius": 26.5 * mm});
            skCircle(sketch, "E1546", {"center": v(-130, -1463.58) * mm, "radius": 26.5 * mm});
            skCircle(sketch, "E1547", {"center": v(-162.5, -1519.87) * mm, "radius": 26.5 * mm});
            skCircle(sketch, "E1548", {"center": v(357.5, -731.8) * mm, "radius": 26.5 * mm});
            skCircle(sketch, "E1549", {"center": v(325, -788.08) * mm, "radius": 26.5 * mm});
            skCircle(sketch, "E1550", {"center": v(292.5, -844.37) * mm, "radius": 26.5 * mm});
            skCircle(sketch, "E1551", {"center": v(260, -900.67) * mm, "radius": 26.5 * mm});
            skCircle(sketch, "E1552", {"center": v(227.5, -956.96) * mm, "radius": 26.5 * mm});
            skCircle(sketch, "E1553", {"center": v(195, -1013.25) * mm, "radius": 26.5 * mm});
            skCircle(sketch, "E1554", {"center": v(162.5, -1069.54) * mm, "radius": 26.5 * mm});
            skCircle(sketch, "E1555", {"center": v(130, -1125.83) * mm, "radius": 26.5 * mm});
            skCircle(sketch, "E1556", {"center": v(97.5, -1182.12) * mm, "radius": 26.5 * mm});
            skCircle(sketch, "E1557", {"center": v(65, -1238.42) * mm, "radius": 26.5 * mm});
            skCircle(sketch, "E1558", {"center": v(32.5, -1294.7) * mm, "radius": 26.5 * mm});
            skCircle(sketch, "E1559", {"center": v(0, -1351) * mm, "radius": 26.5 * mm});
            skCircle(sketch, "E1560", {"center": v(-32.5, -1407.3) * mm, "radius": 26.5 * mm});
            skCircle(sketch, "E1561", {"center": v(-65, -1463.58) * mm, "radius": 26.5 * mm});
            skCircle(sketch, "E1562", {"center": v(-97.5, -1519.87) * mm, "radius": 26.5 * mm});
            skCircle(sketch, "E1563", {"center": v(390, -788.08) * mm, "radius": 26.5 * mm});
            skCircle(sketch, "E1564", {"center": v(357.5, -844.37) * mm, "radius": 26.5 * mm});
            skCircle(sketch, "E1565", {"center": v(325, -900.67) * mm, "radius": 26.5 * mm});
            skCircle(sketch, "E1566", {"center": v(292.5, -956.96) * mm, "radius": 26.5 * mm});
            skCircle(sketch, "E1567", {"center": v(260, -1013.25) * mm, "radius": 26.5 * mm});
            skCircle(sketch, "E1568", {"center": v(227.5, -1069.54) * mm, "radius": 26.5 * mm});
            skCircle(sketch, "E1569", {"center": v(195, -1125.83) * mm, "radius": 26.5 * mm});
            skCircle(sketch, "E1570", {"center": v(162.5, -1182.12) * mm, "radius": 26.5 * mm});
            skCircle(sketch, "E1571", {"center": v(130, -1238.42) * mm, "radius": 26.5 * mm});
            skCircle(sketch, "E1572", {"center": v(97.5, -1294.7) * mm, "radius": 26.5 * mm});
            skCircle(sketch, "E1573", {"center": v(65, -1351) * mm, "radius": 26.5 * mm});
            skCircle(sketch, "E1574", {"center": v(32.5, -1407.3) * mm, "radius": 26.5 * mm});
            skCircle(sketch, "E1575", {"center": v(0, -1463.58) * mm, "radius": 26.5 * mm});
            skCircle(sketch, "E1576", {"center": v(-32.5, -1519.87) * mm, "radius": 26.5 * mm});
            skCircle(sketch, "E1577", {"center": v(-65, -1576.17) * mm, "radius": 26.5 * mm});
            skCircle(sketch, "E1578", {"center": v(422.5, -844.37) * mm, "radius": 26.5 * mm});
            skCircle(sketch, "E1579", {"center": v(390, -900.67) * mm, "radius": 26.5 * mm});
            skCircle(sketch, "E1580", {"center": v(357.5, -956.96) * mm, "radius": 26.5 * mm});
            skCircle(sketch, "E1581", {"center": v(325, -1013.25) * mm, "radius": 26.5 * mm});
            skCircle(sketch, "E1582", {"center": v(292.5, -1069.54) * mm, "radius": 26.5 * mm});
            skCircle(sketch, "E1583", {"center": v(260, -1125.83) * mm, "radius": 26.5 * mm});
            skCircle(sketch, "E1584", {"center": v(227.5, -1182.12) * mm, "radius": 26.5 * mm});
            skCircle(sketch, "E1585", {"center": v(195, -1238.42) * mm, "radius": 26.5 * mm});
            skCircle(sketch, "E1586", {"center": v(162.5, -1294.7) * mm, "radius": 26.5 * mm});
            skCircle(sketch, "E1587", {"center": v(130, -1351) * mm, "radius": 26.5 * mm});
            skCircle(sketch, "E1588", {"center": v(97.5, -1407.3) * mm, "radius": 26.5 * mm});
            skCircle(sketch, "E1589", {"center": v(65, -1463.58) * mm, "radius": 26.5 * mm});
            skCircle(sketch, "E1590", {"center": v(32.5, -1519.87) * mm, "radius": 26.5 * mm});
            skCircle(sketch, "E1591", {"center": v(0, -1576.17) * mm, "radius": 26.5 * mm});
            skCircle(sketch, "E1592", {"center": v(455, -900.67) * mm, "radius": 26.5 * mm});
            skCircle(sketch, "E1593", {"center": v(422.5, -956.96) * mm, "radius": 26.5 * mm});
            skCircle(sketch, "E1594", {"center": v(390, -1013.25) * mm, "radius": 26.5 * mm});
            skCircle(sketch, "E1595", {"center": v(357.5, -1069.54) * mm, "radius": 26.5 * mm});
            skCircle(sketch, "E1596", {"center": v(325, -1125.83) * mm, "radius": 26.5 * mm});
            skCircle(sketch, "E1597", {"center": v(292.5, -1182.12) * mm, "radius": 26.5 * mm});
            skCircle(sketch, "E1598", {"center": v(260, -1238.42) * mm, "radius": 26.5 * mm});
            skCircle(sketch, "E1599", {"center": v(227.5, -1294.7) * mm, "radius": 26.5 * mm});
            skCircle(sketch, "E1600", {"center": v(195, -1351) * mm, "radius": 26.5 * mm});
            skCircle(sketch, "E1601", {"center": v(162.5, -1407.3) * mm, "radius": 26.5 * mm});
            skCircle(sketch, "E1602", {"center": v(130, -1463.58) * mm, "radius": 26.5 * mm});
            skCircle(sketch, "E1603", {"center": v(97.5, -1519.87) * mm, "radius": 26.5 * mm});
            skCircle(sketch, "E1604", {"center": v(65, -1576.17) * mm, "radius": 26.5 * mm});
            skCircle(sketch, "E1605", {"center": v(487.5, -956.96) * mm, "radius": 26.5 * mm});
            skCircle(sketch, "E1606", {"center": v(455, -1013.25) * mm, "radius": 26.5 * mm});
            skCircle(sketch, "E1607", {"center": v(422.5, -1069.54) * mm, "radius": 26.5 * mm});
            skCircle(sketch, "E1608", {"center": v(390, -1125.83) * mm, "radius": 26.5 * mm});
            skCircle(sketch, "E1609", {"center": v(357.5, -1182.12) * mm, "radius": 26.5 * mm});
            skCircle(sketch, "E1610", {"center": v(325, -1238.42) * mm, "radius": 26.5 * mm});
            skCircle(sketch, "E1611", {"center": v(292.5, -1294.7) * mm, "radius": 26.5 * mm});
            skCircle(sketch, "E1612", {"center": v(260, -1351) * mm, "radius": 26.5 * mm});
            skCircle(sketch, "E1613", {"center": v(227.5, -1407.3) * mm, "radius": 26.5 * mm});
            skCircle(sketch, "E1614", {"center": v(195, -1463.58) * mm, "radius": 26.5 * mm});
            skCircle(sketch, "E1615", {"center": v(162.5, -1519.87) * mm, "radius": 26.5 * mm});
            skCircle(sketch, "E1616", {"center": v(520, -1013.25) * mm, "radius": 26.5 * mm});
            skCircle(sketch, "E1617", {"center": v(487.5, -1069.54) * mm, "radius": 26.5 * mm});
            skCircle(sketch, "E1618", {"center": v(455, -1125.83) * mm, "radius": 26.5 * mm});
            skCircle(sketch, "E1619", {"center": v(422.5, -1182.12) * mm, "radius": 26.5 * mm});
            skCircle(sketch, "E1620", {"center": v(390, -1238.42) * mm, "radius": 26.5 * mm});
            skCircle(sketch, "E1621", {"center": v(357.5, -1294.7) * mm, "radius": 26.5 * mm});
            skCircle(sketch, "E1622", {"center": v(325, -1351) * mm, "radius": 26.5 * mm});
            skCircle(sketch, "E1623", {"center": v(292.5, -1407.3) * mm, "radius": 26.5 * mm});
            skCircle(sketch, "E1624", {"center": v(260, -1463.58) * mm, "radius": 26.5 * mm});
            skCircle(sketch, "E1625", {"center": v(227.5, -1519.87) * mm, "radius": 26.5 * mm});
            skCircle(sketch, "E1626", {"center": v(552.5, -1069.54) * mm, "radius": 26.5 * mm});
            skCircle(sketch, "E1627", {"center": v(520, -1125.83) * mm, "radius": 26.5 * mm});
            skCircle(sketch, "E1628", {"center": v(487.5, -1182.12) * mm, "radius": 26.5 * mm});
            skCircle(sketch, "E1629", {"center": v(455, -1238.42) * mm, "radius": 26.5 * mm});
            skCircle(sketch, "E1630", {"center": v(422.5, -1294.7) * mm, "radius": 26.5 * mm});
            skCircle(sketch, "E1631", {"center": v(390, -1351) * mm, "radius": 26.5 * mm});
            skCircle(sketch, "E1632", {"center": v(357.5, -1407.3) * mm, "radius": 26.5 * mm});
            skCircle(sketch, "E1633", {"center": v(325, -1463.58) * mm, "radius": 26.5 * mm});
            skCircle(sketch, "E1634", {"center": v(292.5, -1519.87) * mm, "radius": 26.5 * mm});
            skCircle(sketch, "E1635", {"center": v(585, -1125.83) * mm, "radius": 26.5 * mm});
            skCircle(sketch, "E1636", {"center": v(552.5, -1182.12) * mm, "radius": 26.5 * mm});
            skCircle(sketch, "E1637", {"center": v(520, -1238.42) * mm, "radius": 26.5 * mm});
            skCircle(sketch, "E1638", {"center": v(487.5, -1294.7) * mm, "radius": 26.5 * mm});
            skCircle(sketch, "E1639", {"center": v(455, -1351) * mm, "radius": 26.5 * mm});
            skCircle(sketch, "E1640", {"center": v(422.5, -1407.3) * mm, "radius": 26.5 * mm});
            skCircle(sketch, "E1641", {"center": v(390, -1463.58) * mm, "radius": 26.5 * mm});
            skCircle(sketch, "E1642", {"center": v(357.5, -1519.87) * mm, "radius": 26.5 * mm});
            skCircle(sketch, "E1643", {"center": v(617.5, -1182.12) * mm, "radius": 26.5 * mm});
            skCircle(sketch, "E1644", {"center": v(585, -1238.42) * mm, "radius": 26.5 * mm});
            skCircle(sketch, "E1645", {"center": v(552.5, -1294.7) * mm, "radius": 26.5 * mm});
            skCircle(sketch, "E1646", {"center": v(520, -1351) * mm, "radius": 26.5 * mm});
            skCircle(sketch, "E1647", {"center": v(487.5, -1407.3) * mm, "radius": 26.5 * mm});
            skCircle(sketch, "E1648", {"center": v(455, -1463.58) * mm, "radius": 26.5 * mm});
            skCircle(sketch, "E1649", {"center": v(422.5, -1519.87) * mm, "radius": 26.5 * mm});
            skCircle(sketch, "E1650", {"center": v(650, -1238.42) * mm, "radius": 26.5 * mm});
            skCircle(sketch, "E1651", {"center": v(617.5, -1294.7) * mm, "radius": 26.5 * mm});
            skCircle(sketch, "E1652", {"center": v(585, -1351) * mm, "radius": 26.5 * mm});
            skCircle(sketch, "E1653", {"center": v(552.5, -1407.3) * mm, "radius": 26.5 * mm});
            skCircle(sketch, "E1654", {"center": v(520, -1463.58) * mm, "radius": 26.5 * mm});
            skCircle(sketch, "E1655", {"center": v(682.5, -1294.7) * mm, "radius": 26.5 * mm});
            skCircle(sketch, "E1656", {"center": v(650, -1351) * mm, "radius": 26.5 * mm});
            skCircle(sketch, "E1657", {"center": v(617.5, -1407.3) * mm, "radius": 26.5 * mm});
            skCircle(sketch, "E1658", {"center": v(585, -1463.58) * mm, "radius": 26.5 * mm});
            skCircle(sketch, "E1659", {"center": v(715, -1351) * mm, "radius": 26.5 * mm});
            skCircle(sketch, "E1660", {"center": v(682.5, -1407.3) * mm, "radius": 26.5 * mm});
            skCircle(sketch, "E1661", {"center": v(0, -1125.83) * mm, "radius": 58 * mm});
            skCircle(sketch, "E1662", {"center": v(195, -337.75) * mm, "radius": 26.5 * mm});
            skCircle(sketch, "E1663", {"center": v(227.5, -394.04) * mm, "radius": 26.5 * mm});
            skCircle(sketch, "E1664", {"center": v(260, -450.33) * mm, "radius": 26.5 * mm});
            skCircle(sketch, "E1665", {"center": v(292.5, -506.62) * mm, "radius": 26.5 * mm});
            skCircle(sketch, "E1666", {"center": v(325, -562.92) * mm, "radius": 26.5 * mm});
            skCircle(sketch, "E1667", {"center": v(357.5, -619.2) * mm, "radius": 26.5 * mm});
            skCircle(sketch, "E1668", {"center": v(390, -675.5) * mm, "radius": 26.5 * mm});
            skCircle(sketch, "E1669", {"center": v(422.5, -731.8) * mm, "radius": 26.5 * mm});
            skCircle(sketch, "E1670", {"center": v(455, -788.08) * mm, "radius": 26.5 * mm});
            skCircle(sketch, "E1671", {"center": v(487.5, -844.37) * mm, "radius": 26.5 * mm});
            skCircle(sketch, "E1672", {"center": v(520, -900.67) * mm, "radius": 26.5 * mm});
            skCircle(sketch, "E1673", {"center": v(552.5, -956.96) * mm, "radius": 26.5 * mm});
            skCircle(sketch, "E1674", {"center": v(585, -1013.25) * mm, "radius": 26.5 * mm});
            skCircle(sketch, "E1675", {"center": v(617.5, -1069.54) * mm, "radius": 26.5 * mm});
            skCircle(sketch, "E1676", {"center": v(650, -1125.83) * mm, "radius": 26.5 * mm});
            skCircle(sketch, "E1677", {"center": v(682.5, -1182.12) * mm, "radius": 26.5 * mm});
            skCircle(sketch, "E1678", {"center": v(715, -1238.42) * mm, "radius": 26.5 * mm});
            skCircle(sketch, "E1679", {"center": v(747.5, -1294.7) * mm, "radius": 26.5 * mm});
            skCircle(sketch, "E1680", {"center": v(780, -1351) * mm, "radius": 26.5 * mm});
            skCircle(sketch, "E1681", {"center": v(260, -337.75) * mm, "radius": 26.5 * mm});
            skCircle(sketch, "E1682", {"center": v(292.5, -394.04) * mm, "radius": 26.5 * mm});
            skCircle(sketch, "E1683", {"center": v(325, -450.33) * mm, "radius": 26.5 * mm});
            skCircle(sketch, "E1684", {"center": v(357.5, -506.62) * mm, "radius": 26.5 * mm});
            skCircle(sketch, "E1685", {"center": v(390, -562.92) * mm, "radius": 26.5 * mm});
            skCircle(sketch, "E1686", {"center": v(422.5, -619.2) * mm, "radius": 26.5 * mm});
            skCircle(sketch, "E1687", {"center": v(455, -675.5) * mm, "radius": 26.5 * mm});
            skCircle(sketch, "E1688", {"center": v(487.5, -731.8) * mm, "radius": 26.5 * mm});
            skCircle(sketch, "E1689", {"center": v(520, -788.08) * mm, "radius": 26.5 * mm});
            skCircle(sketch, "E1690", {"center": v(552.5, -844.37) * mm, "radius": 26.5 * mm});
            skCircle(sketch, "E1691", {"center": v(585, -900.67) * mm, "radius": 26.5 * mm});
            skCircle(sketch, "E1692", {"center": v(617.5, -956.96) * mm, "radius": 26.5 * mm});
            skCircle(sketch, "E1693", {"center": v(650, -1013.25) * mm, "radius": 26.5 * mm});
            skCircle(sketch, "E1694", {"center": v(682.5, -1069.54) * mm, "radius": 26.5 * mm});
            skCircle(sketch, "E1695", {"center": v(715, -1125.83) * mm, "radius": 26.5 * mm});
            skCircle(sketch, "E1696", {"center": v(747.5, -1182.12) * mm, "radius": 26.5 * mm});
            skCircle(sketch, "E1697", {"center": v(780, -1238.42) * mm, "radius": 26.5 * mm});
            skCircle(sketch, "E1698", {"center": v(812.5, -1294.7) * mm, "radius": 26.5 * mm});
            skCircle(sketch, "E1699", {"center": v(292.5, -281.46) * mm, "radius": 26.5 * mm});
            skCircle(sketch, "E1700", {"center": v(325, -337.75) * mm, "radius": 26.5 * mm});
            skCircle(sketch, "E1701", {"center": v(357.5, -394.04) * mm, "radius": 26.5 * mm});
            skCircle(sketch, "E1702", {"center": v(390, -450.33) * mm, "radius": 26.5 * mm});
            skCircle(sketch, "E1703", {"center": v(422.5, -506.62) * mm, "radius": 26.5 * mm});
            skCircle(sketch, "E1704", {"center": v(455, -562.92) * mm, "radius": 26.5 * mm});
            skCircle(sketch, "E1705", {"center": v(487.5, -619.2) * mm, "radius": 26.5 * mm});
            skCircle(sketch, "E1706", {"center": v(520, -675.5) * mm, "radius": 26.5 * mm});
            skCircle(sketch, "E1707", {"center": v(552.5, -731.8) * mm, "radius": 26.5 * mm});
            skCircle(sketch, "E1708", {"center": v(585, -788.08) * mm, "radius": 26.5 * mm});
            skCircle(sketch, "E1709", {"center": v(617.5, -844.37) * mm, "radius": 26.5 * mm});
            skCircle(sketch, "E1710", {"center": v(650, -900.67) * mm, "radius": 26.5 * mm});
            skCircle(sketch, "E1711", {"center": v(682.5, -956.96) * mm, "radius": 26.5 * mm});
            skCircle(sketch, "E1712", {"center": v(715, -1013.25) * mm, "radius": 26.5 * mm});
            skCircle(sketch, "E1713", {"center": v(747.5, -1069.54) * mm, "radius": 26.5 * mm});
            skCircle(sketch, "E1714", {"center": v(780, -1125.83) * mm, "radius": 26.5 * mm});
            skCircle(sketch, "E1715", {"center": v(812.5, -1182.12) * mm, "radius": 26.5 * mm});
            skCircle(sketch, "E1716", {"center": v(845, -1238.42) * mm, "radius": 26.5 * mm});
            skCircle(sketch, "E1717", {"center": v(877.5, -1294.7) * mm, "radius": 26.5 * mm});
            skCircle(sketch, "E1718", {"center": v(325, -225.17) * mm, "radius": 26.5 * mm});
            skCircle(sketch, "E1719", {"center": v(357.5, -281.46) * mm, "radius": 26.5 * mm});
            skCircle(sketch, "E1720", {"center": v(390, -337.75) * mm, "radius": 26.5 * mm});
            skCircle(sketch, "E1721", {"center": v(422.5, -394.04) * mm, "radius": 26.5 * mm});
            skCircle(sketch, "E1722", {"center": v(455, -450.33) * mm, "radius": 26.5 * mm});
            skCircle(sketch, "E1723", {"center": v(487.5, -506.62) * mm, "radius": 26.5 * mm});
            skCircle(sketch, "E1724", {"center": v(520, -562.92) * mm, "radius": 26.5 * mm});
            skCircle(sketch, "E1725", {"center": v(552.5, -619.2) * mm, "radius": 26.5 * mm});
            skCircle(sketch, "E1726", {"center": v(585, -675.5) * mm, "radius": 26.5 * mm});
            skCircle(sketch, "E1727", {"center": v(617.5, -731.8) * mm, "radius": 26.5 * mm});
            skCircle(sketch, "E1728", {"center": v(650, -788.08) * mm, "radius": 26.5 * mm});
            skCircle(sketch, "E1729", {"center": v(682.5, -844.37) * mm, "radius": 26.5 * mm});
            skCircle(sketch, "E1730", {"center": v(715, -900.67) * mm, "radius": 26.5 * mm});
            skCircle(sketch, "E1731", {"center": v(747.5, -956.96) * mm, "radius": 26.5 * mm});
            skCircle(sketch, "E1732", {"center": v(780, -1013.25) * mm, "radius": 26.5 * mm});
            skCircle(sketch, "E1733", {"center": v(812.5, -1069.54) * mm, "radius": 26.5 * mm});
            skCircle(sketch, "E1734", {"center": v(845, -1125.83) * mm, "radius": 26.5 * mm});
            skCircle(sketch, "E1735", {"center": v(877.5, -1182.12) * mm, "radius": 26.5 * mm});
            skCircle(sketch, "E1736", {"center": v(910, -1238.42) * mm, "radius": 26.5 * mm});
            skCircle(sketch, "E1737", {"center": v(357.5, -168.87) * mm, "radius": 26.5 * mm});
            skCircle(sketch, "E1738", {"center": v(390, -225.17) * mm, "radius": 26.5 * mm});
            skCircle(sketch, "E1739", {"center": v(422.5, -281.46) * mm, "radius": 26.5 * mm});
            skCircle(sketch, "E1740", {"center": v(455, -337.75) * mm, "radius": 26.5 * mm});
            skCircle(sketch, "E1741", {"center": v(487.5, -394.04) * mm, "radius": 26.5 * mm});
            skCircle(sketch, "E1742", {"center": v(520, -450.33) * mm, "radius": 26.5 * mm});
            skCircle(sketch, "E1743", {"center": v(552.5, -506.62) * mm, "radius": 26.5 * mm});
            skCircle(sketch, "E1744", {"center": v(585, -562.92) * mm, "radius": 26.5 * mm});
            skCircle(sketch, "E1745", {"center": v(617.5, -619.2) * mm, "radius": 26.5 * mm});
            skCircle(sketch, "E1746", {"center": v(650, -675.5) * mm, "radius": 26.5 * mm});
            skCircle(sketch, "E1747", {"center": v(682.5, -731.8) * mm, "radius": 26.5 * mm});
            skCircle(sketch, "E1748", {"center": v(715, -788.08) * mm, "radius": 26.5 * mm});
            skCircle(sketch, "E1749", {"center": v(747.5, -844.37) * mm, "radius": 26.5 * mm});
            skCircle(sketch, "E1750", {"center": v(780, -900.67) * mm, "radius": 26.5 * mm});
            skCircle(sketch, "E1751", {"center": v(812.5, -956.96) * mm, "radius": 26.5 * mm});
            skCircle(sketch, "E1752", {"center": v(845, -1013.25) * mm, "radius": 26.5 * mm});
            skCircle(sketch, "E1753", {"center": v(877.5, -1069.54) * mm, "radius": 26.5 * mm});
            skCircle(sketch, "E1754", {"center": v(910, -1125.83) * mm, "radius": 26.5 * mm});
            skCircle(sketch, "E1755", {"center": v(942.5, -1182.12) * mm, "radius": 26.5 * mm});
            skCircle(sketch, "E1756", {"center": v(975, -1238.42) * mm, "radius": 26.5 * mm});
            skCircle(sketch, "E1757", {"center": v(390, -112.58) * mm, "radius": 26.5 * mm});
            skCircle(sketch, "E1758", {"center": v(422.5, -168.87) * mm, "radius": 26.5 * mm});
            skCircle(sketch, "E1759", {"center": v(455, -225.17) * mm, "radius": 26.5 * mm});
            skCircle(sketch, "E1760", {"center": v(487.5, -281.46) * mm, "radius": 26.5 * mm});
            skCircle(sketch, "E1761", {"center": v(520, -337.75) * mm, "radius": 26.5 * mm});
            skCircle(sketch, "E1762", {"center": v(552.5, -394.04) * mm, "radius": 26.5 * mm});
            skCircle(sketch, "E1763", {"center": v(585, -450.33) * mm, "radius": 26.5 * mm});
            skCircle(sketch, "E1764", {"center": v(617.5, -506.62) * mm, "radius": 26.5 * mm});
            skCircle(sketch, "E1765", {"center": v(650, -562.92) * mm, "radius": 26.5 * mm});
            skCircle(sketch, "E1766", {"center": v(682.5, -619.2) * mm, "radius": 26.5 * mm});
            skCircle(sketch, "E1767", {"center": v(715, -675.5) * mm, "radius": 26.5 * mm});
            skCircle(sketch, "E1768", {"center": v(747.5, -731.8) * mm, "radius": 26.5 * mm});
            skCircle(sketch, "E1769", {"center": v(780, -788.08) * mm, "radius": 26.5 * mm});
            skCircle(sketch, "E1770", {"center": v(812.5, -844.37) * mm, "radius": 26.5 * mm});
            skCircle(sketch, "E1771", {"center": v(845, -900.67) * mm, "radius": 26.5 * mm});
            skCircle(sketch, "E1772", {"center": v(877.5, -956.96) * mm, "radius": 26.5 * mm});
            skCircle(sketch, "E1773", {"center": v(910, -1013.25) * mm, "radius": 26.5 * mm});
            skCircle(sketch, "E1774", {"center": v(942.5, -1069.54) * mm, "radius": 26.5 * mm});
            skCircle(sketch, "E1775", {"center": v(975, -1125.83) * mm, "radius": 26.5 * mm});
            skCircle(sketch, "E1776", {"center": v(1007.5, -1182.12) * mm, "radius": 26.5 * mm});
            skCircle(sketch, "E1777", {"center": v(422.5, -56.3) * mm, "radius": 26.5 * mm});
            skCircle(sketch, "E1778", {"center": v(455, -112.58) * mm, "radius": 26.5 * mm});
            skCircle(sketch, "E1779", {"center": v(487.5, -168.87) * mm, "radius": 26.5 * mm});
            skCircle(sketch, "E1780", {"center": v(520, -225.17) * mm, "radius": 26.5 * mm});
            skCircle(sketch, "E1781", {"center": v(552.5, -281.46) * mm, "radius": 26.5 * mm});
            skCircle(sketch, "E1782", {"center": v(585, -337.75) * mm, "radius": 26.5 * mm});
            skCircle(sketch, "E1783", {"center": v(617.5, -394.04) * mm, "radius": 26.5 * mm});
            skCircle(sketch, "E1784", {"center": v(650, -450.33) * mm, "radius": 26.5 * mm});
            skCircle(sketch, "E1785", {"center": v(682.5, -506.62) * mm, "radius": 26.5 * mm});
            skCircle(sketch, "E1786", {"center": v(715, -562.92) * mm, "radius": 26.5 * mm});
            skCircle(sketch, "E1787", {"center": v(747.5, -619.2) * mm, "radius": 26.5 * mm});
            skCircle(sketch, "E1788", {"center": v(780, -675.5) * mm, "radius": 26.5 * mm});
            skCircle(sketch, "E1789", {"center": v(812.5, -731.8) * mm, "radius": 26.5 * mm});
            skCircle(sketch, "E1790", {"center": v(845, -788.08) * mm, "radius": 26.5 * mm});
            skCircle(sketch, "E1791", {"center": v(877.5, -844.37) * mm, "radius": 26.5 * mm});
            skCircle(sketch, "E1792", {"center": v(910, -900.67) * mm, "radius": 26.5 * mm});
            skCircle(sketch, "E1793", {"center": v(942.5, -956.96) * mm, "radius": 26.5 * mm});
            skCircle(sketch, "E1794", {"center": v(975, -1013.25) * mm, "radius": 26.5 * mm});
            skCircle(sketch, "E1795", {"center": v(1007.5, -1069.54) * mm, "radius": 26.5 * mm});
            skCircle(sketch, "E1796", {"center": v(1040, -1125.83) * mm, "radius": 26.5 * mm});
            skCircle(sketch, "E1797", {"center": v(487.5, -56.3) * mm, "radius": 26.5 * mm});
            skCircle(sketch, "E1798", {"center": v(520, -112.58) * mm, "radius": 26.5 * mm});
            skCircle(sketch, "E1799", {"center": v(552.5, -168.87) * mm, "radius": 26.5 * mm});
            skCircle(sketch, "E1800", {"center": v(585, -225.17) * mm, "radius": 26.5 * mm});
            skCircle(sketch, "E1801", {"center": v(617.5, -281.46) * mm, "radius": 26.5 * mm});
            skCircle(sketch, "E1802", {"center": v(650, -337.75) * mm, "radius": 26.5 * mm});
            skCircle(sketch, "E1803", {"center": v(682.5, -394.04) * mm, "radius": 26.5 * mm});
            skCircle(sketch, "E1804", {"center": v(715, -450.33) * mm, "radius": 26.5 * mm});
            skCircle(sketch, "E1805", {"center": v(747.5, -506.62) * mm, "radius": 26.5 * mm});
            skCircle(sketch, "E1806", {"center": v(780, -562.92) * mm, "radius": 26.5 * mm});
            skCircle(sketch, "E1807", {"center": v(812.5, -619.2) * mm, "radius": 26.5 * mm});
            skCircle(sketch, "E1808", {"center": v(845, -675.5) * mm, "radius": 26.5 * mm});
            skCircle(sketch, "E1809", {"center": v(877.5, -731.8) * mm, "radius": 26.5 * mm});
            skCircle(sketch, "E1810", {"center": v(910, -788.08) * mm, "radius": 26.5 * mm});
            skCircle(sketch, "E1811", {"center": v(942.5, -844.37) * mm, "radius": 26.5 * mm});
            skCircle(sketch, "E1812", {"center": v(975, -900.67) * mm, "radius": 26.5 * mm});
            skCircle(sketch, "E1813", {"center": v(1007.5, -956.96) * mm, "radius": 26.5 * mm});
            skCircle(sketch, "E1814", {"center": v(1040, -1013.25) * mm, "radius": 26.5 * mm});
            skCircle(sketch, "E1815", {"center": v(1072.5, -1069.54) * mm, "radius": 26.5 * mm});
            skCircle(sketch, "E1816", {"center": v(1105, -1125.83) * mm, "radius": 26.5 * mm});
            skCircle(sketch, "E1817", {"center": v(552.5, -56.3) * mm, "radius": 26.5 * mm});
            skCircle(sketch, "E1818", {"center": v(585, -112.58) * mm, "radius": 26.5 * mm});
            skCircle(sketch, "E1819", {"center": v(617.5, -168.87) * mm, "radius": 26.5 * mm});
            skCircle(sketch, "E1820", {"center": v(650, -225.17) * mm, "radius": 26.5 * mm});
            skCircle(sketch, "E1821", {"center": v(682.5, -281.46) * mm, "radius": 26.5 * mm});
            skCircle(sketch, "E1822", {"center": v(715, -337.75) * mm, "radius": 26.5 * mm});
            skCircle(sketch, "E1823", {"center": v(747.5, -394.04) * mm, "radius": 26.5 * mm});
            skCircle(sketch, "E1824", {"center": v(780, -450.33) * mm, "radius": 26.5 * mm});
            skCircle(sketch, "E1825", {"center": v(812.5, -506.62) * mm, "radius": 26.5 * mm});
            skCircle(sketch, "E1826", {"center": v(845, -562.92) * mm, "radius": 26.5 * mm});
            skCircle(sketch, "E1827", {"center": v(877.5, -619.2) * mm, "radius": 26.5 * mm});
            skCircle(sketch, "E1828", {"center": v(910, -675.5) * mm, "radius": 26.5 * mm});
            skCircle(sketch, "E1829", {"center": v(942.5, -731.8) * mm, "radius": 26.5 * mm});
            skCircle(sketch, "E1830", {"center": v(975, -788.08) * mm, "radius": 26.5 * mm});
            skCircle(sketch, "E1831", {"center": v(1007.5, -844.37) * mm, "radius": 26.5 * mm});
            skCircle(sketch, "E1832", {"center": v(1040, -900.67) * mm, "radius": 26.5 * mm});
            skCircle(sketch, "E1833", {"center": v(1072.5, -956.96) * mm, "radius": 26.5 * mm});
            skCircle(sketch, "E1834", {"center": v(1105, -1013.25) * mm, "radius": 26.5 * mm});
            skCircle(sketch, "E1835", {"center": v(1137.5, -1069.54) * mm, "radius": 26.5 * mm});
            skCircle(sketch, "E1836", {"center": v(617.5, -56.3) * mm, "radius": 26.5 * mm});
            skCircle(sketch, "E1837", {"center": v(650, -112.58) * mm, "radius": 26.5 * mm});
            skCircle(sketch, "E1838", {"center": v(682.5, -168.87) * mm, "radius": 26.5 * mm});
            skCircle(sketch, "E1839", {"center": v(715, -225.17) * mm, "radius": 26.5 * mm});
            skCircle(sketch, "E1840", {"center": v(747.5, -281.46) * mm, "radius": 26.5 * mm});
            skCircle(sketch, "E1841", {"center": v(780, -337.75) * mm, "radius": 26.5 * mm});
            skCircle(sketch, "E1842", {"center": v(812.5, -394.04) * mm, "radius": 26.5 * mm});
            skCircle(sketch, "E1843", {"center": v(845, -450.33) * mm, "radius": 26.5 * mm});
            skCircle(sketch, "E1844", {"center": v(877.5, -506.62) * mm, "radius": 26.5 * mm});
            skCircle(sketch, "E1845", {"center": v(975, -675.5) * mm, "radius": 26.5 * mm});
            skCircle(sketch, "E1846", {"center": v(1007.5, -731.8) * mm, "radius": 26.5 * mm});
            skCircle(sketch, "E1847", {"center": v(1040, -788.08) * mm, "radius": 26.5 * mm});
            skCircle(sketch, "E1848", {"center": v(1072.5, -844.37) * mm, "radius": 26.5 * mm});
            skCircle(sketch, "E1849", {"center": v(1105, -900.67) * mm, "radius": 26.5 * mm});
            skCircle(sketch, "E1850", {"center": v(1137.5, -956.96) * mm, "radius": 26.5 * mm});
            skCircle(sketch, "E1851", {"center": v(1170, -1013.25) * mm, "radius": 26.5 * mm});
            skCircle(sketch, "E1852", {"center": v(682.5, -56.3) * mm, "radius": 26.5 * mm});
            skCircle(sketch, "E1853", {"center": v(715, -112.58) * mm, "radius": 26.5 * mm});
            skCircle(sketch, "E1854", {"center": v(747.5, -168.87) * mm, "radius": 26.5 * mm});
            skCircle(sketch, "E1855", {"center": v(780, -225.17) * mm, "radius": 26.5 * mm});
            skCircle(sketch, "E1856", {"center": v(812.5, -281.46) * mm, "radius": 26.5 * mm});
            skCircle(sketch, "E1857", {"center": v(845, -337.75) * mm, "radius": 26.5 * mm});
            skCircle(sketch, "E1858", {"center": v(877.5, -394.04) * mm, "radius": 26.5 * mm});
            skCircle(sketch, "E1859", {"center": v(910, -450.33) * mm, "radius": 26.5 * mm});
            skCircle(sketch, "E1860", {"center": v(1040, -675.5) * mm, "radius": 26.5 * mm});
            skCircle(sketch, "E1861", {"center": v(1072.5, -731.8) * mm, "radius": 26.5 * mm});
            skCircle(sketch, "E1862", {"center": v(1105, -788.08) * mm, "radius": 26.5 * mm});
            skCircle(sketch, "E1863", {"center": v(1137.5, -844.37) * mm, "radius": 26.5 * mm});
            skCircle(sketch, "E1864", {"center": v(1170, -900.67) * mm, "radius": 26.5 * mm});
            skCircle(sketch, "E1865", {"center": v(1202.5, -956.96) * mm, "radius": 26.5 * mm});
            skCircle(sketch, "E1866", {"center": v(747.5, -56.3) * mm, "radius": 26.5 * mm});
            skCircle(sketch, "E1867", {"center": v(780, -112.58) * mm, "radius": 26.5 * mm});
            skCircle(sketch, "E1868", {"center": v(812.5, -168.87) * mm, "radius": 26.5 * mm});
            skCircle(sketch, "E1869", {"center": v(845, -225.17) * mm, "radius": 26.5 * mm});
            skCircle(sketch, "E1870", {"center": v(877.5, -281.46) * mm, "radius": 26.5 * mm});
            skCircle(sketch, "E1871", {"center": v(910, -337.75) * mm, "radius": 26.5 * mm});
            skCircle(sketch, "E1872", {"center": v(942.5, -394.04) * mm, "radius": 26.5 * mm});
            skCircle(sketch, "E1873", {"center": v(975, -450.33) * mm, "radius": 26.5 * mm});
            skCircle(sketch, "E1874", {"center": v(1072.5, -619.2) * mm, "radius": 26.5 * mm});
            skCircle(sketch, "E1875", {"center": v(1105, -675.5) * mm, "radius": 26.5 * mm});
            skCircle(sketch, "E1876", {"center": v(1137.5, -731.8) * mm, "radius": 26.5 * mm});
            skCircle(sketch, "E1877", {"center": v(1170, -788.08) * mm, "radius": 26.5 * mm});
            skCircle(sketch, "E1878", {"center": v(1202.5, -844.37) * mm, "radius": 26.5 * mm});
            skCircle(sketch, "E1879", {"center": v(1235, -900.67) * mm, "radius": 26.5 * mm});
            skCircle(sketch, "E1880", {"center": v(812.5, -56.3) * mm, "radius": 26.5 * mm});
            skCircle(sketch, "E1881", {"center": v(845, -112.58) * mm, "radius": 26.5 * mm});
            skCircle(sketch, "E1882", {"center": v(877.5, -168.87) * mm, "radius": 26.5 * mm});
            skCircle(sketch, "E1883", {"center": v(910, -225.17) * mm, "radius": 26.5 * mm});
            skCircle(sketch, "E1884", {"center": v(942.5, -281.46) * mm, "radius": 26.5 * mm});
            skCircle(sketch, "E1885", {"center": v(975, -337.75) * mm, "radius": 26.5 * mm});
            skCircle(sketch, "E1886", {"center": v(1007.5, -394.04) * mm, "radius": 26.5 * mm});
            skCircle(sketch, "E1887", {"center": v(1040, -450.33) * mm, "radius": 26.5 * mm});
            skCircle(sketch, "E1888", {"center": v(1072.5, -506.62) * mm, "radius": 26.5 * mm});
            skCircle(sketch, "E1889", {"center": v(1105, -562.92) * mm, "radius": 26.5 * mm});
            skCircle(sketch, "E1890", {"center": v(1137.5, -619.2) * mm, "radius": 26.5 * mm});
            skCircle(sketch, "E1891", {"center": v(1170, -675.5) * mm, "radius": 26.5 * mm});
            skCircle(sketch, "E1892", {"center": v(1202.5, -731.8) * mm, "radius": 26.5 * mm});
            skCircle(sketch, "E1893", {"center": v(1235, -788.08) * mm, "radius": 26.5 * mm});
            skCircle(sketch, "E1894", {"center": v(1267.5, -844.37) * mm, "radius": 26.5 * mm});
            skCircle(sketch, "E1895", {"center": v(877.5, -56.3) * mm, "radius": 26.5 * mm});
            skCircle(sketch, "E1896", {"center": v(910, -112.58) * mm, "radius": 26.5 * mm});
            skCircle(sketch, "E1897", {"center": v(942.5, -168.87) * mm, "radius": 26.5 * mm});
            skCircle(sketch, "E1898", {"center": v(975, -225.17) * mm, "radius": 26.5 * mm});
            skCircle(sketch, "E1899", {"center": v(1007.5, -281.46) * mm, "radius": 26.5 * mm});
            skCircle(sketch, "E1900", {"center": v(1040, -337.75) * mm, "radius": 26.5 * mm});
            skCircle(sketch, "E1901", {"center": v(1072.5, -394.04) * mm, "radius": 26.5 * mm});
            skCircle(sketch, "E1902", {"center": v(1105, -450.33) * mm, "radius": 26.5 * mm});
            skCircle(sketch, "E1903", {"center": v(1137.5, -506.62) * mm, "radius": 26.5 * mm});
            skCircle(sketch, "E1904", {"center": v(1170, -562.92) * mm, "radius": 26.5 * mm});
            skCircle(sketch, "E1905", {"center": v(1202.5, -619.2) * mm, "radius": 26.5 * mm});
            skCircle(sketch, "E1906", {"center": v(1235, -675.5) * mm, "radius": 26.5 * mm});
            skCircle(sketch, "E1907", {"center": v(1267.5, -731.8) * mm, "radius": 26.5 * mm});
            skCircle(sketch, "E1908", {"center": v(1300, -788.08) * mm, "radius": 26.5 * mm});
            skCircle(sketch, "E1909", {"center": v(1332.5, -844.37) * mm, "radius": 26.5 * mm});
            skCircle(sketch, "E1910", {"center": v(942.5, -56.3) * mm, "radius": 26.5 * mm});
            skCircle(sketch, "E1911", {"center": v(975, -112.58) * mm, "radius": 26.5 * mm});
            skCircle(sketch, "E1912", {"center": v(1007.5, -168.87) * mm, "radius": 26.5 * mm});
            skCircle(sketch, "E1913", {"center": v(1040, -225.17) * mm, "radius": 26.5 * mm});
            skCircle(sketch, "E1914", {"center": v(1072.5, -281.46) * mm, "radius": 26.5 * mm});
            skCircle(sketch, "E1915", {"center": v(1105, -337.75) * mm, "radius": 26.5 * mm});
            skCircle(sketch, "E1916", {"center": v(1137.5, -394.04) * mm, "radius": 26.5 * mm});
            skCircle(sketch, "E1917", {"center": v(1170, -450.33) * mm, "radius": 26.5 * mm});
            skCircle(sketch, "E1918", {"center": v(1202.5, -506.62) * mm, "radius": 26.5 * mm});
            skCircle(sketch, "E1919", {"center": v(1235, -562.92) * mm, "radius": 26.5 * mm});
            skCircle(sketch, "E1920", {"center": v(1267.5, -619.2) * mm, "radius": 26.5 * mm});
            skCircle(sketch, "E1921", {"center": v(1300, -675.5) * mm, "radius": 26.5 * mm});
            skCircle(sketch, "E1922", {"center": v(1332.5, -731.8) * mm, "radius": 26.5 * mm});
            skCircle(sketch, "E1923", {"center": v(1365, -788.08) * mm, "radius": 26.5 * mm});
            skCircle(sketch, "E1924", {"center": v(1007.5, -56.3) * mm, "radius": 26.5 * mm});
            skCircle(sketch, "E1925", {"center": v(1040, -112.58) * mm, "radius": 26.5 * mm});
            skCircle(sketch, "E1926", {"center": v(1072.5, -168.87) * mm, "radius": 26.5 * mm});
            skCircle(sketch, "E1927", {"center": v(1105, -225.17) * mm, "radius": 26.5 * mm});
            skCircle(sketch, "E1928", {"center": v(1137.5, -281.46) * mm, "radius": 26.5 * mm});
            skCircle(sketch, "E1929", {"center": v(1170, -337.75) * mm, "radius": 26.5 * mm});
            skCircle(sketch, "E1930", {"center": v(1202.5, -394.04) * mm, "radius": 26.5 * mm});
            skCircle(sketch, "E1931", {"center": v(1235, -450.33) * mm, "radius": 26.5 * mm});
            skCircle(sketch, "E1932", {"center": v(1267.5, -506.62) * mm, "radius": 26.5 * mm});
            skCircle(sketch, "E1933", {"center": v(1300, -562.92) * mm, "radius": 26.5 * mm});
            skCircle(sketch, "E1934", {"center": v(1332.5, -619.2) * mm, "radius": 26.5 * mm});
            skCircle(sketch, "E1935", {"center": v(1365, -675.5) * mm, "radius": 26.5 * mm});
            skCircle(sketch, "E1936", {"center": v(1397.5, -731.8) * mm, "radius": 26.5 * mm});
            skCircle(sketch, "E1937", {"center": v(1072.5, -56.3) * mm, "radius": 26.5 * mm});
            skCircle(sketch, "E1938", {"center": v(1105, -112.58) * mm, "radius": 26.5 * mm});
            skCircle(sketch, "E1939", {"center": v(1137.5, -168.87) * mm, "radius": 26.5 * mm});
            skCircle(sketch, "E1940", {"center": v(1170, -225.17) * mm, "radius": 26.5 * mm});
            skCircle(sketch, "E1941", {"center": v(1202.5, -281.46) * mm, "radius": 26.5 * mm});
            skCircle(sketch, "E1942", {"center": v(1235, -337.75) * mm, "radius": 26.5 * mm});
            skCircle(sketch, "E1943", {"center": v(1267.5, -394.04) * mm, "radius": 26.5 * mm});
            skCircle(sketch, "E1944", {"center": v(1300, -450.33) * mm, "radius": 26.5 * mm});
            skCircle(sketch, "E1945", {"center": v(1332.5, -506.62) * mm, "radius": 26.5 * mm});
            skCircle(sketch, "E1946", {"center": v(1365, -562.92) * mm, "radius": 26.5 * mm});
            skCircle(sketch, "E1947", {"center": v(1397.5, -619.2) * mm, "radius": 26.5 * mm});
            skCircle(sketch, "E1948", {"center": v(1137.5, -56.3) * mm, "radius": 26.5 * mm});
            skCircle(sketch, "E1949", {"center": v(1170, -112.58) * mm, "radius": 26.5 * mm});
            skCircle(sketch, "E1950", {"center": v(1202.5, -168.87) * mm, "radius": 26.5 * mm});
            skCircle(sketch, "E1951", {"center": v(1235, -225.17) * mm, "radius": 26.5 * mm});
            skCircle(sketch, "E1952", {"center": v(1267.5, -281.46) * mm, "radius": 26.5 * mm});
            skCircle(sketch, "E1953", {"center": v(1300, -337.75) * mm, "radius": 26.5 * mm});
            skCircle(sketch, "E1954", {"center": v(1332.5, -394.04) * mm, "radius": 26.5 * mm});
            skCircle(sketch, "E1955", {"center": v(1365, -450.33) * mm, "radius": 26.5 * mm});
            skCircle(sketch, "E1956", {"center": v(1397.5, -506.62) * mm, "radius": 26.5 * mm});
            skCircle(sketch, "E1957", {"center": v(1430, -562.92) * mm, "radius": 26.5 * mm});
            skCircle(sketch, "E1958", {"center": v(1202.5, -56.3) * mm, "radius": 26.5 * mm});
            skCircle(sketch, "E1959", {"center": v(1235, -112.58) * mm, "radius": 26.5 * mm});
            skCircle(sketch, "E1960", {"center": v(1267.5, -168.87) * mm, "radius": 26.5 * mm});
            skCircle(sketch, "E1961", {"center": v(1300, -225.17) * mm, "radius": 26.5 * mm});
            skCircle(sketch, "E1962", {"center": v(1332.5, -281.46) * mm, "radius": 26.5 * mm});
            skCircle(sketch, "E1963", {"center": v(1365, -337.75) * mm, "radius": 26.5 * mm});
            skCircle(sketch, "E1964", {"center": v(1397.5, -394.04) * mm, "radius": 26.5 * mm});
            skCircle(sketch, "E1965", {"center": v(1430, -450.33) * mm, "radius": 26.5 * mm});
            skCircle(sketch, "E1966", {"center": v(1462.5, -506.62) * mm, "radius": 26.5 * mm});
            skCircle(sketch, "E1967", {"center": v(1267.5, -56.3) * mm, "radius": 26.5 * mm});
            skCircle(sketch, "E1968", {"center": v(1300, -112.58) * mm, "radius": 26.5 * mm});
            skCircle(sketch, "E1969", {"center": v(1332.5, -168.87) * mm, "radius": 26.5 * mm});
            skCircle(sketch, "E1970", {"center": v(1365, -225.17) * mm, "radius": 26.5 * mm});
            skCircle(sketch, "E1971", {"center": v(1397.5, -281.46) * mm, "radius": 26.5 * mm});
            skCircle(sketch, "E1972", {"center": v(1430, -337.75) * mm, "radius": 26.5 * mm});
            skCircle(sketch, "E1973", {"center": v(1462.5, -394.04) * mm, "radius": 26.5 * mm});
            skCircle(sketch, "E1974", {"center": v(1495, -450.33) * mm, "radius": 26.5 * mm});
            skCircle(sketch, "E1975", {"center": v(1332.5, -56.3) * mm, "radius": 26.5 * mm});
            skCircle(sketch, "E1976", {"center": v(1365, -112.58) * mm, "radius": 26.5 * mm});
            skCircle(sketch, "E1977", {"center": v(1397.5, -168.87) * mm, "radius": 26.5 * mm});
            skCircle(sketch, "E1978", {"center": v(1430, -225.17) * mm, "radius": 26.5 * mm});
            skCircle(sketch, "E1979", {"center": v(1462.5, -281.46) * mm, "radius": 26.5 * mm});
            skCircle(sketch, "E1980", {"center": v(1495, -337.75) * mm, "radius": 26.5 * mm});
            skCircle(sketch, "E1981", {"center": v(1527.5, -394.04) * mm, "radius": 26.5 * mm});
            skCircle(sketch, "E1982", {"center": v(1397.5, -56.3) * mm, "radius": 26.5 * mm});
            skCircle(sketch, "E1983", {"center": v(1430, -112.58) * mm, "radius": 26.5 * mm});
            skCircle(sketch, "E1984", {"center": v(1462.5, -168.87) * mm, "radius": 26.5 * mm});
            skCircle(sketch, "E1985", {"center": v(1495, -225.17) * mm, "radius": 26.5 * mm});
            skCircle(sketch, "E1986", {"center": v(1527.5, -281.46) * mm, "radius": 26.5 * mm});
            skCircle(sketch, "E1987", {"center": v(1462.5, -56.3) * mm, "radius": 26.5 * mm});
            skCircle(sketch, "E1988", {"center": v(1495, -112.58) * mm, "radius": 26.5 * mm});
            skCircle(sketch, "E1989", {"center": v(1527.5, -168.87) * mm, "radius": 26.5 * mm});
            skCircle(sketch, "E1990", {"center": v(1560, -225.17) * mm, "radius": 26.5 * mm});
            skCircle(sketch, "E1991", {"center": v(1527.5, -56.3) * mm, "radius": 26.5 * mm});
            skCircle(sketch, "E1992", {"center": v(1560, -112.58) * mm, "radius": 26.5 * mm});
            skCircle(sketch, "E1993", {"center": v(975, -562.92) * mm, "radius": 58 * mm});
            skArc(sketch, "E1994", {"start": v(-1674.02, -100) * mm, "mid": v(-838.5, -1452.32) * mm, "end": v(750.4, -1499.74) * mm});
            skCircle(sketch, "E1995", {"center": v(0, 0) * mm, "radius": 306.5 * mm});
            skCircle(sketch, "E1996", {"center": v(-1765, 0) * mm, "radius": 58 * mm});
            skLineSegment(sketch, "E1997", {"start": v(-1674.02, 100) * mm, "end": v(-1865, 100) * mm});
            skLineSegment(sketch, "E1998", {"start": v(-1865, 100) * mm, "end": v(-1865, -100) * mm});
            skLineSegment(sketch, "E1999", {"start": v(-1865, -100) * mm, "end": v(-1674.02, -100) * mm});
            skLineSegment(sketch, "E2000.1.0", {"start": v(750.4, -1499.74) * mm, "end": v(845.9, -1665.14) * mm});
            skCircle(sketch, "E2000.1.1", {"center": v(882.5, -1528.53) * mm, "radius": 58 * mm});
            skLineSegment(sketch, "E2000.1.2", {"start": v(1019.1, -1565.14) * mm, "end": v(923.61, -1399.74) * mm});
            skLineSegment(sketch, "E2000.1.3", {"start": v(845.9, -1665.14) * mm, "end": v(1019.1, -1565.14) * mm});
            skLineSegment(sketch, "E2000.2.0", {"start": v(923.61, 1399.74) * mm, "end": v(1019.1, 1565.14) * mm});
            skCircle(sketch, "E2000.2.1", {"center": v(882.5, 1528.53) * mm, "radius": 58 * mm});
            skLineSegment(sketch, "E2000.2.2", {"start": v(845.9, 1665.14) * mm, "end": v(750.4, 1499.74) * mm});
            skLineSegment(sketch, "E2000.2.3", {"start": v(1019.1, 1565.14) * mm, "end": v(845.9, 1665.14) * mm});
            skArc(sketch, "E2001.trimOffspring", {"start": v(923.61, -1399.74) * mm, "mid": v(1677, 0) * mm, "end": v(923.61, 1399.74) * mm});
            skArc(sketch, "E2002.trimOffspring", {"start": v(750.4, 1499.74) * mm, "mid": v(-838.5, 1452.32) * mm, "end": v(-1674.02, 100) * mm});
            skSolve(sketch);
        }
        {
            var Q0;
            Q0=makeQuery(id+"F1.imprint","IMPRINT",FACE,{"disambiguationData":[TD([[makeQuery(id+"F1.imprint","IMPRINT",EDGE,{"derivedFrom":sQuery(id+"F1.wireOp",EDGE,"E0")}),1.0]])]});
            extrude(context, id + "F2", {"entities" : qUnion([Q0]), "depth" : (getVariable(context, 'G3')) * mm});
        }
    });
